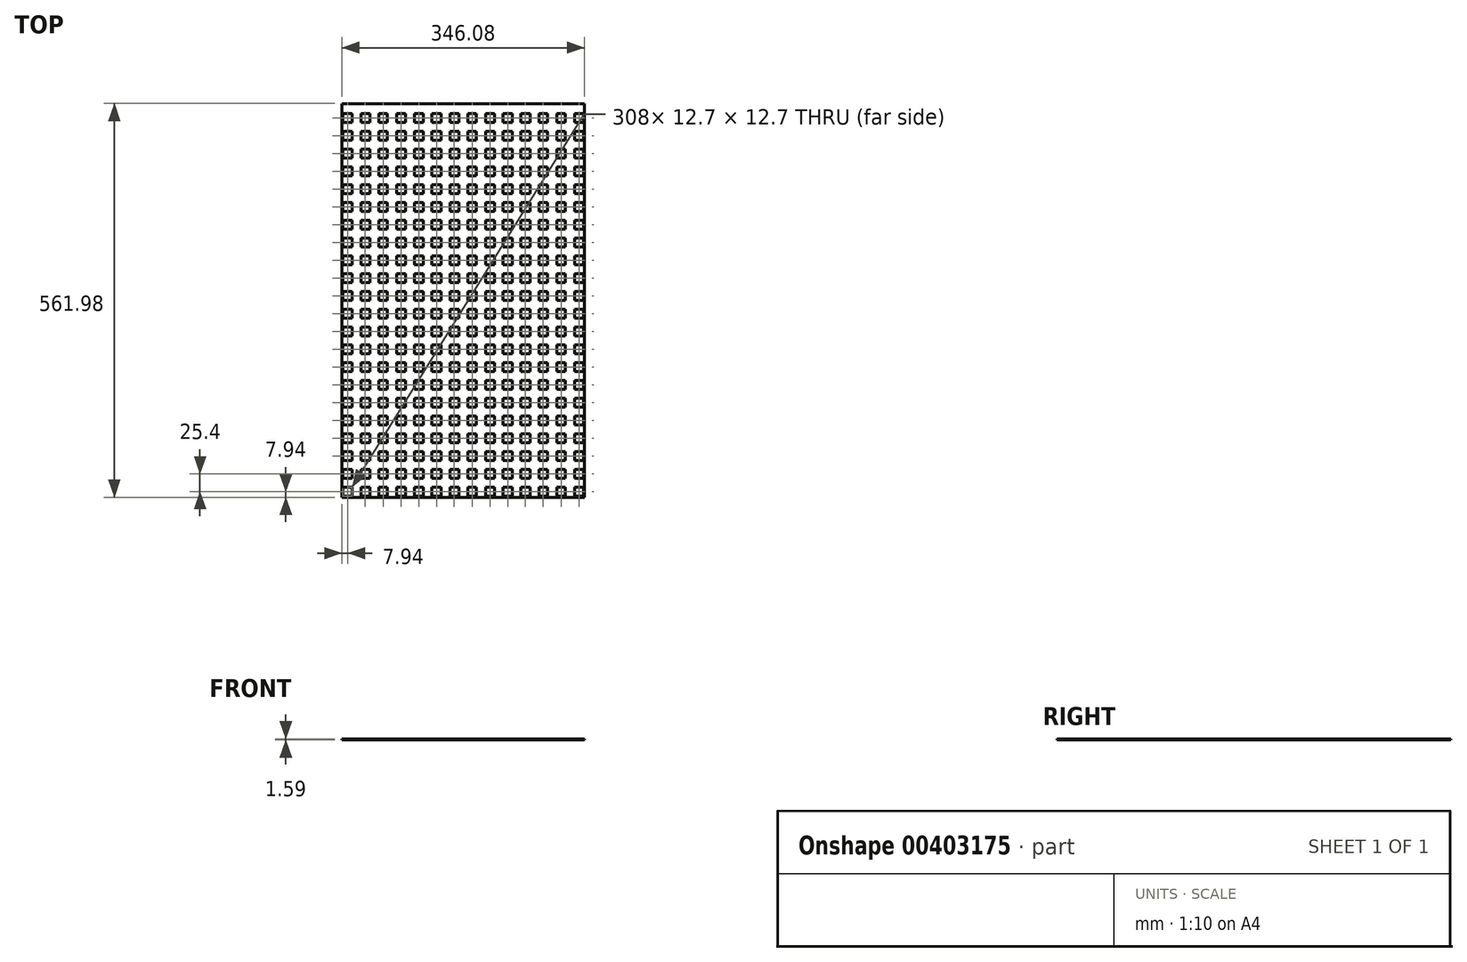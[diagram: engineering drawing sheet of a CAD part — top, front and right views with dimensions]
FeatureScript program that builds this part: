
annotation { "Feature Type Name" : "Feature", "Feature Type Description" : "" }
export const myFeature = defineFeature(function(context is Context, id is Id, definition is map)
    precondition{}
    {
        {
            var Q0;
            Q0=qCreatedBy(makeId("Top.planeOp"),FACE);
            var sketch = newSketch(context, id + "F0", { "sketchPlane" : qUnion([Q0])});
            skLineSegment(sketch, "E0.bottom", {"start": v(6.35, 6.35) * mm, "end": v(-6.35, 6.35) * mm});
            skLineSegment(sketch, "E0.top", {"start": v(6.35, -6.35) * mm, "end": v(-6.35, -6.35) * mm});
            skLineSegment(sketch, "E0.left", {"start": v(6.35, 6.35) * mm, "end": v(6.35, -6.35) * mm});
            skLineSegment(sketch, "E0.right", {"start": v(-6.35, 6.35) * mm, "end": v(-6.35, -6.35) * mm});
            skPoint(sketch, "E0.middle", {"position": v(0, 0) * mm});
            skLineSegment(sketch, "E1.0", {"start": v(4.76, 4.76) * mm, "end": v(-4.76, 4.76) * mm});
            skLineSegment(sketch, "E1.1", {"start": v(4.76, 4.76) * mm, "end": v(4.76, -4.76) * mm});
            skLineSegment(sketch, "E1.2", {"start": v(4.76, -4.76) * mm, "end": v(-4.76, -4.76) * mm});
            skLineSegment(sketch, "E1.3", {"start": v(-4.76, 4.76) * mm, "end": v(-4.76, -4.76) * mm});
            skLineSegment(sketch, "E2.0.1.0", {"start": v(6.35, 19.05) * mm, "end": v(-6.35, 19.05) * mm});
            skLineSegment(sketch, "E2.0.1.1", {"start": v(-4.76, 30.16) * mm, "end": v(-4.76, 20.64) * mm});
            skPoint(sketch, "E2.0.1.2", {"position": v(0, 25.4) * mm});
            skLineSegment(sketch, "E2.0.1.3", {"start": v(4.76, 20.64) * mm, "end": v(-4.76, 20.64) * mm});
            skLineSegment(sketch, "E2.0.1.4", {"start": v(6.35, 31.75) * mm, "end": v(6.35, 19.05) * mm});
            skLineSegment(sketch, "E2.0.1.5", {"start": v(6.35, 31.75) * mm, "end": v(-6.35, 31.75) * mm});
            skLineSegment(sketch, "E2.0.1.6", {"start": v(-6.35, 31.75) * mm, "end": v(-6.35, 19.05) * mm});
            skLineSegment(sketch, "E2.0.1.7", {"start": v(4.76, 30.16) * mm, "end": v(-4.76, 30.16) * mm});
            skLineSegment(sketch, "E2.0.1.8", {"start": v(4.76, 30.16) * mm, "end": v(4.76, 20.64) * mm});
            skLineSegment(sketch, "E2.0.2.0", {"start": v(6.35, 44.45) * mm, "end": v(-6.35, 44.45) * mm});
            skLineSegment(sketch, "E2.0.2.1", {"start": v(-4.76, 55.56) * mm, "end": v(-4.76, 46.04) * mm});
            skPoint(sketch, "E2.0.2.2", {"position": v(0, 50.8) * mm});
            skLineSegment(sketch, "E2.0.2.3", {"start": v(4.76, 46.04) * mm, "end": v(-4.76, 46.04) * mm});
            skLineSegment(sketch, "E2.0.2.4", {"start": v(6.35, 57.15) * mm, "end": v(6.35, 44.45) * mm});
            skLineSegment(sketch, "E2.0.2.5", {"start": v(6.35, 57.15) * mm, "end": v(-6.35, 57.15) * mm});
            skLineSegment(sketch, "E2.0.2.6", {"start": v(-6.35, 57.15) * mm, "end": v(-6.35, 44.45) * mm});
            skLineSegment(sketch, "E2.0.2.7", {"start": v(4.76, 55.56) * mm, "end": v(-4.76, 55.56) * mm});
            skLineSegment(sketch, "E2.0.2.8", {"start": v(4.76, 55.56) * mm, "end": v(4.76, 46.04) * mm});
            skLineSegment(sketch, "E2.0.3.0", {"start": v(6.35, 69.85) * mm, "end": v(-6.35, 69.85) * mm});
            skLineSegment(sketch, "E2.0.3.1", {"start": v(-4.76, 80.96) * mm, "end": v(-4.76, 71.44) * mm});
            skPoint(sketch, "E2.0.3.2", {"position": v(0, 76.2) * mm});
            skLineSegment(sketch, "E2.0.3.3", {"start": v(4.76, 71.44) * mm, "end": v(-4.76, 71.44) * mm});
            skLineSegment(sketch, "E2.0.3.4", {"start": v(6.35, 82.55) * mm, "end": v(6.35, 69.85) * mm});
            skLineSegment(sketch, "E2.0.3.5", {"start": v(6.35, 82.55) * mm, "end": v(-6.35, 82.55) * mm});
            skLineSegment(sketch, "E2.0.3.6", {"start": v(-6.35, 82.55) * mm, "end": v(-6.35, 69.85) * mm});
            skLineSegment(sketch, "E2.0.3.7", {"start": v(4.76, 80.96) * mm, "end": v(-4.76, 80.96) * mm});
            skLineSegment(sketch, "E2.0.3.8", {"start": v(4.76, 80.96) * mm, "end": v(4.76, 71.44) * mm});
            skLineSegment(sketch, "E2.0.4.0", {"start": v(6.35, 95.25) * mm, "end": v(-6.35, 95.25) * mm});
            skLineSegment(sketch, "E2.0.4.1", {"start": v(-4.76, 106.36) * mm, "end": v(-4.76, 96.84) * mm});
            skPoint(sketch, "E2.0.4.2", {"position": v(0, 101.6) * mm});
            skLineSegment(sketch, "E2.0.4.3", {"start": v(4.76, 96.84) * mm, "end": v(-4.76, 96.84) * mm});
            skLineSegment(sketch, "E2.0.4.4", {"start": v(6.35, 107.95) * mm, "end": v(6.35, 95.25) * mm});
            skLineSegment(sketch, "E2.0.4.5", {"start": v(6.35, 107.95) * mm, "end": v(-6.35, 107.95) * mm});
            skLineSegment(sketch, "E2.0.4.6", {"start": v(-6.35, 107.95) * mm, "end": v(-6.35, 95.25) * mm});
            skLineSegment(sketch, "E2.0.4.7", {"start": v(4.76, 106.36) * mm, "end": v(-4.76, 106.36) * mm});
            skLineSegment(sketch, "E2.0.4.8", {"start": v(4.76, 106.36) * mm, "end": v(4.76, 96.84) * mm});
            skLineSegment(sketch, "E2.0.5.0", {"start": v(6.35, 120.65) * mm, "end": v(-6.35, 120.65) * mm});
            skLineSegment(sketch, "E2.0.5.1", {"start": v(-4.76, 131.76) * mm, "end": v(-4.76, 122.24) * mm});
            skPoint(sketch, "E2.0.5.2", {"position": v(0, 127) * mm});
            skLineSegment(sketch, "E2.0.5.3", {"start": v(4.76, 122.24) * mm, "end": v(-4.76, 122.24) * mm});
            skLineSegment(sketch, "E2.0.5.4", {"start": v(6.35, 133.35) * mm, "end": v(6.35, 120.65) * mm});
            skLineSegment(sketch, "E2.0.5.5", {"start": v(6.35, 133.35) * mm, "end": v(-6.35, 133.35) * mm});
            skLineSegment(sketch, "E2.0.5.6", {"start": v(-6.35, 133.35) * mm, "end": v(-6.35, 120.65) * mm});
            skLineSegment(sketch, "E2.0.5.7", {"start": v(4.76, 131.76) * mm, "end": v(-4.76, 131.76) * mm});
            skLineSegment(sketch, "E2.0.5.8", {"start": v(4.76, 131.76) * mm, "end": v(4.76, 122.24) * mm});
            skLineSegment(sketch, "E2.0.6.0", {"start": v(6.35, 146.05) * mm, "end": v(-6.35, 146.05) * mm});
            skLineSegment(sketch, "E2.0.6.1", {"start": v(-4.76, 157.16) * mm, "end": v(-4.76, 147.64) * mm});
            skPoint(sketch, "E2.0.6.2", {"position": v(0, 152.4) * mm});
            skLineSegment(sketch, "E2.0.6.3", {"start": v(4.76, 147.64) * mm, "end": v(-4.76, 147.64) * mm});
            skLineSegment(sketch, "E2.0.6.4", {"start": v(6.35, 158.75) * mm, "end": v(6.35, 146.05) * mm});
            skLineSegment(sketch, "E2.0.6.5", {"start": v(6.35, 158.75) * mm, "end": v(-6.35, 158.75) * mm});
            skLineSegment(sketch, "E2.0.6.6", {"start": v(-6.35, 158.75) * mm, "end": v(-6.35, 146.05) * mm});
            skLineSegment(sketch, "E2.0.6.7", {"start": v(4.76, 157.16) * mm, "end": v(-4.76, 157.16) * mm});
            skLineSegment(sketch, "E2.0.6.8", {"start": v(4.76, 157.16) * mm, "end": v(4.76, 147.64) * mm});
            skLineSegment(sketch, "E2.0.7.0", {"start": v(6.35, 171.45) * mm, "end": v(-6.35, 171.45) * mm});
            skLineSegment(sketch, "E2.0.7.1", {"start": v(-4.76, 182.56) * mm, "end": v(-4.76, 173.04) * mm});
            skPoint(sketch, "E2.0.7.2", {"position": v(0, 177.8) * mm});
            skLineSegment(sketch, "E2.0.7.3", {"start": v(4.76, 173.04) * mm, "end": v(-4.76, 173.04) * mm});
            skLineSegment(sketch, "E2.0.7.4", {"start": v(6.35, 184.15) * mm, "end": v(6.35, 171.45) * mm});
            skLineSegment(sketch, "E2.0.7.5", {"start": v(6.35, 184.15) * mm, "end": v(-6.35, 184.15) * mm});
            skLineSegment(sketch, "E2.0.7.6", {"start": v(-6.35, 184.15) * mm, "end": v(-6.35, 171.45) * mm});
            skLineSegment(sketch, "E2.0.7.7", {"start": v(4.76, 182.56) * mm, "end": v(-4.76, 182.56) * mm});
            skLineSegment(sketch, "E2.0.7.8", {"start": v(4.76, 182.56) * mm, "end": v(4.76, 173.04) * mm});
            skLineSegment(sketch, "E2.0.8.0", {"start": v(6.35, 196.85) * mm, "end": v(-6.35, 196.85) * mm});
            skLineSegment(sketch, "E2.0.8.1", {"start": v(-4.76, 207.96) * mm, "end": v(-4.76, 198.44) * mm});
            skPoint(sketch, "E2.0.8.2", {"position": v(0, 203.2) * mm});
            skLineSegment(sketch, "E2.0.8.3", {"start": v(4.76, 198.44) * mm, "end": v(-4.76, 198.44) * mm});
            skLineSegment(sketch, "E2.0.8.4", {"start": v(6.35, 209.55) * mm, "end": v(6.35, 196.85) * mm});
            skLineSegment(sketch, "E2.0.8.5", {"start": v(6.35, 209.55) * mm, "end": v(-6.35, 209.55) * mm});
            skLineSegment(sketch, "E2.0.8.6", {"start": v(-6.35, 209.55) * mm, "end": v(-6.35, 196.85) * mm});
            skLineSegment(sketch, "E2.0.8.7", {"start": v(4.76, 207.96) * mm, "end": v(-4.76, 207.96) * mm});
            skLineSegment(sketch, "E2.0.8.8", {"start": v(4.76, 207.96) * mm, "end": v(4.76, 198.44) * mm});
            skLineSegment(sketch, "E2.0.9.0", {"start": v(6.35, 222.25) * mm, "end": v(-6.35, 222.25) * mm});
            skLineSegment(sketch, "E2.0.9.1", {"start": v(-4.76, 233.36) * mm, "end": v(-4.76, 223.84) * mm});
            skPoint(sketch, "E2.0.9.2", {"position": v(0, 228.6) * mm});
            skLineSegment(sketch, "E2.0.9.3", {"start": v(4.76, 223.84) * mm, "end": v(-4.76, 223.84) * mm});
            skLineSegment(sketch, "E2.0.9.4", {"start": v(6.35, 234.95) * mm, "end": v(6.35, 222.25) * mm});
            skLineSegment(sketch, "E2.0.9.5", {"start": v(6.35, 234.95) * mm, "end": v(-6.35, 234.95) * mm});
            skLineSegment(sketch, "E2.0.9.6", {"start": v(-6.35, 234.95) * mm, "end": v(-6.35, 222.25) * mm});
            skLineSegment(sketch, "E2.0.9.7", {"start": v(4.76, 233.36) * mm, "end": v(-4.76, 233.36) * mm});
            skLineSegment(sketch, "E2.0.9.8", {"start": v(4.76, 233.36) * mm, "end": v(4.76, 223.84) * mm});
            skLineSegment(sketch, "E2.0.10.0", {"start": v(6.35, 247.65) * mm, "end": v(-6.35, 247.65) * mm});
            skLineSegment(sketch, "E2.0.10.1", {"start": v(-4.76, 258.76) * mm, "end": v(-4.76, 249.24) * mm});
            skPoint(sketch, "E2.0.10.2", {"position": v(0, 254) * mm});
            skLineSegment(sketch, "E2.0.10.3", {"start": v(4.76, 249.24) * mm, "end": v(-4.76, 249.24) * mm});
            skLineSegment(sketch, "E2.0.10.4", {"start": v(6.35, 260.35) * mm, "end": v(6.35, 247.65) * mm});
            skLineSegment(sketch, "E2.0.10.5", {"start": v(6.35, 260.35) * mm, "end": v(-6.35, 260.35) * mm});
            skLineSegment(sketch, "E2.0.10.6", {"start": v(-6.35, 260.35) * mm, "end": v(-6.35, 247.65) * mm});
            skLineSegment(sketch, "E2.0.10.7", {"start": v(4.76, 258.76) * mm, "end": v(-4.76, 258.76) * mm});
            skLineSegment(sketch, "E2.0.10.8", {"start": v(4.76, 258.76) * mm, "end": v(4.76, 249.24) * mm});
            skLineSegment(sketch, "E2.0.11.0", {"start": v(6.35, 273.05) * mm, "end": v(-6.35, 273.05) * mm});
            skLineSegment(sketch, "E2.0.11.1", {"start": v(-4.76, 284.16) * mm, "end": v(-4.76, 274.64) * mm});
            skPoint(sketch, "E2.0.11.2", {"position": v(0, 279.4) * mm});
            skLineSegment(sketch, "E2.0.11.3", {"start": v(4.76, 274.64) * mm, "end": v(-4.76, 274.64) * mm});
            skLineSegment(sketch, "E2.0.11.4", {"start": v(6.35, 285.75) * mm, "end": v(6.35, 273.05) * mm});
            skLineSegment(sketch, "E2.0.11.5", {"start": v(6.35, 285.75) * mm, "end": v(-6.35, 285.75) * mm});
            skLineSegment(sketch, "E2.0.11.6", {"start": v(-6.35, 285.75) * mm, "end": v(-6.35, 273.05) * mm});
            skLineSegment(sketch, "E2.0.11.7", {"start": v(4.76, 284.16) * mm, "end": v(-4.76, 284.16) * mm});
            skLineSegment(sketch, "E2.0.11.8", {"start": v(4.76, 284.16) * mm, "end": v(4.76, 274.64) * mm});
            skLineSegment(sketch, "E2.0.12.0", {"start": v(6.35, 298.45) * mm, "end": v(-6.35, 298.45) * mm});
            skLineSegment(sketch, "E2.0.12.1", {"start": v(-4.76, 309.56) * mm, "end": v(-4.76, 300.04) * mm});
            skPoint(sketch, "E2.0.12.2", {"position": v(0, 304.8) * mm});
            skLineSegment(sketch, "E2.0.12.3", {"start": v(4.76, 300.04) * mm, "end": v(-4.76, 300.04) * mm});
            skLineSegment(sketch, "E2.0.12.4", {"start": v(6.35, 311.15) * mm, "end": v(6.35, 298.45) * mm});
            skLineSegment(sketch, "E2.0.12.5", {"start": v(6.35, 311.15) * mm, "end": v(-6.35, 311.15) * mm});
            skLineSegment(sketch, "E2.0.12.6", {"start": v(-6.35, 311.15) * mm, "end": v(-6.35, 298.45) * mm});
            skLineSegment(sketch, "E2.0.12.7", {"start": v(4.76, 309.56) * mm, "end": v(-4.76, 309.56) * mm});
            skLineSegment(sketch, "E2.0.12.8", {"start": v(4.76, 309.56) * mm, "end": v(4.76, 300.04) * mm});
            skLineSegment(sketch, "E2.0.13.0", {"start": v(6.35, 323.85) * mm, "end": v(-6.35, 323.85) * mm});
            skLineSegment(sketch, "E2.0.13.1", {"start": v(-4.76, 334.96) * mm, "end": v(-4.76, 325.44) * mm});
            skPoint(sketch, "E2.0.13.2", {"position": v(0, 330.2) * mm});
            skLineSegment(sketch, "E2.0.13.3", {"start": v(4.76, 325.44) * mm, "end": v(-4.76, 325.44) * mm});
            skLineSegment(sketch, "E2.0.13.4", {"start": v(6.35, 336.55) * mm, "end": v(6.35, 323.85) * mm});
            skLineSegment(sketch, "E2.0.13.5", {"start": v(6.35, 336.55) * mm, "end": v(-6.35, 336.55) * mm});
            skLineSegment(sketch, "E2.0.13.6", {"start": v(-6.35, 336.55) * mm, "end": v(-6.35, 323.85) * mm});
            skLineSegment(sketch, "E2.0.13.7", {"start": v(4.76, 334.96) * mm, "end": v(-4.76, 334.96) * mm});
            skLineSegment(sketch, "E2.0.13.8", {"start": v(4.76, 334.96) * mm, "end": v(4.76, 325.44) * mm});
            skLineSegment(sketch, "E2.0.14.0", {"start": v(6.35, 349.25) * mm, "end": v(-6.35, 349.25) * mm});
            skLineSegment(sketch, "E2.0.14.1", {"start": v(-4.76, 360.36) * mm, "end": v(-4.76, 350.84) * mm});
            skPoint(sketch, "E2.0.14.2", {"position": v(0, 355.6) * mm});
            skLineSegment(sketch, "E2.0.14.3", {"start": v(4.76, 350.84) * mm, "end": v(-4.76, 350.84) * mm});
            skLineSegment(sketch, "E2.0.14.4", {"start": v(6.35, 361.95) * mm, "end": v(6.35, 349.25) * mm});
            skLineSegment(sketch, "E2.0.14.5", {"start": v(6.35, 361.95) * mm, "end": v(-6.35, 361.95) * mm});
            skLineSegment(sketch, "E2.0.14.6", {"start": v(-6.35, 361.95) * mm, "end": v(-6.35, 349.25) * mm});
            skLineSegment(sketch, "E2.0.14.7", {"start": v(4.76, 360.36) * mm, "end": v(-4.76, 360.36) * mm});
            skLineSegment(sketch, "E2.0.14.8", {"start": v(4.76, 360.36) * mm, "end": v(4.76, 350.84) * mm});
            skLineSegment(sketch, "E2.1.0.0", {"start": v(31.75, -6.35) * mm, "end": v(19.05, -6.35) * mm});
            skLineSegment(sketch, "E2.1.0.1", {"start": v(20.64, 4.76) * mm, "end": v(20.64, -4.76) * mm});
            skPoint(sketch, "E2.1.0.2", {"position": v(25.4, 0) * mm});
            skLineSegment(sketch, "E2.1.0.3", {"start": v(30.16, -4.76) * mm, "end": v(20.64, -4.76) * mm});
            skLineSegment(sketch, "E2.1.0.4", {"start": v(31.75, 6.35) * mm, "end": v(31.75, -6.35) * mm});
            skLineSegment(sketch, "E2.1.0.5", {"start": v(31.75, 6.35) * mm, "end": v(19.05, 6.35) * mm});
            skLineSegment(sketch, "E2.1.0.6", {"start": v(19.05, 6.35) * mm, "end": v(19.05, -6.35) * mm});
            skLineSegment(sketch, "E2.1.0.7", {"start": v(30.16, 4.76) * mm, "end": v(20.64, 4.76) * mm});
            skLineSegment(sketch, "E2.1.0.8", {"start": v(30.16, 4.76) * mm, "end": v(30.16, -4.76) * mm});
            skLineSegment(sketch, "E2.1.1.0", {"start": v(31.75, 19.05) * mm, "end": v(19.05, 19.05) * mm});
            skLineSegment(sketch, "E2.1.1.1", {"start": v(20.64, 30.16) * mm, "end": v(20.64, 20.64) * mm});
            skPoint(sketch, "E2.1.1.2", {"position": v(25.4, 25.4) * mm});
            skLineSegment(sketch, "E2.1.1.3", {"start": v(30.16, 20.64) * mm, "end": v(20.64, 20.64) * mm});
            skLineSegment(sketch, "E2.1.1.4", {"start": v(31.75, 31.75) * mm, "end": v(31.75, 19.05) * mm});
            skLineSegment(sketch, "E2.1.1.5", {"start": v(31.75, 31.75) * mm, "end": v(19.05, 31.75) * mm});
            skLineSegment(sketch, "E2.1.1.6", {"start": v(19.05, 31.75) * mm, "end": v(19.05, 19.05) * mm});
            skLineSegment(sketch, "E2.1.1.7", {"start": v(30.16, 30.16) * mm, "end": v(20.64, 30.16) * mm});
            skLineSegment(sketch, "E2.1.1.8", {"start": v(30.16, 30.16) * mm, "end": v(30.16, 20.64) * mm});
            skLineSegment(sketch, "E2.1.2.0", {"start": v(31.75, 44.45) * mm, "end": v(19.05, 44.45) * mm});
            skLineSegment(sketch, "E2.1.2.1", {"start": v(20.64, 55.56) * mm, "end": v(20.64, 46.04) * mm});
            skPoint(sketch, "E2.1.2.2", {"position": v(25.4, 50.8) * mm});
            skLineSegment(sketch, "E2.1.2.3", {"start": v(30.16, 46.04) * mm, "end": v(20.64, 46.04) * mm});
            skLineSegment(sketch, "E2.1.2.4", {"start": v(31.75, 57.15) * mm, "end": v(31.75, 44.45) * mm});
            skLineSegment(sketch, "E2.1.2.5", {"start": v(31.75, 57.15) * mm, "end": v(19.05, 57.15) * mm});
            skLineSegment(sketch, "E2.1.2.6", {"start": v(19.05, 57.15) * mm, "end": v(19.05, 44.45) * mm});
            skLineSegment(sketch, "E2.1.2.7", {"start": v(30.16, 55.56) * mm, "end": v(20.64, 55.56) * mm});
            skLineSegment(sketch, "E2.1.2.8", {"start": v(30.16, 55.56) * mm, "end": v(30.16, 46.04) * mm});
            skLineSegment(sketch, "E2.1.3.0", {"start": v(31.75, 69.85) * mm, "end": v(19.05, 69.85) * mm});
            skLineSegment(sketch, "E2.1.3.1", {"start": v(20.64, 80.96) * mm, "end": v(20.64, 71.44) * mm});
            skPoint(sketch, "E2.1.3.2", {"position": v(25.4, 76.2) * mm});
            skLineSegment(sketch, "E2.1.3.3", {"start": v(30.16, 71.44) * mm, "end": v(20.64, 71.44) * mm});
            skLineSegment(sketch, "E2.1.3.4", {"start": v(31.75, 82.55) * mm, "end": v(31.75, 69.85) * mm});
            skLineSegment(sketch, "E2.1.3.5", {"start": v(31.75, 82.55) * mm, "end": v(19.05, 82.55) * mm});
            skLineSegment(sketch, "E2.1.3.6", {"start": v(19.05, 82.55) * mm, "end": v(19.05, 69.85) * mm});
            skLineSegment(sketch, "E2.1.3.7", {"start": v(30.16, 80.96) * mm, "end": v(20.64, 80.96) * mm});
            skLineSegment(sketch, "E2.1.3.8", {"start": v(30.16, 80.96) * mm, "end": v(30.16, 71.44) * mm});
            skLineSegment(sketch, "E2.1.4.0", {"start": v(31.75, 95.25) * mm, "end": v(19.05, 95.25) * mm});
            skLineSegment(sketch, "E2.1.4.1", {"start": v(20.64, 106.36) * mm, "end": v(20.64, 96.84) * mm});
            skPoint(sketch, "E2.1.4.2", {"position": v(25.4, 101.6) * mm});
            skLineSegment(sketch, "E2.1.4.3", {"start": v(30.16, 96.84) * mm, "end": v(20.64, 96.84) * mm});
            skLineSegment(sketch, "E2.1.4.4", {"start": v(31.75, 107.95) * mm, "end": v(31.75, 95.25) * mm});
            skLineSegment(sketch, "E2.1.4.5", {"start": v(31.75, 107.95) * mm, "end": v(19.05, 107.95) * mm});
            skLineSegment(sketch, "E2.1.4.6", {"start": v(19.05, 107.95) * mm, "end": v(19.05, 95.25) * mm});
            skLineSegment(sketch, "E2.1.4.7", {"start": v(30.16, 106.36) * mm, "end": v(20.64, 106.36) * mm});
            skLineSegment(sketch, "E2.1.4.8", {"start": v(30.16, 106.36) * mm, "end": v(30.16, 96.84) * mm});
            skLineSegment(sketch, "E2.1.5.0", {"start": v(31.75, 120.65) * mm, "end": v(19.05, 120.65) * mm});
            skLineSegment(sketch, "E2.1.5.1", {"start": v(20.64, 131.76) * mm, "end": v(20.64, 122.24) * mm});
            skPoint(sketch, "E2.1.5.2", {"position": v(25.4, 127) * mm});
            skLineSegment(sketch, "E2.1.5.3", {"start": v(30.16, 122.24) * mm, "end": v(20.64, 122.24) * mm});
            skLineSegment(sketch, "E2.1.5.4", {"start": v(31.75, 133.35) * mm, "end": v(31.75, 120.65) * mm});
            skLineSegment(sketch, "E2.1.5.5", {"start": v(31.75, 133.35) * mm, "end": v(19.05, 133.35) * mm});
            skLineSegment(sketch, "E2.1.5.6", {"start": v(19.05, 133.35) * mm, "end": v(19.05, 120.65) * mm});
            skLineSegment(sketch, "E2.1.5.7", {"start": v(30.16, 131.76) * mm, "end": v(20.64, 131.76) * mm});
            skLineSegment(sketch, "E2.1.5.8", {"start": v(30.16, 131.76) * mm, "end": v(30.16, 122.24) * mm});
            skLineSegment(sketch, "E2.1.6.0", {"start": v(31.75, 146.05) * mm, "end": v(19.05, 146.05) * mm});
            skLineSegment(sketch, "E2.1.6.1", {"start": v(20.64, 157.16) * mm, "end": v(20.64, 147.64) * mm});
            skPoint(sketch, "E2.1.6.2", {"position": v(25.4, 152.4) * mm});
            skLineSegment(sketch, "E2.1.6.3", {"start": v(30.16, 147.64) * mm, "end": v(20.64, 147.64) * mm});
            skLineSegment(sketch, "E2.1.6.4", {"start": v(31.75, 158.75) * mm, "end": v(31.75, 146.05) * mm});
            skLineSegment(sketch, "E2.1.6.5", {"start": v(31.75, 158.75) * mm, "end": v(19.05, 158.75) * mm});
            skLineSegment(sketch, "E2.1.6.6", {"start": v(19.05, 158.75) * mm, "end": v(19.05, 146.05) * mm});
            skLineSegment(sketch, "E2.1.6.7", {"start": v(30.16, 157.16) * mm, "end": v(20.64, 157.16) * mm});
            skLineSegment(sketch, "E2.1.6.8", {"start": v(30.16, 157.16) * mm, "end": v(30.16, 147.64) * mm});
            skLineSegment(sketch, "E2.1.7.0", {"start": v(31.75, 171.45) * mm, "end": v(19.05, 171.45) * mm});
            skLineSegment(sketch, "E2.1.7.1", {"start": v(20.64, 182.56) * mm, "end": v(20.64, 173.04) * mm});
            skPoint(sketch, "E2.1.7.2", {"position": v(25.4, 177.8) * mm});
            skLineSegment(sketch, "E2.1.7.3", {"start": v(30.16, 173.04) * mm, "end": v(20.64, 173.04) * mm});
            skLineSegment(sketch, "E2.1.7.4", {"start": v(31.75, 184.15) * mm, "end": v(31.75, 171.45) * mm});
            skLineSegment(sketch, "E2.1.7.5", {"start": v(31.75, 184.15) * mm, "end": v(19.05, 184.15) * mm});
            skLineSegment(sketch, "E2.1.7.6", {"start": v(19.05, 184.15) * mm, "end": v(19.05, 171.45) * mm});
            skLineSegment(sketch, "E2.1.7.7", {"start": v(30.16, 182.56) * mm, "end": v(20.64, 182.56) * mm});
            skLineSegment(sketch, "E2.1.7.8", {"start": v(30.16, 182.56) * mm, "end": v(30.16, 173.04) * mm});
            skLineSegment(sketch, "E2.1.8.0", {"start": v(31.75, 196.85) * mm, "end": v(19.05, 196.85) * mm});
            skLineSegment(sketch, "E2.1.8.1", {"start": v(20.64, 207.96) * mm, "end": v(20.64, 198.44) * mm});
            skPoint(sketch, "E2.1.8.2", {"position": v(25.4, 203.2) * mm});
            skLineSegment(sketch, "E2.1.8.3", {"start": v(30.16, 198.44) * mm, "end": v(20.64, 198.44) * mm});
            skLineSegment(sketch, "E2.1.8.4", {"start": v(31.75, 209.55) * mm, "end": v(31.75, 196.85) * mm});
            skLineSegment(sketch, "E2.1.8.5", {"start": v(31.75, 209.55) * mm, "end": v(19.05, 209.55) * mm});
            skLineSegment(sketch, "E2.1.8.6", {"start": v(19.05, 209.55) * mm, "end": v(19.05, 196.85) * mm});
            skLineSegment(sketch, "E2.1.8.7", {"start": v(30.16, 207.96) * mm, "end": v(20.64, 207.96) * mm});
            skLineSegment(sketch, "E2.1.8.8", {"start": v(30.16, 207.96) * mm, "end": v(30.16, 198.44) * mm});
            skLineSegment(sketch, "E2.1.9.0", {"start": v(31.75, 222.25) * mm, "end": v(19.05, 222.25) * mm});
            skLineSegment(sketch, "E2.1.9.1", {"start": v(20.64, 233.36) * mm, "end": v(20.64, 223.84) * mm});
            skPoint(sketch, "E2.1.9.2", {"position": v(25.4, 228.6) * mm});
            skLineSegment(sketch, "E2.1.9.3", {"start": v(30.16, 223.84) * mm, "end": v(20.64, 223.84) * mm});
            skLineSegment(sketch, "E2.1.9.4", {"start": v(31.75, 234.95) * mm, "end": v(31.75, 222.25) * mm});
            skLineSegment(sketch, "E2.1.9.5", {"start": v(31.75, 234.95) * mm, "end": v(19.05, 234.95) * mm});
            skLineSegment(sketch, "E2.1.9.6", {"start": v(19.05, 234.95) * mm, "end": v(19.05, 222.25) * mm});
            skLineSegment(sketch, "E2.1.9.7", {"start": v(30.16, 233.36) * mm, "end": v(20.64, 233.36) * mm});
            skLineSegment(sketch, "E2.1.9.8", {"start": v(30.16, 233.36) * mm, "end": v(30.16, 223.84) * mm});
            skLineSegment(sketch, "E2.1.10.0", {"start": v(31.75, 247.65) * mm, "end": v(19.05, 247.65) * mm});
            skLineSegment(sketch, "E2.1.10.1", {"start": v(20.64, 258.76) * mm, "end": v(20.64, 249.24) * mm});
            skPoint(sketch, "E2.1.10.2", {"position": v(25.4, 254) * mm});
            skLineSegment(sketch, "E2.1.10.3", {"start": v(30.16, 249.24) * mm, "end": v(20.64, 249.24) * mm});
            skLineSegment(sketch, "E2.1.10.4", {"start": v(31.75, 260.35) * mm, "end": v(31.75, 247.65) * mm});
            skLineSegment(sketch, "E2.1.10.5", {"start": v(31.75, 260.35) * mm, "end": v(19.05, 260.35) * mm});
            skLineSegment(sketch, "E2.1.10.6", {"start": v(19.05, 260.35) * mm, "end": v(19.05, 247.65) * mm});
            skLineSegment(sketch, "E2.1.10.7", {"start": v(30.16, 258.76) * mm, "end": v(20.64, 258.76) * mm});
            skLineSegment(sketch, "E2.1.10.8", {"start": v(30.16, 258.76) * mm, "end": v(30.16, 249.24) * mm});
            skLineSegment(sketch, "E2.1.11.0", {"start": v(31.75, 273.05) * mm, "end": v(19.05, 273.05) * mm});
            skLineSegment(sketch, "E2.1.11.1", {"start": v(20.64, 284.16) * mm, "end": v(20.64, 274.64) * mm});
            skPoint(sketch, "E2.1.11.2", {"position": v(25.4, 279.4) * mm});
            skLineSegment(sketch, "E2.1.11.3", {"start": v(30.16, 274.64) * mm, "end": v(20.64, 274.64) * mm});
            skLineSegment(sketch, "E2.1.11.4", {"start": v(31.75, 285.75) * mm, "end": v(31.75, 273.05) * mm});
            skLineSegment(sketch, "E2.1.11.5", {"start": v(31.75, 285.75) * mm, "end": v(19.05, 285.75) * mm});
            skLineSegment(sketch, "E2.1.11.6", {"start": v(19.05, 285.75) * mm, "end": v(19.05, 273.05) * mm});
            skLineSegment(sketch, "E2.1.11.7", {"start": v(30.16, 284.16) * mm, "end": v(20.64, 284.16) * mm});
            skLineSegment(sketch, "E2.1.11.8", {"start": v(30.16, 284.16) * mm, "end": v(30.16, 274.64) * mm});
            skLineSegment(sketch, "E2.1.12.0", {"start": v(31.75, 298.45) * mm, "end": v(19.05, 298.45) * mm});
            skLineSegment(sketch, "E2.1.12.1", {"start": v(20.64, 309.56) * mm, "end": v(20.64, 300.04) * mm});
            skPoint(sketch, "E2.1.12.2", {"position": v(25.4, 304.8) * mm});
            skLineSegment(sketch, "E2.1.12.3", {"start": v(30.16, 300.04) * mm, "end": v(20.64, 300.04) * mm});
            skLineSegment(sketch, "E2.1.12.4", {"start": v(31.75, 311.15) * mm, "end": v(31.75, 298.45) * mm});
            skLineSegment(sketch, "E2.1.12.5", {"start": v(31.75, 311.15) * mm, "end": v(19.05, 311.15) * mm});
            skLineSegment(sketch, "E2.1.12.6", {"start": v(19.05, 311.15) * mm, "end": v(19.05, 298.45) * mm});
            skLineSegment(sketch, "E2.1.12.7", {"start": v(30.16, 309.56) * mm, "end": v(20.64, 309.56) * mm});
            skLineSegment(sketch, "E2.1.12.8", {"start": v(30.16, 309.56) * mm, "end": v(30.16, 300.04) * mm});
            skLineSegment(sketch, "E2.1.13.0", {"start": v(31.75, 323.85) * mm, "end": v(19.05, 323.85) * mm});
            skLineSegment(sketch, "E2.1.13.1", {"start": v(20.64, 334.96) * mm, "end": v(20.64, 325.44) * mm});
            skPoint(sketch, "E2.1.13.2", {"position": v(25.4, 330.2) * mm});
            skLineSegment(sketch, "E2.1.13.3", {"start": v(30.16, 325.44) * mm, "end": v(20.64, 325.44) * mm});
            skLineSegment(sketch, "E2.1.13.4", {"start": v(31.75, 336.55) * mm, "end": v(31.75, 323.85) * mm});
            skLineSegment(sketch, "E2.1.13.5", {"start": v(31.75, 336.55) * mm, "end": v(19.05, 336.55) * mm});
            skLineSegment(sketch, "E2.1.13.6", {"start": v(19.05, 336.55) * mm, "end": v(19.05, 323.85) * mm});
            skLineSegment(sketch, "E2.1.13.7", {"start": v(30.16, 334.96) * mm, "end": v(20.64, 334.96) * mm});
            skLineSegment(sketch, "E2.1.13.8", {"start": v(30.16, 334.96) * mm, "end": v(30.16, 325.44) * mm});
            skLineSegment(sketch, "E2.1.14.0", {"start": v(31.75, 349.25) * mm, "end": v(19.05, 349.25) * mm});
            skLineSegment(sketch, "E2.1.14.1", {"start": v(20.64, 360.36) * mm, "end": v(20.64, 350.84) * mm});
            skPoint(sketch, "E2.1.14.2", {"position": v(25.4, 355.6) * mm});
            skLineSegment(sketch, "E2.1.14.3", {"start": v(30.16, 350.84) * mm, "end": v(20.64, 350.84) * mm});
            skLineSegment(sketch, "E2.1.14.4", {"start": v(31.75, 361.95) * mm, "end": v(31.75, 349.25) * mm});
            skLineSegment(sketch, "E2.1.14.5", {"start": v(31.75, 361.95) * mm, "end": v(19.05, 361.95) * mm});
            skLineSegment(sketch, "E2.1.14.6", {"start": v(19.05, 361.95) * mm, "end": v(19.05, 349.25) * mm});
            skLineSegment(sketch, "E2.1.14.7", {"start": v(30.16, 360.36) * mm, "end": v(20.64, 360.36) * mm});
            skLineSegment(sketch, "E2.1.14.8", {"start": v(30.16, 360.36) * mm, "end": v(30.16, 350.84) * mm});
            skLineSegment(sketch, "E2.2.0.0", {"start": v(57.15, -6.35) * mm, "end": v(44.45, -6.35) * mm});
            skLineSegment(sketch, "E2.2.0.1", {"start": v(46.04, 4.76) * mm, "end": v(46.04, -4.76) * mm});
            skPoint(sketch, "E2.2.0.2", {"position": v(50.8, 0) * mm});
            skLineSegment(sketch, "E2.2.0.3", {"start": v(55.56, -4.76) * mm, "end": v(46.04, -4.76) * mm});
            skLineSegment(sketch, "E2.2.0.4", {"start": v(57.15, 6.35) * mm, "end": v(57.15, -6.35) * mm});
            skLineSegment(sketch, "E2.2.0.5", {"start": v(57.15, 6.35) * mm, "end": v(44.45, 6.35) * mm});
            skLineSegment(sketch, "E2.2.0.6", {"start": v(44.45, 6.35) * mm, "end": v(44.45, -6.35) * mm});
            skLineSegment(sketch, "E2.2.0.7", {"start": v(55.56, 4.76) * mm, "end": v(46.04, 4.76) * mm});
            skLineSegment(sketch, "E2.2.0.8", {"start": v(55.56, 4.76) * mm, "end": v(55.56, -4.76) * mm});
            skLineSegment(sketch, "E2.2.1.0", {"start": v(57.15, 19.05) * mm, "end": v(44.45, 19.05) * mm});
            skLineSegment(sketch, "E2.2.1.1", {"start": v(46.04, 30.16) * mm, "end": v(46.04, 20.64) * mm});
            skPoint(sketch, "E2.2.1.2", {"position": v(50.8, 25.4) * mm});
            skLineSegment(sketch, "E2.2.1.3", {"start": v(55.56, 20.64) * mm, "end": v(46.04, 20.64) * mm});
            skLineSegment(sketch, "E2.2.1.4", {"start": v(57.15, 31.75) * mm, "end": v(57.15, 19.05) * mm});
            skLineSegment(sketch, "E2.2.1.5", {"start": v(57.15, 31.75) * mm, "end": v(44.45, 31.75) * mm});
            skLineSegment(sketch, "E2.2.1.6", {"start": v(44.45, 31.75) * mm, "end": v(44.45, 19.05) * mm});
            skLineSegment(sketch, "E2.2.1.7", {"start": v(55.56, 30.16) * mm, "end": v(46.04, 30.16) * mm});
            skLineSegment(sketch, "E2.2.1.8", {"start": v(55.56, 30.16) * mm, "end": v(55.56, 20.64) * mm});
            skLineSegment(sketch, "E2.2.2.0", {"start": v(57.15, 44.45) * mm, "end": v(44.45, 44.45) * mm});
            skLineSegment(sketch, "E2.2.2.1", {"start": v(46.04, 55.56) * mm, "end": v(46.04, 46.04) * mm});
            skPoint(sketch, "E2.2.2.2", {"position": v(50.8, 50.8) * mm});
            skLineSegment(sketch, "E2.2.2.3", {"start": v(55.56, 46.04) * mm, "end": v(46.04, 46.04) * mm});
            skLineSegment(sketch, "E2.2.2.4", {"start": v(57.15, 57.15) * mm, "end": v(57.15, 44.45) * mm});
            skLineSegment(sketch, "E2.2.2.5", {"start": v(57.15, 57.15) * mm, "end": v(44.45, 57.15) * mm});
            skLineSegment(sketch, "E2.2.2.6", {"start": v(44.45, 57.15) * mm, "end": v(44.45, 44.45) * mm});
            skLineSegment(sketch, "E2.2.2.7", {"start": v(55.56, 55.56) * mm, "end": v(46.04, 55.56) * mm});
            skLineSegment(sketch, "E2.2.2.8", {"start": v(55.56, 55.56) * mm, "end": v(55.56, 46.04) * mm});
            skLineSegment(sketch, "E2.2.3.0", {"start": v(57.15, 69.85) * mm, "end": v(44.45, 69.85) * mm});
            skLineSegment(sketch, "E2.2.3.1", {"start": v(46.04, 80.96) * mm, "end": v(46.04, 71.44) * mm});
            skPoint(sketch, "E2.2.3.2", {"position": v(50.8, 76.2) * mm});
            skLineSegment(sketch, "E2.2.3.3", {"start": v(55.56, 71.44) * mm, "end": v(46.04, 71.44) * mm});
            skLineSegment(sketch, "E2.2.3.4", {"start": v(57.15, 82.55) * mm, "end": v(57.15, 69.85) * mm});
            skLineSegment(sketch, "E2.2.3.5", {"start": v(57.15, 82.55) * mm, "end": v(44.45, 82.55) * mm});
            skLineSegment(sketch, "E2.2.3.6", {"start": v(44.45, 82.55) * mm, "end": v(44.45, 69.85) * mm});
            skLineSegment(sketch, "E2.2.3.7", {"start": v(55.56, 80.96) * mm, "end": v(46.04, 80.96) * mm});
            skLineSegment(sketch, "E2.2.3.8", {"start": v(55.56, 80.96) * mm, "end": v(55.56, 71.44) * mm});
            skLineSegment(sketch, "E2.2.4.0", {"start": v(57.15, 95.25) * mm, "end": v(44.45, 95.25) * mm});
            skLineSegment(sketch, "E2.2.4.1", {"start": v(46.04, 106.36) * mm, "end": v(46.04, 96.84) * mm});
            skPoint(sketch, "E2.2.4.2", {"position": v(50.8, 101.6) * mm});
            skLineSegment(sketch, "E2.2.4.3", {"start": v(55.56, 96.84) * mm, "end": v(46.04, 96.84) * mm});
            skLineSegment(sketch, "E2.2.4.4", {"start": v(57.15, 107.95) * mm, "end": v(57.15, 95.25) * mm});
            skLineSegment(sketch, "E2.2.4.5", {"start": v(57.15, 107.95) * mm, "end": v(44.45, 107.95) * mm});
            skLineSegment(sketch, "E2.2.4.6", {"start": v(44.45, 107.95) * mm, "end": v(44.45, 95.25) * mm});
            skLineSegment(sketch, "E2.2.4.7", {"start": v(55.56, 106.36) * mm, "end": v(46.04, 106.36) * mm});
            skLineSegment(sketch, "E2.2.4.8", {"start": v(55.56, 106.36) * mm, "end": v(55.56, 96.84) * mm});
            skLineSegment(sketch, "E2.2.5.0", {"start": v(57.15, 120.65) * mm, "end": v(44.45, 120.65) * mm});
            skLineSegment(sketch, "E2.2.5.1", {"start": v(46.04, 131.76) * mm, "end": v(46.04, 122.24) * mm});
            skPoint(sketch, "E2.2.5.2", {"position": v(50.8, 127) * mm});
            skLineSegment(sketch, "E2.2.5.3", {"start": v(55.56, 122.24) * mm, "end": v(46.04, 122.24) * mm});
            skLineSegment(sketch, "E2.2.5.4", {"start": v(57.15, 133.35) * mm, "end": v(57.15, 120.65) * mm});
            skLineSegment(sketch, "E2.2.5.5", {"start": v(57.15, 133.35) * mm, "end": v(44.45, 133.35) * mm});
            skLineSegment(sketch, "E2.2.5.6", {"start": v(44.45, 133.35) * mm, "end": v(44.45, 120.65) * mm});
            skLineSegment(sketch, "E2.2.5.7", {"start": v(55.56, 131.76) * mm, "end": v(46.04, 131.76) * mm});
            skLineSegment(sketch, "E2.2.5.8", {"start": v(55.56, 131.76) * mm, "end": v(55.56, 122.24) * mm});
            skLineSegment(sketch, "E2.2.6.0", {"start": v(57.15, 146.05) * mm, "end": v(44.45, 146.05) * mm});
            skLineSegment(sketch, "E2.2.6.1", {"start": v(46.04, 157.16) * mm, "end": v(46.04, 147.64) * mm});
            skPoint(sketch, "E2.2.6.2", {"position": v(50.8, 152.4) * mm});
            skLineSegment(sketch, "E2.2.6.3", {"start": v(55.56, 147.64) * mm, "end": v(46.04, 147.64) * mm});
            skLineSegment(sketch, "E2.2.6.4", {"start": v(57.15, 158.75) * mm, "end": v(57.15, 146.05) * mm});
            skLineSegment(sketch, "E2.2.6.5", {"start": v(57.15, 158.75) * mm, "end": v(44.45, 158.75) * mm});
            skLineSegment(sketch, "E2.2.6.6", {"start": v(44.45, 158.75) * mm, "end": v(44.45, 146.05) * mm});
            skLineSegment(sketch, "E2.2.6.7", {"start": v(55.56, 157.16) * mm, "end": v(46.04, 157.16) * mm});
            skLineSegment(sketch, "E2.2.6.8", {"start": v(55.56, 157.16) * mm, "end": v(55.56, 147.64) * mm});
            skLineSegment(sketch, "E2.2.7.0", {"start": v(57.15, 171.45) * mm, "end": v(44.45, 171.45) * mm});
            skLineSegment(sketch, "E2.2.7.1", {"start": v(46.04, 182.56) * mm, "end": v(46.04, 173.04) * mm});
            skPoint(sketch, "E2.2.7.2", {"position": v(50.8, 177.8) * mm});
            skLineSegment(sketch, "E2.2.7.3", {"start": v(55.56, 173.04) * mm, "end": v(46.04, 173.04) * mm});
            skLineSegment(sketch, "E2.2.7.4", {"start": v(57.15, 184.15) * mm, "end": v(57.15, 171.45) * mm});
            skLineSegment(sketch, "E2.2.7.5", {"start": v(57.15, 184.15) * mm, "end": v(44.45, 184.15) * mm});
            skLineSegment(sketch, "E2.2.7.6", {"start": v(44.45, 184.15) * mm, "end": v(44.45, 171.45) * mm});
            skLineSegment(sketch, "E2.2.7.7", {"start": v(55.56, 182.56) * mm, "end": v(46.04, 182.56) * mm});
            skLineSegment(sketch, "E2.2.7.8", {"start": v(55.56, 182.56) * mm, "end": v(55.56, 173.04) * mm});
            skLineSegment(sketch, "E2.2.8.0", {"start": v(57.15, 196.85) * mm, "end": v(44.45, 196.85) * mm});
            skLineSegment(sketch, "E2.2.8.1", {"start": v(46.04, 207.96) * mm, "end": v(46.04, 198.44) * mm});
            skPoint(sketch, "E2.2.8.2", {"position": v(50.8, 203.2) * mm});
            skLineSegment(sketch, "E2.2.8.3", {"start": v(55.56, 198.44) * mm, "end": v(46.04, 198.44) * mm});
            skLineSegment(sketch, "E2.2.8.4", {"start": v(57.15, 209.55) * mm, "end": v(57.15, 196.85) * mm});
            skLineSegment(sketch, "E2.2.8.5", {"start": v(57.15, 209.55) * mm, "end": v(44.45, 209.55) * mm});
            skLineSegment(sketch, "E2.2.8.6", {"start": v(44.45, 209.55) * mm, "end": v(44.45, 196.85) * mm});
            skLineSegment(sketch, "E2.2.8.7", {"start": v(55.56, 207.96) * mm, "end": v(46.04, 207.96) * mm});
            skLineSegment(sketch, "E2.2.8.8", {"start": v(55.56, 207.96) * mm, "end": v(55.56, 198.44) * mm});
            skLineSegment(sketch, "E2.2.9.0", {"start": v(57.15, 222.25) * mm, "end": v(44.45, 222.25) * mm});
            skLineSegment(sketch, "E2.2.9.1", {"start": v(46.04, 233.36) * mm, "end": v(46.04, 223.84) * mm});
            skPoint(sketch, "E2.2.9.2", {"position": v(50.8, 228.6) * mm});
            skLineSegment(sketch, "E2.2.9.3", {"start": v(55.56, 223.84) * mm, "end": v(46.04, 223.84) * mm});
            skLineSegment(sketch, "E2.2.9.4", {"start": v(57.15, 234.95) * mm, "end": v(57.15, 222.25) * mm});
            skLineSegment(sketch, "E2.2.9.5", {"start": v(57.15, 234.95) * mm, "end": v(44.45, 234.95) * mm});
            skLineSegment(sketch, "E2.2.9.6", {"start": v(44.45, 234.95) * mm, "end": v(44.45, 222.25) * mm});
            skLineSegment(sketch, "E2.2.9.7", {"start": v(55.56, 233.36) * mm, "end": v(46.04, 233.36) * mm});
            skLineSegment(sketch, "E2.2.9.8", {"start": v(55.56, 233.36) * mm, "end": v(55.56, 223.84) * mm});
            skLineSegment(sketch, "E2.2.10.0", {"start": v(57.15, 247.65) * mm, "end": v(44.45, 247.65) * mm});
            skLineSegment(sketch, "E2.2.10.1", {"start": v(46.04, 258.76) * mm, "end": v(46.04, 249.24) * mm});
            skPoint(sketch, "E2.2.10.2", {"position": v(50.8, 254) * mm});
            skLineSegment(sketch, "E2.2.10.3", {"start": v(55.56, 249.24) * mm, "end": v(46.04, 249.24) * mm});
            skLineSegment(sketch, "E2.2.10.4", {"start": v(57.15, 260.35) * mm, "end": v(57.15, 247.65) * mm});
            skLineSegment(sketch, "E2.2.10.5", {"start": v(57.15, 260.35) * mm, "end": v(44.45, 260.35) * mm});
            skLineSegment(sketch, "E2.2.10.6", {"start": v(44.45, 260.35) * mm, "end": v(44.45, 247.65) * mm});
            skLineSegment(sketch, "E2.2.10.7", {"start": v(55.56, 258.76) * mm, "end": v(46.04, 258.76) * mm});
            skLineSegment(sketch, "E2.2.10.8", {"start": v(55.56, 258.76) * mm, "end": v(55.56, 249.24) * mm});
            skLineSegment(sketch, "E2.2.11.0", {"start": v(57.15, 273.05) * mm, "end": v(44.45, 273.05) * mm});
            skLineSegment(sketch, "E2.2.11.1", {"start": v(46.04, 284.16) * mm, "end": v(46.04, 274.64) * mm});
            skPoint(sketch, "E2.2.11.2", {"position": v(50.8, 279.4) * mm});
            skLineSegment(sketch, "E2.2.11.3", {"start": v(55.56, 274.64) * mm, "end": v(46.04, 274.64) * mm});
            skLineSegment(sketch, "E2.2.11.4", {"start": v(57.15, 285.75) * mm, "end": v(57.15, 273.05) * mm});
            skLineSegment(sketch, "E2.2.11.5", {"start": v(57.15, 285.75) * mm, "end": v(44.45, 285.75) * mm});
            skLineSegment(sketch, "E2.2.11.6", {"start": v(44.45, 285.75) * mm, "end": v(44.45, 273.05) * mm});
            skLineSegment(sketch, "E2.2.11.7", {"start": v(55.56, 284.16) * mm, "end": v(46.04, 284.16) * mm});
            skLineSegment(sketch, "E2.2.11.8", {"start": v(55.56, 284.16) * mm, "end": v(55.56, 274.64) * mm});
            skLineSegment(sketch, "E2.2.12.0", {"start": v(57.15, 298.45) * mm, "end": v(44.45, 298.45) * mm});
            skLineSegment(sketch, "E2.2.12.1", {"start": v(46.04, 309.56) * mm, "end": v(46.04, 300.04) * mm});
            skPoint(sketch, "E2.2.12.2", {"position": v(50.8, 304.8) * mm});
            skLineSegment(sketch, "E2.2.12.3", {"start": v(55.56, 300.04) * mm, "end": v(46.04, 300.04) * mm});
            skLineSegment(sketch, "E2.2.12.4", {"start": v(57.15, 311.15) * mm, "end": v(57.15, 298.45) * mm});
            skLineSegment(sketch, "E2.2.12.5", {"start": v(57.15, 311.15) * mm, "end": v(44.45, 311.15) * mm});
            skLineSegment(sketch, "E2.2.12.6", {"start": v(44.45, 311.15) * mm, "end": v(44.45, 298.45) * mm});
            skLineSegment(sketch, "E2.2.12.7", {"start": v(55.56, 309.56) * mm, "end": v(46.04, 309.56) * mm});
            skLineSegment(sketch, "E2.2.12.8", {"start": v(55.56, 309.56) * mm, "end": v(55.56, 300.04) * mm});
            skLineSegment(sketch, "E2.2.13.0", {"start": v(57.15, 323.85) * mm, "end": v(44.45, 323.85) * mm});
            skLineSegment(sketch, "E2.2.13.1", {"start": v(46.04, 334.96) * mm, "end": v(46.04, 325.44) * mm});
            skPoint(sketch, "E2.2.13.2", {"position": v(50.8, 330.2) * mm});
            skLineSegment(sketch, "E2.2.13.3", {"start": v(55.56, 325.44) * mm, "end": v(46.04, 325.44) * mm});
            skLineSegment(sketch, "E2.2.13.4", {"start": v(57.15, 336.55) * mm, "end": v(57.15, 323.85) * mm});
            skLineSegment(sketch, "E2.2.13.5", {"start": v(57.15, 336.55) * mm, "end": v(44.45, 336.55) * mm});
            skLineSegment(sketch, "E2.2.13.6", {"start": v(44.45, 336.55) * mm, "end": v(44.45, 323.85) * mm});
            skLineSegment(sketch, "E2.2.13.7", {"start": v(55.56, 334.96) * mm, "end": v(46.04, 334.96) * mm});
            skLineSegment(sketch, "E2.2.13.8", {"start": v(55.56, 334.96) * mm, "end": v(55.56, 325.44) * mm});
            skLineSegment(sketch, "E2.2.14.0", {"start": v(57.15, 349.25) * mm, "end": v(44.45, 349.25) * mm});
            skLineSegment(sketch, "E2.2.14.1", {"start": v(46.04, 360.36) * mm, "end": v(46.04, 350.84) * mm});
            skPoint(sketch, "E2.2.14.2", {"position": v(50.8, 355.6) * mm});
            skLineSegment(sketch, "E2.2.14.3", {"start": v(55.56, 350.84) * mm, "end": v(46.04, 350.84) * mm});
            skLineSegment(sketch, "E2.2.14.4", {"start": v(57.15, 361.95) * mm, "end": v(57.15, 349.25) * mm});
            skLineSegment(sketch, "E2.2.14.5", {"start": v(57.15, 361.95) * mm, "end": v(44.45, 361.95) * mm});
            skLineSegment(sketch, "E2.2.14.6", {"start": v(44.45, 361.95) * mm, "end": v(44.45, 349.25) * mm});
            skLineSegment(sketch, "E2.2.14.7", {"start": v(55.56, 360.36) * mm, "end": v(46.04, 360.36) * mm});
            skLineSegment(sketch, "E2.2.14.8", {"start": v(55.56, 360.36) * mm, "end": v(55.56, 350.84) * mm});
            skLineSegment(sketch, "E2.3.0.0", {"start": v(82.55, -6.35) * mm, "end": v(69.85, -6.35) * mm});
            skLineSegment(sketch, "E2.3.0.1", {"start": v(71.44, 4.76) * mm, "end": v(71.44, -4.76) * mm});
            skPoint(sketch, "E2.3.0.2", {"position": v(76.2, 0) * mm});
            skLineSegment(sketch, "E2.3.0.3", {"start": v(80.96, -4.76) * mm, "end": v(71.44, -4.76) * mm});
            skLineSegment(sketch, "E2.3.0.4", {"start": v(82.55, 6.35) * mm, "end": v(82.55, -6.35) * mm});
            skLineSegment(sketch, "E2.3.0.5", {"start": v(82.55, 6.35) * mm, "end": v(69.85, 6.35) * mm});
            skLineSegment(sketch, "E2.3.0.6", {"start": v(69.85, 6.35) * mm, "end": v(69.85, -6.35) * mm});
            skLineSegment(sketch, "E2.3.0.7", {"start": v(80.96, 4.76) * mm, "end": v(71.44, 4.76) * mm});
            skLineSegment(sketch, "E2.3.0.8", {"start": v(80.96, 4.76) * mm, "end": v(80.96, -4.76) * mm});
            skLineSegment(sketch, "E2.3.1.0", {"start": v(82.55, 19.05) * mm, "end": v(69.85, 19.05) * mm});
            skLineSegment(sketch, "E2.3.1.1", {"start": v(71.44, 30.16) * mm, "end": v(71.44, 20.64) * mm});
            skPoint(sketch, "E2.3.1.2", {"position": v(76.2, 25.4) * mm});
            skLineSegment(sketch, "E2.3.1.3", {"start": v(80.96, 20.64) * mm, "end": v(71.44, 20.64) * mm});
            skLineSegment(sketch, "E2.3.1.4", {"start": v(82.55, 31.75) * mm, "end": v(82.55, 19.05) * mm});
            skLineSegment(sketch, "E2.3.1.5", {"start": v(82.55, 31.75) * mm, "end": v(69.85, 31.75) * mm});
            skLineSegment(sketch, "E2.3.1.6", {"start": v(69.85, 31.75) * mm, "end": v(69.85, 19.05) * mm});
            skLineSegment(sketch, "E2.3.1.7", {"start": v(80.96, 30.16) * mm, "end": v(71.44, 30.16) * mm});
            skLineSegment(sketch, "E2.3.1.8", {"start": v(80.96, 30.16) * mm, "end": v(80.96, 20.64) * mm});
            skLineSegment(sketch, "E2.3.2.0", {"start": v(82.55, 44.45) * mm, "end": v(69.85, 44.45) * mm});
            skLineSegment(sketch, "E2.3.2.1", {"start": v(71.44, 55.56) * mm, "end": v(71.44, 46.04) * mm});
            skPoint(sketch, "E2.3.2.2", {"position": v(76.2, 50.8) * mm});
            skLineSegment(sketch, "E2.3.2.3", {"start": v(80.96, 46.04) * mm, "end": v(71.44, 46.04) * mm});
            skLineSegment(sketch, "E2.3.2.4", {"start": v(82.55, 57.15) * mm, "end": v(82.55, 44.45) * mm});
            skLineSegment(sketch, "E2.3.2.5", {"start": v(82.55, 57.15) * mm, "end": v(69.85, 57.15) * mm});
            skLineSegment(sketch, "E2.3.2.6", {"start": v(69.85, 57.15) * mm, "end": v(69.85, 44.45) * mm});
            skLineSegment(sketch, "E2.3.2.7", {"start": v(80.96, 55.56) * mm, "end": v(71.44, 55.56) * mm});
            skLineSegment(sketch, "E2.3.2.8", {"start": v(80.96, 55.56) * mm, "end": v(80.96, 46.04) * mm});
            skLineSegment(sketch, "E2.3.3.0", {"start": v(82.55, 69.85) * mm, "end": v(69.85, 69.85) * mm});
            skLineSegment(sketch, "E2.3.3.1", {"start": v(71.44, 80.96) * mm, "end": v(71.44, 71.44) * mm});
            skPoint(sketch, "E2.3.3.2", {"position": v(76.2, 76.2) * mm});
            skLineSegment(sketch, "E2.3.3.3", {"start": v(80.96, 71.44) * mm, "end": v(71.44, 71.44) * mm});
            skLineSegment(sketch, "E2.3.3.4", {"start": v(82.55, 82.55) * mm, "end": v(82.55, 69.85) * mm});
            skLineSegment(sketch, "E2.3.3.5", {"start": v(82.55, 82.55) * mm, "end": v(69.85, 82.55) * mm});
            skLineSegment(sketch, "E2.3.3.6", {"start": v(69.85, 82.55) * mm, "end": v(69.85, 69.85) * mm});
            skLineSegment(sketch, "E2.3.3.7", {"start": v(80.96, 80.96) * mm, "end": v(71.44, 80.96) * mm});
            skLineSegment(sketch, "E2.3.3.8", {"start": v(80.96, 80.96) * mm, "end": v(80.96, 71.44) * mm});
            skLineSegment(sketch, "E2.3.4.0", {"start": v(82.55, 95.25) * mm, "end": v(69.85, 95.25) * mm});
            skLineSegment(sketch, "E2.3.4.1", {"start": v(71.44, 106.36) * mm, "end": v(71.44, 96.84) * mm});
            skPoint(sketch, "E2.3.4.2", {"position": v(76.2, 101.6) * mm});
            skLineSegment(sketch, "E2.3.4.3", {"start": v(80.96, 96.84) * mm, "end": v(71.44, 96.84) * mm});
            skLineSegment(sketch, "E2.3.4.4", {"start": v(82.55, 107.95) * mm, "end": v(82.55, 95.25) * mm});
            skLineSegment(sketch, "E2.3.4.5", {"start": v(82.55, 107.95) * mm, "end": v(69.85, 107.95) * mm});
            skLineSegment(sketch, "E2.3.4.6", {"start": v(69.85, 107.95) * mm, "end": v(69.85, 95.25) * mm});
            skLineSegment(sketch, "E2.3.4.7", {"start": v(80.96, 106.36) * mm, "end": v(71.44, 106.36) * mm});
            skLineSegment(sketch, "E2.3.4.8", {"start": v(80.96, 106.36) * mm, "end": v(80.96, 96.84) * mm});
            skLineSegment(sketch, "E2.3.5.0", {"start": v(82.55, 120.65) * mm, "end": v(69.85, 120.65) * mm});
            skLineSegment(sketch, "E2.3.5.1", {"start": v(71.44, 131.76) * mm, "end": v(71.44, 122.24) * mm});
            skPoint(sketch, "E2.3.5.2", {"position": v(76.2, 127) * mm});
            skLineSegment(sketch, "E2.3.5.3", {"start": v(80.96, 122.24) * mm, "end": v(71.44, 122.24) * mm});
            skLineSegment(sketch, "E2.3.5.4", {"start": v(82.55, 133.35) * mm, "end": v(82.55, 120.65) * mm});
            skLineSegment(sketch, "E2.3.5.5", {"start": v(82.55, 133.35) * mm, "end": v(69.85, 133.35) * mm});
            skLineSegment(sketch, "E2.3.5.6", {"start": v(69.85, 133.35) * mm, "end": v(69.85, 120.65) * mm});
            skLineSegment(sketch, "E2.3.5.7", {"start": v(80.96, 131.76) * mm, "end": v(71.44, 131.76) * mm});
            skLineSegment(sketch, "E2.3.5.8", {"start": v(80.96, 131.76) * mm, "end": v(80.96, 122.24) * mm});
            skLineSegment(sketch, "E2.3.6.0", {"start": v(82.55, 146.05) * mm, "end": v(69.85, 146.05) * mm});
            skLineSegment(sketch, "E2.3.6.1", {"start": v(71.44, 157.16) * mm, "end": v(71.44, 147.64) * mm});
            skPoint(sketch, "E2.3.6.2", {"position": v(76.2, 152.4) * mm});
            skLineSegment(sketch, "E2.3.6.3", {"start": v(80.96, 147.64) * mm, "end": v(71.44, 147.64) * mm});
            skLineSegment(sketch, "E2.3.6.4", {"start": v(82.55, 158.75) * mm, "end": v(82.55, 146.05) * mm});
            skLineSegment(sketch, "E2.3.6.5", {"start": v(82.55, 158.75) * mm, "end": v(69.85, 158.75) * mm});
            skLineSegment(sketch, "E2.3.6.6", {"start": v(69.85, 158.75) * mm, "end": v(69.85, 146.05) * mm});
            skLineSegment(sketch, "E2.3.6.7", {"start": v(80.96, 157.16) * mm, "end": v(71.44, 157.16) * mm});
            skLineSegment(sketch, "E2.3.6.8", {"start": v(80.96, 157.16) * mm, "end": v(80.96, 147.64) * mm});
            skLineSegment(sketch, "E2.3.7.0", {"start": v(82.55, 171.45) * mm, "end": v(69.85, 171.45) * mm});
            skLineSegment(sketch, "E2.3.7.1", {"start": v(71.44, 182.56) * mm, "end": v(71.44, 173.04) * mm});
            skPoint(sketch, "E2.3.7.2", {"position": v(76.2, 177.8) * mm});
            skLineSegment(sketch, "E2.3.7.3", {"start": v(80.96, 173.04) * mm, "end": v(71.44, 173.04) * mm});
            skLineSegment(sketch, "E2.3.7.4", {"start": v(82.55, 184.15) * mm, "end": v(82.55, 171.45) * mm});
            skLineSegment(sketch, "E2.3.7.5", {"start": v(82.55, 184.15) * mm, "end": v(69.85, 184.15) * mm});
            skLineSegment(sketch, "E2.3.7.6", {"start": v(69.85, 184.15) * mm, "end": v(69.85, 171.45) * mm});
            skLineSegment(sketch, "E2.3.7.7", {"start": v(80.96, 182.56) * mm, "end": v(71.44, 182.56) * mm});
            skLineSegment(sketch, "E2.3.7.8", {"start": v(80.96, 182.56) * mm, "end": v(80.96, 173.04) * mm});
            skLineSegment(sketch, "E2.3.8.0", {"start": v(82.55, 196.85) * mm, "end": v(69.85, 196.85) * mm});
            skLineSegment(sketch, "E2.3.8.1", {"start": v(71.44, 207.96) * mm, "end": v(71.44, 198.44) * mm});
            skPoint(sketch, "E2.3.8.2", {"position": v(76.2, 203.2) * mm});
            skLineSegment(sketch, "E2.3.8.3", {"start": v(80.96, 198.44) * mm, "end": v(71.44, 198.44) * mm});
            skLineSegment(sketch, "E2.3.8.4", {"start": v(82.55, 209.55) * mm, "end": v(82.55, 196.85) * mm});
            skLineSegment(sketch, "E2.3.8.5", {"start": v(82.55, 209.55) * mm, "end": v(69.85, 209.55) * mm});
            skLineSegment(sketch, "E2.3.8.6", {"start": v(69.85, 209.55) * mm, "end": v(69.85, 196.85) * mm});
            skLineSegment(sketch, "E2.3.8.7", {"start": v(80.96, 207.96) * mm, "end": v(71.44, 207.96) * mm});
            skLineSegment(sketch, "E2.3.8.8", {"start": v(80.96, 207.96) * mm, "end": v(80.96, 198.44) * mm});
            skLineSegment(sketch, "E2.3.9.0", {"start": v(82.55, 222.25) * mm, "end": v(69.85, 222.25) * mm});
            skLineSegment(sketch, "E2.3.9.1", {"start": v(71.44, 233.36) * mm, "end": v(71.44, 223.84) * mm});
            skPoint(sketch, "E2.3.9.2", {"position": v(76.2, 228.6) * mm});
            skLineSegment(sketch, "E2.3.9.3", {"start": v(80.96, 223.84) * mm, "end": v(71.44, 223.84) * mm});
            skLineSegment(sketch, "E2.3.9.4", {"start": v(82.55, 234.95) * mm, "end": v(82.55, 222.25) * mm});
            skLineSegment(sketch, "E2.3.9.5", {"start": v(82.55, 234.95) * mm, "end": v(69.85, 234.95) * mm});
            skLineSegment(sketch, "E2.3.9.6", {"start": v(69.85, 234.95) * mm, "end": v(69.85, 222.25) * mm});
            skLineSegment(sketch, "E2.3.9.7", {"start": v(80.96, 233.36) * mm, "end": v(71.44, 233.36) * mm});
            skLineSegment(sketch, "E2.3.9.8", {"start": v(80.96, 233.36) * mm, "end": v(80.96, 223.84) * mm});
            skLineSegment(sketch, "E2.3.10.0", {"start": v(82.55, 247.65) * mm, "end": v(69.85, 247.65) * mm});
            skLineSegment(sketch, "E2.3.10.1", {"start": v(71.44, 258.76) * mm, "end": v(71.44, 249.24) * mm});
            skPoint(sketch, "E2.3.10.2", {"position": v(76.2, 254) * mm});
            skLineSegment(sketch, "E2.3.10.3", {"start": v(80.96, 249.24) * mm, "end": v(71.44, 249.24) * mm});
            skLineSegment(sketch, "E2.3.10.4", {"start": v(82.55, 260.35) * mm, "end": v(82.55, 247.65) * mm});
            skLineSegment(sketch, "E2.3.10.5", {"start": v(82.55, 260.35) * mm, "end": v(69.85, 260.35) * mm});
            skLineSegment(sketch, "E2.3.10.6", {"start": v(69.85, 260.35) * mm, "end": v(69.85, 247.65) * mm});
            skLineSegment(sketch, "E2.3.10.7", {"start": v(80.96, 258.76) * mm, "end": v(71.44, 258.76) * mm});
            skLineSegment(sketch, "E2.3.10.8", {"start": v(80.96, 258.76) * mm, "end": v(80.96, 249.24) * mm});
            skLineSegment(sketch, "E2.3.11.0", {"start": v(82.55, 273.05) * mm, "end": v(69.85, 273.05) * mm});
            skLineSegment(sketch, "E2.3.11.1", {"start": v(71.44, 284.16) * mm, "end": v(71.44, 274.64) * mm});
            skPoint(sketch, "E2.3.11.2", {"position": v(76.2, 279.4) * mm});
            skLineSegment(sketch, "E2.3.11.3", {"start": v(80.96, 274.64) * mm, "end": v(71.44, 274.64) * mm});
            skLineSegment(sketch, "E2.3.11.4", {"start": v(82.55, 285.75) * mm, "end": v(82.55, 273.05) * mm});
            skLineSegment(sketch, "E2.3.11.5", {"start": v(82.55, 285.75) * mm, "end": v(69.85, 285.75) * mm});
            skLineSegment(sketch, "E2.3.11.6", {"start": v(69.85, 285.75) * mm, "end": v(69.85, 273.05) * mm});
            skLineSegment(sketch, "E2.3.11.7", {"start": v(80.96, 284.16) * mm, "end": v(71.44, 284.16) * mm});
            skLineSegment(sketch, "E2.3.11.8", {"start": v(80.96, 284.16) * mm, "end": v(80.96, 274.64) * mm});
            skLineSegment(sketch, "E2.3.12.0", {"start": v(82.55, 298.45) * mm, "end": v(69.85, 298.45) * mm});
            skLineSegment(sketch, "E2.3.12.1", {"start": v(71.44, 309.56) * mm, "end": v(71.44, 300.04) * mm});
            skPoint(sketch, "E2.3.12.2", {"position": v(76.2, 304.8) * mm});
            skLineSegment(sketch, "E2.3.12.3", {"start": v(80.96, 300.04) * mm, "end": v(71.44, 300.04) * mm});
            skLineSegment(sketch, "E2.3.12.4", {"start": v(82.55, 311.15) * mm, "end": v(82.55, 298.45) * mm});
            skLineSegment(sketch, "E2.3.12.5", {"start": v(82.55, 311.15) * mm, "end": v(69.85, 311.15) * mm});
            skLineSegment(sketch, "E2.3.12.6", {"start": v(69.85, 311.15) * mm, "end": v(69.85, 298.45) * mm});
            skLineSegment(sketch, "E2.3.12.7", {"start": v(80.96, 309.56) * mm, "end": v(71.44, 309.56) * mm});
            skLineSegment(sketch, "E2.3.12.8", {"start": v(80.96, 309.56) * mm, "end": v(80.96, 300.04) * mm});
            skLineSegment(sketch, "E2.3.13.0", {"start": v(82.55, 323.85) * mm, "end": v(69.85, 323.85) * mm});
            skLineSegment(sketch, "E2.3.13.1", {"start": v(71.44, 334.96) * mm, "end": v(71.44, 325.44) * mm});
            skPoint(sketch, "E2.3.13.2", {"position": v(76.2, 330.2) * mm});
            skLineSegment(sketch, "E2.3.13.3", {"start": v(80.96, 325.44) * mm, "end": v(71.44, 325.44) * mm});
            skLineSegment(sketch, "E2.3.13.4", {"start": v(82.55, 336.55) * mm, "end": v(82.55, 323.85) * mm});
            skLineSegment(sketch, "E2.3.13.5", {"start": v(82.55, 336.55) * mm, "end": v(69.85, 336.55) * mm});
            skLineSegment(sketch, "E2.3.13.6", {"start": v(69.85, 336.55) * mm, "end": v(69.85, 323.85) * mm});
            skLineSegment(sketch, "E2.3.13.7", {"start": v(80.96, 334.96) * mm, "end": v(71.44, 334.96) * mm});
            skLineSegment(sketch, "E2.3.13.8", {"start": v(80.96, 334.96) * mm, "end": v(80.96, 325.44) * mm});
            skLineSegment(sketch, "E2.3.14.0", {"start": v(82.55, 349.25) * mm, "end": v(69.85, 349.25) * mm});
            skLineSegment(sketch, "E2.3.14.1", {"start": v(71.44, 360.36) * mm, "end": v(71.44, 350.84) * mm});
            skPoint(sketch, "E2.3.14.2", {"position": v(76.2, 355.6) * mm});
            skLineSegment(sketch, "E2.3.14.3", {"start": v(80.96, 350.84) * mm, "end": v(71.44, 350.84) * mm});
            skLineSegment(sketch, "E2.3.14.4", {"start": v(82.55, 361.95) * mm, "end": v(82.55, 349.25) * mm});
            skLineSegment(sketch, "E2.3.14.5", {"start": v(82.55, 361.95) * mm, "end": v(69.85, 361.95) * mm});
            skLineSegment(sketch, "E2.3.14.6", {"start": v(69.85, 361.95) * mm, "end": v(69.85, 349.25) * mm});
            skLineSegment(sketch, "E2.3.14.7", {"start": v(80.96, 360.36) * mm, "end": v(71.44, 360.36) * mm});
            skLineSegment(sketch, "E2.3.14.8", {"start": v(80.96, 360.36) * mm, "end": v(80.96, 350.84) * mm});
            skLineSegment(sketch, "E2.4.0.0", {"start": v(107.95, -6.35) * mm, "end": v(95.25, -6.35) * mm});
            skLineSegment(sketch, "E2.4.0.1", {"start": v(96.84, 4.76) * mm, "end": v(96.84, -4.76) * mm});
            skPoint(sketch, "E2.4.0.2", {"position": v(101.6, 0) * mm});
            skLineSegment(sketch, "E2.4.0.3", {"start": v(106.36, -4.76) * mm, "end": v(96.84, -4.76) * mm});
            skLineSegment(sketch, "E2.4.0.4", {"start": v(107.95, 6.35) * mm, "end": v(107.95, -6.35) * mm});
            skLineSegment(sketch, "E2.4.0.5", {"start": v(107.95, 6.35) * mm, "end": v(95.25, 6.35) * mm});
            skLineSegment(sketch, "E2.4.0.6", {"start": v(95.25, 6.35) * mm, "end": v(95.25, -6.35) * mm});
            skLineSegment(sketch, "E2.4.0.7", {"start": v(106.36, 4.76) * mm, "end": v(96.84, 4.76) * mm});
            skLineSegment(sketch, "E2.4.0.8", {"start": v(106.36, 4.76) * mm, "end": v(106.36, -4.76) * mm});
            skLineSegment(sketch, "E2.4.1.0", {"start": v(107.95, 19.05) * mm, "end": v(95.25, 19.05) * mm});
            skLineSegment(sketch, "E2.4.1.1", {"start": v(96.84, 30.16) * mm, "end": v(96.84, 20.64) * mm});
            skPoint(sketch, "E2.4.1.2", {"position": v(101.6, 25.4) * mm});
            skLineSegment(sketch, "E2.4.1.3", {"start": v(106.36, 20.64) * mm, "end": v(96.84, 20.64) * mm});
            skLineSegment(sketch, "E2.4.1.4", {"start": v(107.95, 31.75) * mm, "end": v(107.95, 19.05) * mm});
            skLineSegment(sketch, "E2.4.1.5", {"start": v(107.95, 31.75) * mm, "end": v(95.25, 31.75) * mm});
            skLineSegment(sketch, "E2.4.1.6", {"start": v(95.25, 31.75) * mm, "end": v(95.25, 19.05) * mm});
            skLineSegment(sketch, "E2.4.1.7", {"start": v(106.36, 30.16) * mm, "end": v(96.84, 30.16) * mm});
            skLineSegment(sketch, "E2.4.1.8", {"start": v(106.36, 30.16) * mm, "end": v(106.36, 20.64) * mm});
            skLineSegment(sketch, "E2.4.2.0", {"start": v(107.95, 44.45) * mm, "end": v(95.25, 44.45) * mm});
            skLineSegment(sketch, "E2.4.2.1", {"start": v(96.84, 55.56) * mm, "end": v(96.84, 46.04) * mm});
            skPoint(sketch, "E2.4.2.2", {"position": v(101.6, 50.8) * mm});
            skLineSegment(sketch, "E2.4.2.3", {"start": v(106.36, 46.04) * mm, "end": v(96.84, 46.04) * mm});
            skLineSegment(sketch, "E2.4.2.4", {"start": v(107.95, 57.15) * mm, "end": v(107.95, 44.45) * mm});
            skLineSegment(sketch, "E2.4.2.5", {"start": v(107.95, 57.15) * mm, "end": v(95.25, 57.15) * mm});
            skLineSegment(sketch, "E2.4.2.6", {"start": v(95.25, 57.15) * mm, "end": v(95.25, 44.45) * mm});
            skLineSegment(sketch, "E2.4.2.7", {"start": v(106.36, 55.56) * mm, "end": v(96.84, 55.56) * mm});
            skLineSegment(sketch, "E2.4.2.8", {"start": v(106.36, 55.56) * mm, "end": v(106.36, 46.04) * mm});
            skLineSegment(sketch, "E2.4.3.0", {"start": v(107.95, 69.85) * mm, "end": v(95.25, 69.85) * mm});
            skLineSegment(sketch, "E2.4.3.1", {"start": v(96.84, 80.96) * mm, "end": v(96.84, 71.44) * mm});
            skPoint(sketch, "E2.4.3.2", {"position": v(101.6, 76.2) * mm});
            skLineSegment(sketch, "E2.4.3.3", {"start": v(106.36, 71.44) * mm, "end": v(96.84, 71.44) * mm});
            skLineSegment(sketch, "E2.4.3.4", {"start": v(107.95, 82.55) * mm, "end": v(107.95, 69.85) * mm});
            skLineSegment(sketch, "E2.4.3.5", {"start": v(107.95, 82.55) * mm, "end": v(95.25, 82.55) * mm});
            skLineSegment(sketch, "E2.4.3.6", {"start": v(95.25, 82.55) * mm, "end": v(95.25, 69.85) * mm});
            skLineSegment(sketch, "E2.4.3.7", {"start": v(106.36, 80.96) * mm, "end": v(96.84, 80.96) * mm});
            skLineSegment(sketch, "E2.4.3.8", {"start": v(106.36, 80.96) * mm, "end": v(106.36, 71.44) * mm});
            skLineSegment(sketch, "E2.4.4.0", {"start": v(107.95, 95.25) * mm, "end": v(95.25, 95.25) * mm});
            skLineSegment(sketch, "E2.4.4.1", {"start": v(96.84, 106.36) * mm, "end": v(96.84, 96.84) * mm});
            skPoint(sketch, "E2.4.4.2", {"position": v(101.6, 101.6) * mm});
            skLineSegment(sketch, "E2.4.4.3", {"start": v(106.36, 96.84) * mm, "end": v(96.84, 96.84) * mm});
            skLineSegment(sketch, "E2.4.4.4", {"start": v(107.95, 107.95) * mm, "end": v(107.95, 95.25) * mm});
            skLineSegment(sketch, "E2.4.4.5", {"start": v(107.95, 107.95) * mm, "end": v(95.25, 107.95) * mm});
            skLineSegment(sketch, "E2.4.4.6", {"start": v(95.25, 107.95) * mm, "end": v(95.25, 95.25) * mm});
            skLineSegment(sketch, "E2.4.4.7", {"start": v(106.36, 106.36) * mm, "end": v(96.84, 106.36) * mm});
            skLineSegment(sketch, "E2.4.4.8", {"start": v(106.36, 106.36) * mm, "end": v(106.36, 96.84) * mm});
            skLineSegment(sketch, "E2.4.5.0", {"start": v(107.95, 120.65) * mm, "end": v(95.25, 120.65) * mm});
            skLineSegment(sketch, "E2.4.5.1", {"start": v(96.84, 131.76) * mm, "end": v(96.84, 122.24) * mm});
            skPoint(sketch, "E2.4.5.2", {"position": v(101.6, 127) * mm});
            skLineSegment(sketch, "E2.4.5.3", {"start": v(106.36, 122.24) * mm, "end": v(96.84, 122.24) * mm});
            skLineSegment(sketch, "E2.4.5.4", {"start": v(107.95, 133.35) * mm, "end": v(107.95, 120.65) * mm});
            skLineSegment(sketch, "E2.4.5.5", {"start": v(107.95, 133.35) * mm, "end": v(95.25, 133.35) * mm});
            skLineSegment(sketch, "E2.4.5.6", {"start": v(95.25, 133.35) * mm, "end": v(95.25, 120.65) * mm});
            skLineSegment(sketch, "E2.4.5.7", {"start": v(106.36, 131.76) * mm, "end": v(96.84, 131.76) * mm});
            skLineSegment(sketch, "E2.4.5.8", {"start": v(106.36, 131.76) * mm, "end": v(106.36, 122.24) * mm});
            skLineSegment(sketch, "E2.4.6.0", {"start": v(107.95, 146.05) * mm, "end": v(95.25, 146.05) * mm});
            skLineSegment(sketch, "E2.4.6.1", {"start": v(96.84, 157.16) * mm, "end": v(96.84, 147.64) * mm});
            skPoint(sketch, "E2.4.6.2", {"position": v(101.6, 152.4) * mm});
            skLineSegment(sketch, "E2.4.6.3", {"start": v(106.36, 147.64) * mm, "end": v(96.84, 147.64) * mm});
            skLineSegment(sketch, "E2.4.6.4", {"start": v(107.95, 158.75) * mm, "end": v(107.95, 146.05) * mm});
            skLineSegment(sketch, "E2.4.6.5", {"start": v(107.95, 158.75) * mm, "end": v(95.25, 158.75) * mm});
            skLineSegment(sketch, "E2.4.6.6", {"start": v(95.25, 158.75) * mm, "end": v(95.25, 146.05) * mm});
            skLineSegment(sketch, "E2.4.6.7", {"start": v(106.36, 157.16) * mm, "end": v(96.84, 157.16) * mm});
            skLineSegment(sketch, "E2.4.6.8", {"start": v(106.36, 157.16) * mm, "end": v(106.36, 147.64) * mm});
            skLineSegment(sketch, "E2.4.7.0", {"start": v(107.95, 171.45) * mm, "end": v(95.25, 171.45) * mm});
            skLineSegment(sketch, "E2.4.7.1", {"start": v(96.84, 182.56) * mm, "end": v(96.84, 173.04) * mm});
            skPoint(sketch, "E2.4.7.2", {"position": v(101.6, 177.8) * mm});
            skLineSegment(sketch, "E2.4.7.3", {"start": v(106.36, 173.04) * mm, "end": v(96.84, 173.04) * mm});
            skLineSegment(sketch, "E2.4.7.4", {"start": v(107.95, 184.15) * mm, "end": v(107.95, 171.45) * mm});
            skLineSegment(sketch, "E2.4.7.5", {"start": v(107.95, 184.15) * mm, "end": v(95.25, 184.15) * mm});
            skLineSegment(sketch, "E2.4.7.6", {"start": v(95.25, 184.15) * mm, "end": v(95.25, 171.45) * mm});
            skLineSegment(sketch, "E2.4.7.7", {"start": v(106.36, 182.56) * mm, "end": v(96.84, 182.56) * mm});
            skLineSegment(sketch, "E2.4.7.8", {"start": v(106.36, 182.56) * mm, "end": v(106.36, 173.04) * mm});
            skLineSegment(sketch, "E2.4.8.0", {"start": v(107.95, 196.85) * mm, "end": v(95.25, 196.85) * mm});
            skLineSegment(sketch, "E2.4.8.1", {"start": v(96.84, 207.96) * mm, "end": v(96.84, 198.44) * mm});
            skPoint(sketch, "E2.4.8.2", {"position": v(101.6, 203.2) * mm});
            skLineSegment(sketch, "E2.4.8.3", {"start": v(106.36, 198.44) * mm, "end": v(96.84, 198.44) * mm});
            skLineSegment(sketch, "E2.4.8.4", {"start": v(107.95, 209.55) * mm, "end": v(107.95, 196.85) * mm});
            skLineSegment(sketch, "E2.4.8.5", {"start": v(107.95, 209.55) * mm, "end": v(95.25, 209.55) * mm});
            skLineSegment(sketch, "E2.4.8.6", {"start": v(95.25, 209.55) * mm, "end": v(95.25, 196.85) * mm});
            skLineSegment(sketch, "E2.4.8.7", {"start": v(106.36, 207.96) * mm, "end": v(96.84, 207.96) * mm});
            skLineSegment(sketch, "E2.4.8.8", {"start": v(106.36, 207.96) * mm, "end": v(106.36, 198.44) * mm});
            skLineSegment(sketch, "E2.4.9.0", {"start": v(107.95, 222.25) * mm, "end": v(95.25, 222.25) * mm});
            skLineSegment(sketch, "E2.4.9.1", {"start": v(96.84, 233.36) * mm, "end": v(96.84, 223.84) * mm});
            skPoint(sketch, "E2.4.9.2", {"position": v(101.6, 228.6) * mm});
            skLineSegment(sketch, "E2.4.9.3", {"start": v(106.36, 223.84) * mm, "end": v(96.84, 223.84) * mm});
            skLineSegment(sketch, "E2.4.9.4", {"start": v(107.95, 234.95) * mm, "end": v(107.95, 222.25) * mm});
            skLineSegment(sketch, "E2.4.9.5", {"start": v(107.95, 234.95) * mm, "end": v(95.25, 234.95) * mm});
            skLineSegment(sketch, "E2.4.9.6", {"start": v(95.25, 234.95) * mm, "end": v(95.25, 222.25) * mm});
            skLineSegment(sketch, "E2.4.9.7", {"start": v(106.36, 233.36) * mm, "end": v(96.84, 233.36) * mm});
            skLineSegment(sketch, "E2.4.9.8", {"start": v(106.36, 233.36) * mm, "end": v(106.36, 223.84) * mm});
            skLineSegment(sketch, "E2.4.10.0", {"start": v(107.95, 247.65) * mm, "end": v(95.25, 247.65) * mm});
            skLineSegment(sketch, "E2.4.10.1", {"start": v(96.84, 258.76) * mm, "end": v(96.84, 249.24) * mm});
            skPoint(sketch, "E2.4.10.2", {"position": v(101.6, 254) * mm});
            skLineSegment(sketch, "E2.4.10.3", {"start": v(106.36, 249.24) * mm, "end": v(96.84, 249.24) * mm});
            skLineSegment(sketch, "E2.4.10.4", {"start": v(107.95, 260.35) * mm, "end": v(107.95, 247.65) * mm});
            skLineSegment(sketch, "E2.4.10.5", {"start": v(107.95, 260.35) * mm, "end": v(95.25, 260.35) * mm});
            skLineSegment(sketch, "E2.4.10.6", {"start": v(95.25, 260.35) * mm, "end": v(95.25, 247.65) * mm});
            skLineSegment(sketch, "E2.4.10.7", {"start": v(106.36, 258.76) * mm, "end": v(96.84, 258.76) * mm});
            skLineSegment(sketch, "E2.4.10.8", {"start": v(106.36, 258.76) * mm, "end": v(106.36, 249.24) * mm});
            skLineSegment(sketch, "E2.4.11.0", {"start": v(107.95, 273.05) * mm, "end": v(95.25, 273.05) * mm});
            skLineSegment(sketch, "E2.4.11.1", {"start": v(96.84, 284.16) * mm, "end": v(96.84, 274.64) * mm});
            skPoint(sketch, "E2.4.11.2", {"position": v(101.6, 279.4) * mm});
            skLineSegment(sketch, "E2.4.11.3", {"start": v(106.36, 274.64) * mm, "end": v(96.84, 274.64) * mm});
            skLineSegment(sketch, "E2.4.11.4", {"start": v(107.95, 285.75) * mm, "end": v(107.95, 273.05) * mm});
            skLineSegment(sketch, "E2.4.11.5", {"start": v(107.95, 285.75) * mm, "end": v(95.25, 285.75) * mm});
            skLineSegment(sketch, "E2.4.11.6", {"start": v(95.25, 285.75) * mm, "end": v(95.25, 273.05) * mm});
            skLineSegment(sketch, "E2.4.11.7", {"start": v(106.36, 284.16) * mm, "end": v(96.84, 284.16) * mm});
            skLineSegment(sketch, "E2.4.11.8", {"start": v(106.36, 284.16) * mm, "end": v(106.36, 274.64) * mm});
            skLineSegment(sketch, "E2.4.12.0", {"start": v(107.95, 298.45) * mm, "end": v(95.25, 298.45) * mm});
            skLineSegment(sketch, "E2.4.12.1", {"start": v(96.84, 309.56) * mm, "end": v(96.84, 300.04) * mm});
            skPoint(sketch, "E2.4.12.2", {"position": v(101.6, 304.8) * mm});
            skLineSegment(sketch, "E2.4.12.3", {"start": v(106.36, 300.04) * mm, "end": v(96.84, 300.04) * mm});
            skLineSegment(sketch, "E2.4.12.4", {"start": v(107.95, 311.15) * mm, "end": v(107.95, 298.45) * mm});
            skLineSegment(sketch, "E2.4.12.5", {"start": v(107.95, 311.15) * mm, "end": v(95.25, 311.15) * mm});
            skLineSegment(sketch, "E2.4.12.6", {"start": v(95.25, 311.15) * mm, "end": v(95.25, 298.45) * mm});
            skLineSegment(sketch, "E2.4.12.7", {"start": v(106.36, 309.56) * mm, "end": v(96.84, 309.56) * mm});
            skLineSegment(sketch, "E2.4.12.8", {"start": v(106.36, 309.56) * mm, "end": v(106.36, 300.04) * mm});
            skLineSegment(sketch, "E2.4.13.0", {"start": v(107.95, 323.85) * mm, "end": v(95.25, 323.85) * mm});
            skLineSegment(sketch, "E2.4.13.1", {"start": v(96.84, 334.96) * mm, "end": v(96.84, 325.44) * mm});
            skPoint(sketch, "E2.4.13.2", {"position": v(101.6, 330.2) * mm});
            skLineSegment(sketch, "E2.4.13.3", {"start": v(106.36, 325.44) * mm, "end": v(96.84, 325.44) * mm});
            skLineSegment(sketch, "E2.4.13.4", {"start": v(107.95, 336.55) * mm, "end": v(107.95, 323.85) * mm});
            skLineSegment(sketch, "E2.4.13.5", {"start": v(107.95, 336.55) * mm, "end": v(95.25, 336.55) * mm});
            skLineSegment(sketch, "E2.4.13.6", {"start": v(95.25, 336.55) * mm, "end": v(95.25, 323.85) * mm});
            skLineSegment(sketch, "E2.4.13.7", {"start": v(106.36, 334.96) * mm, "end": v(96.84, 334.96) * mm});
            skLineSegment(sketch, "E2.4.13.8", {"start": v(106.36, 334.96) * mm, "end": v(106.36, 325.44) * mm});
            skLineSegment(sketch, "E2.4.14.0", {"start": v(107.95, 349.25) * mm, "end": v(95.25, 349.25) * mm});
            skLineSegment(sketch, "E2.4.14.1", {"start": v(96.84, 360.36) * mm, "end": v(96.84, 350.84) * mm});
            skPoint(sketch, "E2.4.14.2", {"position": v(101.6, 355.6) * mm});
            skLineSegment(sketch, "E2.4.14.3", {"start": v(106.36, 350.84) * mm, "end": v(96.84, 350.84) * mm});
            skLineSegment(sketch, "E2.4.14.4", {"start": v(107.95, 361.95) * mm, "end": v(107.95, 349.25) * mm});
            skLineSegment(sketch, "E2.4.14.5", {"start": v(107.95, 361.95) * mm, "end": v(95.25, 361.95) * mm});
            skLineSegment(sketch, "E2.4.14.6", {"start": v(95.25, 361.95) * mm, "end": v(95.25, 349.25) * mm});
            skLineSegment(sketch, "E2.4.14.7", {"start": v(106.36, 360.36) * mm, "end": v(96.84, 360.36) * mm});
            skLineSegment(sketch, "E2.4.14.8", {"start": v(106.36, 360.36) * mm, "end": v(106.36, 350.84) * mm});
            skLineSegment(sketch, "E2.5.0.0", {"start": v(133.35, -6.35) * mm, "end": v(120.65, -6.35) * mm});
            skLineSegment(sketch, "E2.5.0.1", {"start": v(122.24, 4.76) * mm, "end": v(122.24, -4.76) * mm});
            skPoint(sketch, "E2.5.0.2", {"position": v(127, 0) * mm});
            skLineSegment(sketch, "E2.5.0.3", {"start": v(131.76, -4.76) * mm, "end": v(122.24, -4.76) * mm});
            skLineSegment(sketch, "E2.5.0.4", {"start": v(133.35, 6.35) * mm, "end": v(133.35, -6.35) * mm});
            skLineSegment(sketch, "E2.5.0.5", {"start": v(133.35, 6.35) * mm, "end": v(120.65, 6.35) * mm});
            skLineSegment(sketch, "E2.5.0.6", {"start": v(120.65, 6.35) * mm, "end": v(120.65, -6.35) * mm});
            skLineSegment(sketch, "E2.5.0.7", {"start": v(131.76, 4.76) * mm, "end": v(122.24, 4.76) * mm});
            skLineSegment(sketch, "E2.5.0.8", {"start": v(131.76, 4.76) * mm, "end": v(131.76, -4.76) * mm});
            skLineSegment(sketch, "E2.5.1.0", {"start": v(133.35, 19.05) * mm, "end": v(120.65, 19.05) * mm});
            skLineSegment(sketch, "E2.5.1.1", {"start": v(122.24, 30.16) * mm, "end": v(122.24, 20.64) * mm});
            skPoint(sketch, "E2.5.1.2", {"position": v(127, 25.4) * mm});
            skLineSegment(sketch, "E2.5.1.3", {"start": v(131.76, 20.64) * mm, "end": v(122.24, 20.64) * mm});
            skLineSegment(sketch, "E2.5.1.4", {"start": v(133.35, 31.75) * mm, "end": v(133.35, 19.05) * mm});
            skLineSegment(sketch, "E2.5.1.5", {"start": v(133.35, 31.75) * mm, "end": v(120.65, 31.75) * mm});
            skLineSegment(sketch, "E2.5.1.6", {"start": v(120.65, 31.75) * mm, "end": v(120.65, 19.05) * mm});
            skLineSegment(sketch, "E2.5.1.7", {"start": v(131.76, 30.16) * mm, "end": v(122.24, 30.16) * mm});
            skLineSegment(sketch, "E2.5.1.8", {"start": v(131.76, 30.16) * mm, "end": v(131.76, 20.64) * mm});
            skLineSegment(sketch, "E2.5.2.0", {"start": v(133.35, 44.45) * mm, "end": v(120.65, 44.45) * mm});
            skLineSegment(sketch, "E2.5.2.1", {"start": v(122.24, 55.56) * mm, "end": v(122.24, 46.04) * mm});
            skPoint(sketch, "E2.5.2.2", {"position": v(127, 50.8) * mm});
            skLineSegment(sketch, "E2.5.2.3", {"start": v(131.76, 46.04) * mm, "end": v(122.24, 46.04) * mm});
            skLineSegment(sketch, "E2.5.2.4", {"start": v(133.35, 57.15) * mm, "end": v(133.35, 44.45) * mm});
            skLineSegment(sketch, "E2.5.2.5", {"start": v(133.35, 57.15) * mm, "end": v(120.65, 57.15) * mm});
            skLineSegment(sketch, "E2.5.2.6", {"start": v(120.65, 57.15) * mm, "end": v(120.65, 44.45) * mm});
            skLineSegment(sketch, "E2.5.2.7", {"start": v(131.76, 55.56) * mm, "end": v(122.24, 55.56) * mm});
            skLineSegment(sketch, "E2.5.2.8", {"start": v(131.76, 55.56) * mm, "end": v(131.76, 46.04) * mm});
            skLineSegment(sketch, "E2.5.3.0", {"start": v(133.35, 69.85) * mm, "end": v(120.65, 69.85) * mm});
            skLineSegment(sketch, "E2.5.3.1", {"start": v(122.24, 80.96) * mm, "end": v(122.24, 71.44) * mm});
            skPoint(sketch, "E2.5.3.2", {"position": v(127, 76.2) * mm});
            skLineSegment(sketch, "E2.5.3.3", {"start": v(131.76, 71.44) * mm, "end": v(122.24, 71.44) * mm});
            skLineSegment(sketch, "E2.5.3.4", {"start": v(133.35, 82.55) * mm, "end": v(133.35, 69.85) * mm});
            skLineSegment(sketch, "E2.5.3.5", {"start": v(133.35, 82.55) * mm, "end": v(120.65, 82.55) * mm});
            skLineSegment(sketch, "E2.5.3.6", {"start": v(120.65, 82.55) * mm, "end": v(120.65, 69.85) * mm});
            skLineSegment(sketch, "E2.5.3.7", {"start": v(131.76, 80.96) * mm, "end": v(122.24, 80.96) * mm});
            skLineSegment(sketch, "E2.5.3.8", {"start": v(131.76, 80.96) * mm, "end": v(131.76, 71.44) * mm});
            skLineSegment(sketch, "E2.5.4.0", {"start": v(133.35, 95.25) * mm, "end": v(120.65, 95.25) * mm});
            skLineSegment(sketch, "E2.5.4.1", {"start": v(122.24, 106.36) * mm, "end": v(122.24, 96.84) * mm});
            skPoint(sketch, "E2.5.4.2", {"position": v(127, 101.6) * mm});
            skLineSegment(sketch, "E2.5.4.3", {"start": v(131.76, 96.84) * mm, "end": v(122.24, 96.84) * mm});
            skLineSegment(sketch, "E2.5.4.4", {"start": v(133.35, 107.95) * mm, "end": v(133.35, 95.25) * mm});
            skLineSegment(sketch, "E2.5.4.5", {"start": v(133.35, 107.95) * mm, "end": v(120.65, 107.95) * mm});
            skLineSegment(sketch, "E2.5.4.6", {"start": v(120.65, 107.95) * mm, "end": v(120.65, 95.25) * mm});
            skLineSegment(sketch, "E2.5.4.7", {"start": v(131.76, 106.36) * mm, "end": v(122.24, 106.36) * mm});
            skLineSegment(sketch, "E2.5.4.8", {"start": v(131.76, 106.36) * mm, "end": v(131.76, 96.84) * mm});
            skLineSegment(sketch, "E2.5.5.0", {"start": v(133.35, 120.65) * mm, "end": v(120.65, 120.65) * mm});
            skLineSegment(sketch, "E2.5.5.1", {"start": v(122.24, 131.76) * mm, "end": v(122.24, 122.24) * mm});
            skPoint(sketch, "E2.5.5.2", {"position": v(127, 127) * mm});
            skLineSegment(sketch, "E2.5.5.3", {"start": v(131.76, 122.24) * mm, "end": v(122.24, 122.24) * mm});
            skLineSegment(sketch, "E2.5.5.4", {"start": v(133.35, 133.35) * mm, "end": v(133.35, 120.65) * mm});
            skLineSegment(sketch, "E2.5.5.5", {"start": v(133.35, 133.35) * mm, "end": v(120.65, 133.35) * mm});
            skLineSegment(sketch, "E2.5.5.6", {"start": v(120.65, 133.35) * mm, "end": v(120.65, 120.65) * mm});
            skLineSegment(sketch, "E2.5.5.7", {"start": v(131.76, 131.76) * mm, "end": v(122.24, 131.76) * mm});
            skLineSegment(sketch, "E2.5.5.8", {"start": v(131.76, 131.76) * mm, "end": v(131.76, 122.24) * mm});
            skLineSegment(sketch, "E2.5.6.0", {"start": v(133.35, 146.05) * mm, "end": v(120.65, 146.05) * mm});
            skLineSegment(sketch, "E2.5.6.1", {"start": v(122.24, 157.16) * mm, "end": v(122.24, 147.64) * mm});
            skPoint(sketch, "E2.5.6.2", {"position": v(127, 152.4) * mm});
            skLineSegment(sketch, "E2.5.6.3", {"start": v(131.76, 147.64) * mm, "end": v(122.24, 147.64) * mm});
            skLineSegment(sketch, "E2.5.6.4", {"start": v(133.35, 158.75) * mm, "end": v(133.35, 146.05) * mm});
            skLineSegment(sketch, "E2.5.6.5", {"start": v(133.35, 158.75) * mm, "end": v(120.65, 158.75) * mm});
            skLineSegment(sketch, "E2.5.6.6", {"start": v(120.65, 158.75) * mm, "end": v(120.65, 146.05) * mm});
            skLineSegment(sketch, "E2.5.6.7", {"start": v(131.76, 157.16) * mm, "end": v(122.24, 157.16) * mm});
            skLineSegment(sketch, "E2.5.6.8", {"start": v(131.76, 157.16) * mm, "end": v(131.76, 147.64) * mm});
            skLineSegment(sketch, "E2.5.7.0", {"start": v(133.35, 171.45) * mm, "end": v(120.65, 171.45) * mm});
            skLineSegment(sketch, "E2.5.7.1", {"start": v(122.24, 182.56) * mm, "end": v(122.24, 173.04) * mm});
            skPoint(sketch, "E2.5.7.2", {"position": v(127, 177.8) * mm});
            skLineSegment(sketch, "E2.5.7.3", {"start": v(131.76, 173.04) * mm, "end": v(122.24, 173.04) * mm});
            skLineSegment(sketch, "E2.5.7.4", {"start": v(133.35, 184.15) * mm, "end": v(133.35, 171.45) * mm});
            skLineSegment(sketch, "E2.5.7.5", {"start": v(133.35, 184.15) * mm, "end": v(120.65, 184.15) * mm});
            skLineSegment(sketch, "E2.5.7.6", {"start": v(120.65, 184.15) * mm, "end": v(120.65, 171.45) * mm});
            skLineSegment(sketch, "E2.5.7.7", {"start": v(131.76, 182.56) * mm, "end": v(122.24, 182.56) * mm});
            skLineSegment(sketch, "E2.5.7.8", {"start": v(131.76, 182.56) * mm, "end": v(131.76, 173.04) * mm});
            skLineSegment(sketch, "E2.5.8.0", {"start": v(133.35, 196.85) * mm, "end": v(120.65, 196.85) * mm});
            skLineSegment(sketch, "E2.5.8.1", {"start": v(122.24, 207.96) * mm, "end": v(122.24, 198.44) * mm});
            skPoint(sketch, "E2.5.8.2", {"position": v(127, 203.2) * mm});
            skLineSegment(sketch, "E2.5.8.3", {"start": v(131.76, 198.44) * mm, "end": v(122.24, 198.44) * mm});
            skLineSegment(sketch, "E2.5.8.4", {"start": v(133.35, 209.55) * mm, "end": v(133.35, 196.85) * mm});
            skLineSegment(sketch, "E2.5.8.5", {"start": v(133.35, 209.55) * mm, "end": v(120.65, 209.55) * mm});
            skLineSegment(sketch, "E2.5.8.6", {"start": v(120.65, 209.55) * mm, "end": v(120.65, 196.85) * mm});
            skLineSegment(sketch, "E2.5.8.7", {"start": v(131.76, 207.96) * mm, "end": v(122.24, 207.96) * mm});
            skLineSegment(sketch, "E2.5.8.8", {"start": v(131.76, 207.96) * mm, "end": v(131.76, 198.44) * mm});
            skLineSegment(sketch, "E2.5.9.0", {"start": v(133.35, 222.25) * mm, "end": v(120.65, 222.25) * mm});
            skLineSegment(sketch, "E2.5.9.1", {"start": v(122.24, 233.36) * mm, "end": v(122.24, 223.84) * mm});
            skPoint(sketch, "E2.5.9.2", {"position": v(127, 228.6) * mm});
            skLineSegment(sketch, "E2.5.9.3", {"start": v(131.76, 223.84) * mm, "end": v(122.24, 223.84) * mm});
            skLineSegment(sketch, "E2.5.9.4", {"start": v(133.35, 234.95) * mm, "end": v(133.35, 222.25) * mm});
            skLineSegment(sketch, "E2.5.9.5", {"start": v(133.35, 234.95) * mm, "end": v(120.65, 234.95) * mm});
            skLineSegment(sketch, "E2.5.9.6", {"start": v(120.65, 234.95) * mm, "end": v(120.65, 222.25) * mm});
            skLineSegment(sketch, "E2.5.9.7", {"start": v(131.76, 233.36) * mm, "end": v(122.24, 233.36) * mm});
            skLineSegment(sketch, "E2.5.9.8", {"start": v(131.76, 233.36) * mm, "end": v(131.76, 223.84) * mm});
            skLineSegment(sketch, "E2.5.10.0", {"start": v(133.35, 247.65) * mm, "end": v(120.65, 247.65) * mm});
            skLineSegment(sketch, "E2.5.10.1", {"start": v(122.24, 258.76) * mm, "end": v(122.24, 249.24) * mm});
            skPoint(sketch, "E2.5.10.2", {"position": v(127, 254) * mm});
            skLineSegment(sketch, "E2.5.10.3", {"start": v(131.76, 249.24) * mm, "end": v(122.24, 249.24) * mm});
            skLineSegment(sketch, "E2.5.10.4", {"start": v(133.35, 260.35) * mm, "end": v(133.35, 247.65) * mm});
            skLineSegment(sketch, "E2.5.10.5", {"start": v(133.35, 260.35) * mm, "end": v(120.65, 260.35) * mm});
            skLineSegment(sketch, "E2.5.10.6", {"start": v(120.65, 260.35) * mm, "end": v(120.65, 247.65) * mm});
            skLineSegment(sketch, "E2.5.10.7", {"start": v(131.76, 258.76) * mm, "end": v(122.24, 258.76) * mm});
            skLineSegment(sketch, "E2.5.10.8", {"start": v(131.76, 258.76) * mm, "end": v(131.76, 249.24) * mm});
            skLineSegment(sketch, "E2.5.11.0", {"start": v(133.35, 273.05) * mm, "end": v(120.65, 273.05) * mm});
            skLineSegment(sketch, "E2.5.11.1", {"start": v(122.24, 284.16) * mm, "end": v(122.24, 274.64) * mm});
            skPoint(sketch, "E2.5.11.2", {"position": v(127, 279.4) * mm});
            skLineSegment(sketch, "E2.5.11.3", {"start": v(131.76, 274.64) * mm, "end": v(122.24, 274.64) * mm});
            skLineSegment(sketch, "E2.5.11.4", {"start": v(133.35, 285.75) * mm, "end": v(133.35, 273.05) * mm});
            skLineSegment(sketch, "E2.5.11.5", {"start": v(133.35, 285.75) * mm, "end": v(120.65, 285.75) * mm});
            skLineSegment(sketch, "E2.5.11.6", {"start": v(120.65, 285.75) * mm, "end": v(120.65, 273.05) * mm});
            skLineSegment(sketch, "E2.5.11.7", {"start": v(131.76, 284.16) * mm, "end": v(122.24, 284.16) * mm});
            skLineSegment(sketch, "E2.5.11.8", {"start": v(131.76, 284.16) * mm, "end": v(131.76, 274.64) * mm});
            skLineSegment(sketch, "E2.5.12.0", {"start": v(133.35, 298.45) * mm, "end": v(120.65, 298.45) * mm});
            skLineSegment(sketch, "E2.5.12.1", {"start": v(122.24, 309.56) * mm, "end": v(122.24, 300.04) * mm});
            skPoint(sketch, "E2.5.12.2", {"position": v(127, 304.8) * mm});
            skLineSegment(sketch, "E2.5.12.3", {"start": v(131.76, 300.04) * mm, "end": v(122.24, 300.04) * mm});
            skLineSegment(sketch, "E2.5.12.4", {"start": v(133.35, 311.15) * mm, "end": v(133.35, 298.45) * mm});
            skLineSegment(sketch, "E2.5.12.5", {"start": v(133.35, 311.15) * mm, "end": v(120.65, 311.15) * mm});
            skLineSegment(sketch, "E2.5.12.6", {"start": v(120.65, 311.15) * mm, "end": v(120.65, 298.45) * mm});
            skLineSegment(sketch, "E2.5.12.7", {"start": v(131.76, 309.56) * mm, "end": v(122.24, 309.56) * mm});
            skLineSegment(sketch, "E2.5.12.8", {"start": v(131.76, 309.56) * mm, "end": v(131.76, 300.04) * mm});
            skLineSegment(sketch, "E2.5.13.0", {"start": v(133.35, 323.85) * mm, "end": v(120.65, 323.85) * mm});
            skLineSegment(sketch, "E2.5.13.1", {"start": v(122.24, 334.96) * mm, "end": v(122.24, 325.44) * mm});
            skPoint(sketch, "E2.5.13.2", {"position": v(127, 330.2) * mm});
            skLineSegment(sketch, "E2.5.13.3", {"start": v(131.76, 325.44) * mm, "end": v(122.24, 325.44) * mm});
            skLineSegment(sketch, "E2.5.13.4", {"start": v(133.35, 336.55) * mm, "end": v(133.35, 323.85) * mm});
            skLineSegment(sketch, "E2.5.13.5", {"start": v(133.35, 336.55) * mm, "end": v(120.65, 336.55) * mm});
            skLineSegment(sketch, "E2.5.13.6", {"start": v(120.65, 336.55) * mm, "end": v(120.65, 323.85) * mm});
            skLineSegment(sketch, "E2.5.13.7", {"start": v(131.76, 334.96) * mm, "end": v(122.24, 334.96) * mm});
            skLineSegment(sketch, "E2.5.13.8", {"start": v(131.76, 334.96) * mm, "end": v(131.76, 325.44) * mm});
            skLineSegment(sketch, "E2.5.14.0", {"start": v(133.35, 349.25) * mm, "end": v(120.65, 349.25) * mm});
            skLineSegment(sketch, "E2.5.14.1", {"start": v(122.24, 360.36) * mm, "end": v(122.24, 350.84) * mm});
            skPoint(sketch, "E2.5.14.2", {"position": v(127, 355.6) * mm});
            skLineSegment(sketch, "E2.5.14.3", {"start": v(131.76, 350.84) * mm, "end": v(122.24, 350.84) * mm});
            skLineSegment(sketch, "E2.5.14.4", {"start": v(133.35, 361.95) * mm, "end": v(133.35, 349.25) * mm});
            skLineSegment(sketch, "E2.5.14.5", {"start": v(133.35, 361.95) * mm, "end": v(120.65, 361.95) * mm});
            skLineSegment(sketch, "E2.5.14.6", {"start": v(120.65, 361.95) * mm, "end": v(120.65, 349.25) * mm});
            skLineSegment(sketch, "E2.5.14.7", {"start": v(131.76, 360.36) * mm, "end": v(122.24, 360.36) * mm});
            skLineSegment(sketch, "E2.5.14.8", {"start": v(131.76, 360.36) * mm, "end": v(131.76, 350.84) * mm});
            skLineSegment(sketch, "E2.6.0.0", {"start": v(158.75, -6.35) * mm, "end": v(146.05, -6.35) * mm});
            skLineSegment(sketch, "E2.6.0.1", {"start": v(147.64, 4.76) * mm, "end": v(147.64, -4.76) * mm});
            skPoint(sketch, "E2.6.0.2", {"position": v(152.4, 0) * mm});
            skLineSegment(sketch, "E2.6.0.3", {"start": v(157.16, -4.76) * mm, "end": v(147.64, -4.76) * mm});
            skLineSegment(sketch, "E2.6.0.4", {"start": v(158.75, 6.35) * mm, "end": v(158.75, -6.35) * mm});
            skLineSegment(sketch, "E2.6.0.5", {"start": v(158.75, 6.35) * mm, "end": v(146.05, 6.35) * mm});
            skLineSegment(sketch, "E2.6.0.6", {"start": v(146.05, 6.35) * mm, "end": v(146.05, -6.35) * mm});
            skLineSegment(sketch, "E2.6.0.7", {"start": v(157.16, 4.76) * mm, "end": v(147.64, 4.76) * mm});
            skLineSegment(sketch, "E2.6.0.8", {"start": v(157.16, 4.76) * mm, "end": v(157.16, -4.76) * mm});
            skLineSegment(sketch, "E2.6.1.0", {"start": v(158.75, 19.05) * mm, "end": v(146.05, 19.05) * mm});
            skLineSegment(sketch, "E2.6.1.1", {"start": v(147.64, 30.16) * mm, "end": v(147.64, 20.64) * mm});
            skPoint(sketch, "E2.6.1.2", {"position": v(152.4, 25.4) * mm});
            skLineSegment(sketch, "E2.6.1.3", {"start": v(157.16, 20.64) * mm, "end": v(147.64, 20.64) * mm});
            skLineSegment(sketch, "E2.6.1.4", {"start": v(158.75, 31.75) * mm, "end": v(158.75, 19.05) * mm});
            skLineSegment(sketch, "E2.6.1.5", {"start": v(158.75, 31.75) * mm, "end": v(146.05, 31.75) * mm});
            skLineSegment(sketch, "E2.6.1.6", {"start": v(146.05, 31.75) * mm, "end": v(146.05, 19.05) * mm});
            skLineSegment(sketch, "E2.6.1.7", {"start": v(157.16, 30.16) * mm, "end": v(147.64, 30.16) * mm});
            skLineSegment(sketch, "E2.6.1.8", {"start": v(157.16, 30.16) * mm, "end": v(157.16, 20.64) * mm});
            skLineSegment(sketch, "E2.6.2.0", {"start": v(158.75, 44.45) * mm, "end": v(146.05, 44.45) * mm});
            skLineSegment(sketch, "E2.6.2.1", {"start": v(147.64, 55.56) * mm, "end": v(147.64, 46.04) * mm});
            skPoint(sketch, "E2.6.2.2", {"position": v(152.4, 50.8) * mm});
            skLineSegment(sketch, "E2.6.2.3", {"start": v(157.16, 46.04) * mm, "end": v(147.64, 46.04) * mm});
            skLineSegment(sketch, "E2.6.2.4", {"start": v(158.75, 57.15) * mm, "end": v(158.75, 44.45) * mm});
            skLineSegment(sketch, "E2.6.2.5", {"start": v(158.75, 57.15) * mm, "end": v(146.05, 57.15) * mm});
            skLineSegment(sketch, "E2.6.2.6", {"start": v(146.05, 57.15) * mm, "end": v(146.05, 44.45) * mm});
            skLineSegment(sketch, "E2.6.2.7", {"start": v(157.16, 55.56) * mm, "end": v(147.64, 55.56) * mm});
            skLineSegment(sketch, "E2.6.2.8", {"start": v(157.16, 55.56) * mm, "end": v(157.16, 46.04) * mm});
            skLineSegment(sketch, "E2.6.3.0", {"start": v(158.75, 69.85) * mm, "end": v(146.05, 69.85) * mm});
            skLineSegment(sketch, "E2.6.3.1", {"start": v(147.64, 80.96) * mm, "end": v(147.64, 71.44) * mm});
            skPoint(sketch, "E2.6.3.2", {"position": v(152.4, 76.2) * mm});
            skLineSegment(sketch, "E2.6.3.3", {"start": v(157.16, 71.44) * mm, "end": v(147.64, 71.44) * mm});
            skLineSegment(sketch, "E2.6.3.4", {"start": v(158.75, 82.55) * mm, "end": v(158.75, 69.85) * mm});
            skLineSegment(sketch, "E2.6.3.5", {"start": v(158.75, 82.55) * mm, "end": v(146.05, 82.55) * mm});
            skLineSegment(sketch, "E2.6.3.6", {"start": v(146.05, 82.55) * mm, "end": v(146.05, 69.85) * mm});
            skLineSegment(sketch, "E2.6.3.7", {"start": v(157.16, 80.96) * mm, "end": v(147.64, 80.96) * mm});
            skLineSegment(sketch, "E2.6.3.8", {"start": v(157.16, 80.96) * mm, "end": v(157.16, 71.44) * mm});
            skLineSegment(sketch, "E2.6.4.0", {"start": v(158.75, 95.25) * mm, "end": v(146.05, 95.25) * mm});
            skLineSegment(sketch, "E2.6.4.1", {"start": v(147.64, 106.36) * mm, "end": v(147.64, 96.84) * mm});
            skPoint(sketch, "E2.6.4.2", {"position": v(152.4, 101.6) * mm});
            skLineSegment(sketch, "E2.6.4.3", {"start": v(157.16, 96.84) * mm, "end": v(147.64, 96.84) * mm});
            skLineSegment(sketch, "E2.6.4.4", {"start": v(158.75, 107.95) * mm, "end": v(158.75, 95.25) * mm});
            skLineSegment(sketch, "E2.6.4.5", {"start": v(158.75, 107.95) * mm, "end": v(146.05, 107.95) * mm});
            skLineSegment(sketch, "E2.6.4.6", {"start": v(146.05, 107.95) * mm, "end": v(146.05, 95.25) * mm});
            skLineSegment(sketch, "E2.6.4.7", {"start": v(157.16, 106.36) * mm, "end": v(147.64, 106.36) * mm});
            skLineSegment(sketch, "E2.6.4.8", {"start": v(157.16, 106.36) * mm, "end": v(157.16, 96.84) * mm});
            skLineSegment(sketch, "E2.6.5.0", {"start": v(158.75, 120.65) * mm, "end": v(146.05, 120.65) * mm});
            skLineSegment(sketch, "E2.6.5.1", {"start": v(147.64, 131.76) * mm, "end": v(147.64, 122.24) * mm});
            skPoint(sketch, "E2.6.5.2", {"position": v(152.4, 127) * mm});
            skLineSegment(sketch, "E2.6.5.3", {"start": v(157.16, 122.24) * mm, "end": v(147.64, 122.24) * mm});
            skLineSegment(sketch, "E2.6.5.4", {"start": v(158.75, 133.35) * mm, "end": v(158.75, 120.65) * mm});
            skLineSegment(sketch, "E2.6.5.5", {"start": v(158.75, 133.35) * mm, "end": v(146.05, 133.35) * mm});
            skLineSegment(sketch, "E2.6.5.6", {"start": v(146.05, 133.35) * mm, "end": v(146.05, 120.65) * mm});
            skLineSegment(sketch, "E2.6.5.7", {"start": v(157.16, 131.76) * mm, "end": v(147.64, 131.76) * mm});
            skLineSegment(sketch, "E2.6.5.8", {"start": v(157.16, 131.76) * mm, "end": v(157.16, 122.24) * mm});
            skLineSegment(sketch, "E2.6.6.0", {"start": v(158.75, 146.05) * mm, "end": v(146.05, 146.05) * mm});
            skLineSegment(sketch, "E2.6.6.1", {"start": v(147.64, 157.16) * mm, "end": v(147.64, 147.64) * mm});
            skPoint(sketch, "E2.6.6.2", {"position": v(152.4, 152.4) * mm});
            skLineSegment(sketch, "E2.6.6.3", {"start": v(157.16, 147.64) * mm, "end": v(147.64, 147.64) * mm});
            skLineSegment(sketch, "E2.6.6.4", {"start": v(158.75, 158.75) * mm, "end": v(158.75, 146.05) * mm});
            skLineSegment(sketch, "E2.6.6.5", {"start": v(158.75, 158.75) * mm, "end": v(146.05, 158.75) * mm});
            skLineSegment(sketch, "E2.6.6.6", {"start": v(146.05, 158.75) * mm, "end": v(146.05, 146.05) * mm});
            skLineSegment(sketch, "E2.6.6.7", {"start": v(157.16, 157.16) * mm, "end": v(147.64, 157.16) * mm});
            skLineSegment(sketch, "E2.6.6.8", {"start": v(157.16, 157.16) * mm, "end": v(157.16, 147.64) * mm});
            skLineSegment(sketch, "E2.6.7.0", {"start": v(158.75, 171.45) * mm, "end": v(146.05, 171.45) * mm});
            skLineSegment(sketch, "E2.6.7.1", {"start": v(147.64, 182.56) * mm, "end": v(147.64, 173.04) * mm});
            skPoint(sketch, "E2.6.7.2", {"position": v(152.4, 177.8) * mm});
            skLineSegment(sketch, "E2.6.7.3", {"start": v(157.16, 173.04) * mm, "end": v(147.64, 173.04) * mm});
            skLineSegment(sketch, "E2.6.7.4", {"start": v(158.75, 184.15) * mm, "end": v(158.75, 171.45) * mm});
            skLineSegment(sketch, "E2.6.7.5", {"start": v(158.75, 184.15) * mm, "end": v(146.05, 184.15) * mm});
            skLineSegment(sketch, "E2.6.7.6", {"start": v(146.05, 184.15) * mm, "end": v(146.05, 171.45) * mm});
            skLineSegment(sketch, "E2.6.7.7", {"start": v(157.16, 182.56) * mm, "end": v(147.64, 182.56) * mm});
            skLineSegment(sketch, "E2.6.7.8", {"start": v(157.16, 182.56) * mm, "end": v(157.16, 173.04) * mm});
            skLineSegment(sketch, "E2.6.8.0", {"start": v(158.75, 196.85) * mm, "end": v(146.05, 196.85) * mm});
            skLineSegment(sketch, "E2.6.8.1", {"start": v(147.64, 207.96) * mm, "end": v(147.64, 198.44) * mm});
            skPoint(sketch, "E2.6.8.2", {"position": v(152.4, 203.2) * mm});
            skLineSegment(sketch, "E2.6.8.3", {"start": v(157.16, 198.44) * mm, "end": v(147.64, 198.44) * mm});
            skLineSegment(sketch, "E2.6.8.4", {"start": v(158.75, 209.55) * mm, "end": v(158.75, 196.85) * mm});
            skLineSegment(sketch, "E2.6.8.5", {"start": v(158.75, 209.55) * mm, "end": v(146.05, 209.55) * mm});
            skLineSegment(sketch, "E2.6.8.6", {"start": v(146.05, 209.55) * mm, "end": v(146.05, 196.85) * mm});
            skLineSegment(sketch, "E2.6.8.7", {"start": v(157.16, 207.96) * mm, "end": v(147.64, 207.96) * mm});
            skLineSegment(sketch, "E2.6.8.8", {"start": v(157.16, 207.96) * mm, "end": v(157.16, 198.44) * mm});
            skLineSegment(sketch, "E2.6.9.0", {"start": v(158.75, 222.25) * mm, "end": v(146.05, 222.25) * mm});
            skLineSegment(sketch, "E2.6.9.1", {"start": v(147.64, 233.36) * mm, "end": v(147.64, 223.84) * mm});
            skPoint(sketch, "E2.6.9.2", {"position": v(152.4, 228.6) * mm});
            skLineSegment(sketch, "E2.6.9.3", {"start": v(157.16, 223.84) * mm, "end": v(147.64, 223.84) * mm});
            skLineSegment(sketch, "E2.6.9.4", {"start": v(158.75, 234.95) * mm, "end": v(158.75, 222.25) * mm});
            skLineSegment(sketch, "E2.6.9.5", {"start": v(158.75, 234.95) * mm, "end": v(146.05, 234.95) * mm});
            skLineSegment(sketch, "E2.6.9.6", {"start": v(146.05, 234.95) * mm, "end": v(146.05, 222.25) * mm});
            skLineSegment(sketch, "E2.6.9.7", {"start": v(157.16, 233.36) * mm, "end": v(147.64, 233.36) * mm});
            skLineSegment(sketch, "E2.6.9.8", {"start": v(157.16, 233.36) * mm, "end": v(157.16, 223.84) * mm});
            skLineSegment(sketch, "E2.6.10.0", {"start": v(158.75, 247.65) * mm, "end": v(146.05, 247.65) * mm});
            skLineSegment(sketch, "E2.6.10.1", {"start": v(147.64, 258.76) * mm, "end": v(147.64, 249.24) * mm});
            skPoint(sketch, "E2.6.10.2", {"position": v(152.4, 254) * mm});
            skLineSegment(sketch, "E2.6.10.3", {"start": v(157.16, 249.24) * mm, "end": v(147.64, 249.24) * mm});
            skLineSegment(sketch, "E2.6.10.4", {"start": v(158.75, 260.35) * mm, "end": v(158.75, 247.65) * mm});
            skLineSegment(sketch, "E2.6.10.5", {"start": v(158.75, 260.35) * mm, "end": v(146.05, 260.35) * mm});
            skLineSegment(sketch, "E2.6.10.6", {"start": v(146.05, 260.35) * mm, "end": v(146.05, 247.65) * mm});
            skLineSegment(sketch, "E2.6.10.7", {"start": v(157.16, 258.76) * mm, "end": v(147.64, 258.76) * mm});
            skLineSegment(sketch, "E2.6.10.8", {"start": v(157.16, 258.76) * mm, "end": v(157.16, 249.24) * mm});
            skLineSegment(sketch, "E2.6.11.0", {"start": v(158.75, 273.05) * mm, "end": v(146.05, 273.05) * mm});
            skLineSegment(sketch, "E2.6.11.1", {"start": v(147.64, 284.16) * mm, "end": v(147.64, 274.64) * mm});
            skPoint(sketch, "E2.6.11.2", {"position": v(152.4, 279.4) * mm});
            skLineSegment(sketch, "E2.6.11.3", {"start": v(157.16, 274.64) * mm, "end": v(147.64, 274.64) * mm});
            skLineSegment(sketch, "E2.6.11.4", {"start": v(158.75, 285.75) * mm, "end": v(158.75, 273.05) * mm});
            skLineSegment(sketch, "E2.6.11.5", {"start": v(158.75, 285.75) * mm, "end": v(146.05, 285.75) * mm});
            skLineSegment(sketch, "E2.6.11.6", {"start": v(146.05, 285.75) * mm, "end": v(146.05, 273.05) * mm});
            skLineSegment(sketch, "E2.6.11.7", {"start": v(157.16, 284.16) * mm, "end": v(147.64, 284.16) * mm});
            skLineSegment(sketch, "E2.6.11.8", {"start": v(157.16, 284.16) * mm, "end": v(157.16, 274.64) * mm});
            skLineSegment(sketch, "E2.6.12.0", {"start": v(158.75, 298.45) * mm, "end": v(146.05, 298.45) * mm});
            skLineSegment(sketch, "E2.6.12.1", {"start": v(147.64, 309.56) * mm, "end": v(147.64, 300.04) * mm});
            skPoint(sketch, "E2.6.12.2", {"position": v(152.4, 304.8) * mm});
            skLineSegment(sketch, "E2.6.12.3", {"start": v(157.16, 300.04) * mm, "end": v(147.64, 300.04) * mm});
            skLineSegment(sketch, "E2.6.12.4", {"start": v(158.75, 311.15) * mm, "end": v(158.75, 298.45) * mm});
            skLineSegment(sketch, "E2.6.12.5", {"start": v(158.75, 311.15) * mm, "end": v(146.05, 311.15) * mm});
            skLineSegment(sketch, "E2.6.12.6", {"start": v(146.05, 311.15) * mm, "end": v(146.05, 298.45) * mm});
            skLineSegment(sketch, "E2.6.12.7", {"start": v(157.16, 309.56) * mm, "end": v(147.64, 309.56) * mm});
            skLineSegment(sketch, "E2.6.12.8", {"start": v(157.16, 309.56) * mm, "end": v(157.16, 300.04) * mm});
            skLineSegment(sketch, "E2.6.13.0", {"start": v(158.75, 323.85) * mm, "end": v(146.05, 323.85) * mm});
            skLineSegment(sketch, "E2.6.13.1", {"start": v(147.64, 334.96) * mm, "end": v(147.64, 325.44) * mm});
            skPoint(sketch, "E2.6.13.2", {"position": v(152.4, 330.2) * mm});
            skLineSegment(sketch, "E2.6.13.3", {"start": v(157.16, 325.44) * mm, "end": v(147.64, 325.44) * mm});
            skLineSegment(sketch, "E2.6.13.4", {"start": v(158.75, 336.55) * mm, "end": v(158.75, 323.85) * mm});
            skLineSegment(sketch, "E2.6.13.5", {"start": v(158.75, 336.55) * mm, "end": v(146.05, 336.55) * mm});
            skLineSegment(sketch, "E2.6.13.6", {"start": v(146.05, 336.55) * mm, "end": v(146.05, 323.85) * mm});
            skLineSegment(sketch, "E2.6.13.7", {"start": v(157.16, 334.96) * mm, "end": v(147.64, 334.96) * mm});
            skLineSegment(sketch, "E2.6.13.8", {"start": v(157.16, 334.96) * mm, "end": v(157.16, 325.44) * mm});
            skLineSegment(sketch, "E2.6.14.0", {"start": v(158.75, 349.25) * mm, "end": v(146.05, 349.25) * mm});
            skLineSegment(sketch, "E2.6.14.1", {"start": v(147.64, 360.36) * mm, "end": v(147.64, 350.84) * mm});
            skPoint(sketch, "E2.6.14.2", {"position": v(152.4, 355.6) * mm});
            skLineSegment(sketch, "E2.6.14.3", {"start": v(157.16, 350.84) * mm, "end": v(147.64, 350.84) * mm});
            skLineSegment(sketch, "E2.6.14.4", {"start": v(158.75, 361.95) * mm, "end": v(158.75, 349.25) * mm});
            skLineSegment(sketch, "E2.6.14.5", {"start": v(158.75, 361.95) * mm, "end": v(146.05, 361.95) * mm});
            skLineSegment(sketch, "E2.6.14.6", {"start": v(146.05, 361.95) * mm, "end": v(146.05, 349.25) * mm});
            skLineSegment(sketch, "E2.6.14.7", {"start": v(157.16, 360.36) * mm, "end": v(147.64, 360.36) * mm});
            skLineSegment(sketch, "E2.6.14.8", {"start": v(157.16, 360.36) * mm, "end": v(157.16, 350.84) * mm});
            skLineSegment(sketch, "E2.7.0.0", {"start": v(184.15, -6.35) * mm, "end": v(171.45, -6.35) * mm});
            skLineSegment(sketch, "E2.7.0.1", {"start": v(173.04, 4.76) * mm, "end": v(173.04, -4.76) * mm});
            skPoint(sketch, "E2.7.0.2", {"position": v(177.8, 0) * mm});
            skLineSegment(sketch, "E2.7.0.3", {"start": v(182.56, -4.76) * mm, "end": v(173.04, -4.76) * mm});
            skLineSegment(sketch, "E2.7.0.4", {"start": v(184.15, 6.35) * mm, "end": v(184.15, -6.35) * mm});
            skLineSegment(sketch, "E2.7.0.5", {"start": v(184.15, 6.35) * mm, "end": v(171.45, 6.35) * mm});
            skLineSegment(sketch, "E2.7.0.6", {"start": v(171.45, 6.35) * mm, "end": v(171.45, -6.35) * mm});
            skLineSegment(sketch, "E2.7.0.7", {"start": v(182.56, 4.76) * mm, "end": v(173.04, 4.76) * mm});
            skLineSegment(sketch, "E2.7.0.8", {"start": v(182.56, 4.76) * mm, "end": v(182.56, -4.76) * mm});
            skLineSegment(sketch, "E2.7.1.0", {"start": v(184.15, 19.05) * mm, "end": v(171.45, 19.05) * mm});
            skLineSegment(sketch, "E2.7.1.1", {"start": v(173.04, 30.16) * mm, "end": v(173.04, 20.64) * mm});
            skPoint(sketch, "E2.7.1.2", {"position": v(177.8, 25.4) * mm});
            skLineSegment(sketch, "E2.7.1.3", {"start": v(182.56, 20.64) * mm, "end": v(173.04, 20.64) * mm});
            skLineSegment(sketch, "E2.7.1.4", {"start": v(184.15, 31.75) * mm, "end": v(184.15, 19.05) * mm});
            skLineSegment(sketch, "E2.7.1.5", {"start": v(184.15, 31.75) * mm, "end": v(171.45, 31.75) * mm});
            skLineSegment(sketch, "E2.7.1.6", {"start": v(171.45, 31.75) * mm, "end": v(171.45, 19.05) * mm});
            skLineSegment(sketch, "E2.7.1.7", {"start": v(182.56, 30.16) * mm, "end": v(173.04, 30.16) * mm});
            skLineSegment(sketch, "E2.7.1.8", {"start": v(182.56, 30.16) * mm, "end": v(182.56, 20.64) * mm});
            skLineSegment(sketch, "E2.7.2.0", {"start": v(184.15, 44.45) * mm, "end": v(171.45, 44.45) * mm});
            skLineSegment(sketch, "E2.7.2.1", {"start": v(173.04, 55.56) * mm, "end": v(173.04, 46.04) * mm});
            skPoint(sketch, "E2.7.2.2", {"position": v(177.8, 50.8) * mm});
            skLineSegment(sketch, "E2.7.2.3", {"start": v(182.56, 46.04) * mm, "end": v(173.04, 46.04) * mm});
            skLineSegment(sketch, "E2.7.2.4", {"start": v(184.15, 57.15) * mm, "end": v(184.15, 44.45) * mm});
            skLineSegment(sketch, "E2.7.2.5", {"start": v(184.15, 57.15) * mm, "end": v(171.45, 57.15) * mm});
            skLineSegment(sketch, "E2.7.2.6", {"start": v(171.45, 57.15) * mm, "end": v(171.45, 44.45) * mm});
            skLineSegment(sketch, "E2.7.2.7", {"start": v(182.56, 55.56) * mm, "end": v(173.04, 55.56) * mm});
            skLineSegment(sketch, "E2.7.2.8", {"start": v(182.56, 55.56) * mm, "end": v(182.56, 46.04) * mm});
            skLineSegment(sketch, "E2.7.3.0", {"start": v(184.15, 69.85) * mm, "end": v(171.45, 69.85) * mm});
            skLineSegment(sketch, "E2.7.3.1", {"start": v(173.04, 80.96) * mm, "end": v(173.04, 71.44) * mm});
            skPoint(sketch, "E2.7.3.2", {"position": v(177.8, 76.2) * mm});
            skLineSegment(sketch, "E2.7.3.3", {"start": v(182.56, 71.44) * mm, "end": v(173.04, 71.44) * mm});
            skLineSegment(sketch, "E2.7.3.4", {"start": v(184.15, 82.55) * mm, "end": v(184.15, 69.85) * mm});
            skLineSegment(sketch, "E2.7.3.5", {"start": v(184.15, 82.55) * mm, "end": v(171.45, 82.55) * mm});
            skLineSegment(sketch, "E2.7.3.6", {"start": v(171.45, 82.55) * mm, "end": v(171.45, 69.85) * mm});
            skLineSegment(sketch, "E2.7.3.7", {"start": v(182.56, 80.96) * mm, "end": v(173.04, 80.96) * mm});
            skLineSegment(sketch, "E2.7.3.8", {"start": v(182.56, 80.96) * mm, "end": v(182.56, 71.44) * mm});
            skLineSegment(sketch, "E2.7.4.0", {"start": v(184.15, 95.25) * mm, "end": v(171.45, 95.25) * mm});
            skLineSegment(sketch, "E2.7.4.1", {"start": v(173.04, 106.36) * mm, "end": v(173.04, 96.84) * mm});
            skPoint(sketch, "E2.7.4.2", {"position": v(177.8, 101.6) * mm});
            skLineSegment(sketch, "E2.7.4.3", {"start": v(182.56, 96.84) * mm, "end": v(173.04, 96.84) * mm});
            skLineSegment(sketch, "E2.7.4.4", {"start": v(184.15, 107.95) * mm, "end": v(184.15, 95.25) * mm});
            skLineSegment(sketch, "E2.7.4.5", {"start": v(184.15, 107.95) * mm, "end": v(171.45, 107.95) * mm});
            skLineSegment(sketch, "E2.7.4.6", {"start": v(171.45, 107.95) * mm, "end": v(171.45, 95.25) * mm});
            skLineSegment(sketch, "E2.7.4.7", {"start": v(182.56, 106.36) * mm, "end": v(173.04, 106.36) * mm});
            skLineSegment(sketch, "E2.7.4.8", {"start": v(182.56, 106.36) * mm, "end": v(182.56, 96.84) * mm});
            skLineSegment(sketch, "E2.7.5.0", {"start": v(184.15, 120.65) * mm, "end": v(171.45, 120.65) * mm});
            skLineSegment(sketch, "E2.7.5.1", {"start": v(173.04, 131.76) * mm, "end": v(173.04, 122.24) * mm});
            skPoint(sketch, "E2.7.5.2", {"position": v(177.8, 127) * mm});
            skLineSegment(sketch, "E2.7.5.3", {"start": v(182.56, 122.24) * mm, "end": v(173.04, 122.24) * mm});
            skLineSegment(sketch, "E2.7.5.4", {"start": v(184.15, 133.35) * mm, "end": v(184.15, 120.65) * mm});
            skLineSegment(sketch, "E2.7.5.5", {"start": v(184.15, 133.35) * mm, "end": v(171.45, 133.35) * mm});
            skLineSegment(sketch, "E2.7.5.6", {"start": v(171.45, 133.35) * mm, "end": v(171.45, 120.65) * mm});
            skLineSegment(sketch, "E2.7.5.7", {"start": v(182.56, 131.76) * mm, "end": v(173.04, 131.76) * mm});
            skLineSegment(sketch, "E2.7.5.8", {"start": v(182.56, 131.76) * mm, "end": v(182.56, 122.24) * mm});
            skLineSegment(sketch, "E2.7.6.0", {"start": v(184.15, 146.05) * mm, "end": v(171.45, 146.05) * mm});
            skLineSegment(sketch, "E2.7.6.1", {"start": v(173.04, 157.16) * mm, "end": v(173.04, 147.64) * mm});
            skPoint(sketch, "E2.7.6.2", {"position": v(177.8, 152.4) * mm});
            skLineSegment(sketch, "E2.7.6.3", {"start": v(182.56, 147.64) * mm, "end": v(173.04, 147.64) * mm});
            skLineSegment(sketch, "E2.7.6.4", {"start": v(184.15, 158.75) * mm, "end": v(184.15, 146.05) * mm});
            skLineSegment(sketch, "E2.7.6.5", {"start": v(184.15, 158.75) * mm, "end": v(171.45, 158.75) * mm});
            skLineSegment(sketch, "E2.7.6.6", {"start": v(171.45, 158.75) * mm, "end": v(171.45, 146.05) * mm});
            skLineSegment(sketch, "E2.7.6.7", {"start": v(182.56, 157.16) * mm, "end": v(173.04, 157.16) * mm});
            skLineSegment(sketch, "E2.7.6.8", {"start": v(182.56, 157.16) * mm, "end": v(182.56, 147.64) * mm});
            skLineSegment(sketch, "E2.7.7.0", {"start": v(184.15, 171.45) * mm, "end": v(171.45, 171.45) * mm});
            skLineSegment(sketch, "E2.7.7.1", {"start": v(173.04, 182.56) * mm, "end": v(173.04, 173.04) * mm});
            skPoint(sketch, "E2.7.7.2", {"position": v(177.8, 177.8) * mm});
            skLineSegment(sketch, "E2.7.7.3", {"start": v(182.56, 173.04) * mm, "end": v(173.04, 173.04) * mm});
            skLineSegment(sketch, "E2.7.7.4", {"start": v(184.15, 184.15) * mm, "end": v(184.15, 171.45) * mm});
            skLineSegment(sketch, "E2.7.7.5", {"start": v(184.15, 184.15) * mm, "end": v(171.45, 184.15) * mm});
            skLineSegment(sketch, "E2.7.7.6", {"start": v(171.45, 184.15) * mm, "end": v(171.45, 171.45) * mm});
            skLineSegment(sketch, "E2.7.7.7", {"start": v(182.56, 182.56) * mm, "end": v(173.04, 182.56) * mm});
            skLineSegment(sketch, "E2.7.7.8", {"start": v(182.56, 182.56) * mm, "end": v(182.56, 173.04) * mm});
            skLineSegment(sketch, "E2.7.8.0", {"start": v(184.15, 196.85) * mm, "end": v(171.45, 196.85) * mm});
            skLineSegment(sketch, "E2.7.8.1", {"start": v(173.04, 207.96) * mm, "end": v(173.04, 198.44) * mm});
            skPoint(sketch, "E2.7.8.2", {"position": v(177.8, 203.2) * mm});
            skLineSegment(sketch, "E2.7.8.3", {"start": v(182.56, 198.44) * mm, "end": v(173.04, 198.44) * mm});
            skLineSegment(sketch, "E2.7.8.4", {"start": v(184.15, 209.55) * mm, "end": v(184.15, 196.85) * mm});
            skLineSegment(sketch, "E2.7.8.5", {"start": v(184.15, 209.55) * mm, "end": v(171.45, 209.55) * mm});
            skLineSegment(sketch, "E2.7.8.6", {"start": v(171.45, 209.55) * mm, "end": v(171.45, 196.85) * mm});
            skLineSegment(sketch, "E2.7.8.7", {"start": v(182.56, 207.96) * mm, "end": v(173.04, 207.96) * mm});
            skLineSegment(sketch, "E2.7.8.8", {"start": v(182.56, 207.96) * mm, "end": v(182.56, 198.44) * mm});
            skLineSegment(sketch, "E2.7.9.0", {"start": v(184.15, 222.25) * mm, "end": v(171.45, 222.25) * mm});
            skLineSegment(sketch, "E2.7.9.1", {"start": v(173.04, 233.36) * mm, "end": v(173.04, 223.84) * mm});
            skPoint(sketch, "E2.7.9.2", {"position": v(177.8, 228.6) * mm});
            skLineSegment(sketch, "E2.7.9.3", {"start": v(182.56, 223.84) * mm, "end": v(173.04, 223.84) * mm});
            skLineSegment(sketch, "E2.7.9.4", {"start": v(184.15, 234.95) * mm, "end": v(184.15, 222.25) * mm});
            skLineSegment(sketch, "E2.7.9.5", {"start": v(184.15, 234.95) * mm, "end": v(171.45, 234.95) * mm});
            skLineSegment(sketch, "E2.7.9.6", {"start": v(171.45, 234.95) * mm, "end": v(171.45, 222.25) * mm});
            skLineSegment(sketch, "E2.7.9.7", {"start": v(182.56, 233.36) * mm, "end": v(173.04, 233.36) * mm});
            skLineSegment(sketch, "E2.7.9.8", {"start": v(182.56, 233.36) * mm, "end": v(182.56, 223.84) * mm});
            skLineSegment(sketch, "E2.7.10.0", {"start": v(184.15, 247.65) * mm, "end": v(171.45, 247.65) * mm});
            skLineSegment(sketch, "E2.7.10.1", {"start": v(173.04, 258.76) * mm, "end": v(173.04, 249.24) * mm});
            skPoint(sketch, "E2.7.10.2", {"position": v(177.8, 254) * mm});
            skLineSegment(sketch, "E2.7.10.3", {"start": v(182.56, 249.24) * mm, "end": v(173.04, 249.24) * mm});
            skLineSegment(sketch, "E2.7.10.4", {"start": v(184.15, 260.35) * mm, "end": v(184.15, 247.65) * mm});
            skLineSegment(sketch, "E2.7.10.5", {"start": v(184.15, 260.35) * mm, "end": v(171.45, 260.35) * mm});
            skLineSegment(sketch, "E2.7.10.6", {"start": v(171.45, 260.35) * mm, "end": v(171.45, 247.65) * mm});
            skLineSegment(sketch, "E2.7.10.7", {"start": v(182.56, 258.76) * mm, "end": v(173.04, 258.76) * mm});
            skLineSegment(sketch, "E2.7.10.8", {"start": v(182.56, 258.76) * mm, "end": v(182.56, 249.24) * mm});
            skLineSegment(sketch, "E2.7.11.0", {"start": v(184.15, 273.05) * mm, "end": v(171.45, 273.05) * mm});
            skLineSegment(sketch, "E2.7.11.1", {"start": v(173.04, 284.16) * mm, "end": v(173.04, 274.64) * mm});
            skPoint(sketch, "E2.7.11.2", {"position": v(177.8, 279.4) * mm});
            skLineSegment(sketch, "E2.7.11.3", {"start": v(182.56, 274.64) * mm, "end": v(173.04, 274.64) * mm});
            skLineSegment(sketch, "E2.7.11.4", {"start": v(184.15, 285.75) * mm, "end": v(184.15, 273.05) * mm});
            skLineSegment(sketch, "E2.7.11.5", {"start": v(184.15, 285.75) * mm, "end": v(171.45, 285.75) * mm});
            skLineSegment(sketch, "E2.7.11.6", {"start": v(171.45, 285.75) * mm, "end": v(171.45, 273.05) * mm});
            skLineSegment(sketch, "E2.7.11.7", {"start": v(182.56, 284.16) * mm, "end": v(173.04, 284.16) * mm});
            skLineSegment(sketch, "E2.7.11.8", {"start": v(182.56, 284.16) * mm, "end": v(182.56, 274.64) * mm});
            skLineSegment(sketch, "E2.7.12.0", {"start": v(184.15, 298.45) * mm, "end": v(171.45, 298.45) * mm});
            skLineSegment(sketch, "E2.7.12.1", {"start": v(173.04, 309.56) * mm, "end": v(173.04, 300.04) * mm});
            skPoint(sketch, "E2.7.12.2", {"position": v(177.8, 304.8) * mm});
            skLineSegment(sketch, "E2.7.12.3", {"start": v(182.56, 300.04) * mm, "end": v(173.04, 300.04) * mm});
            skLineSegment(sketch, "E2.7.12.4", {"start": v(184.15, 311.15) * mm, "end": v(184.15, 298.45) * mm});
            skLineSegment(sketch, "E2.7.12.5", {"start": v(184.15, 311.15) * mm, "end": v(171.45, 311.15) * mm});
            skLineSegment(sketch, "E2.7.12.6", {"start": v(171.45, 311.15) * mm, "end": v(171.45, 298.45) * mm});
            skLineSegment(sketch, "E2.7.12.7", {"start": v(182.56, 309.56) * mm, "end": v(173.04, 309.56) * mm});
            skLineSegment(sketch, "E2.7.12.8", {"start": v(182.56, 309.56) * mm, "end": v(182.56, 300.04) * mm});
            skLineSegment(sketch, "E2.7.13.0", {"start": v(184.15, 323.85) * mm, "end": v(171.45, 323.85) * mm});
            skLineSegment(sketch, "E2.7.13.1", {"start": v(173.04, 334.96) * mm, "end": v(173.04, 325.44) * mm});
            skPoint(sketch, "E2.7.13.2", {"position": v(177.8, 330.2) * mm});
            skLineSegment(sketch, "E2.7.13.3", {"start": v(182.56, 325.44) * mm, "end": v(173.04, 325.44) * mm});
            skLineSegment(sketch, "E2.7.13.4", {"start": v(184.15, 336.55) * mm, "end": v(184.15, 323.85) * mm});
            skLineSegment(sketch, "E2.7.13.5", {"start": v(184.15, 336.55) * mm, "end": v(171.45, 336.55) * mm});
            skLineSegment(sketch, "E2.7.13.6", {"start": v(171.45, 336.55) * mm, "end": v(171.45, 323.85) * mm});
            skLineSegment(sketch, "E2.7.13.7", {"start": v(182.56, 334.96) * mm, "end": v(173.04, 334.96) * mm});
            skLineSegment(sketch, "E2.7.13.8", {"start": v(182.56, 334.96) * mm, "end": v(182.56, 325.44) * mm});
            skLineSegment(sketch, "E2.7.14.0", {"start": v(184.15, 349.25) * mm, "end": v(171.45, 349.25) * mm});
            skLineSegment(sketch, "E2.7.14.1", {"start": v(173.04, 360.36) * mm, "end": v(173.04, 350.84) * mm});
            skPoint(sketch, "E2.7.14.2", {"position": v(177.8, 355.6) * mm});
            skLineSegment(sketch, "E2.7.14.3", {"start": v(182.56, 350.84) * mm, "end": v(173.04, 350.84) * mm});
            skLineSegment(sketch, "E2.7.14.4", {"start": v(184.15, 361.95) * mm, "end": v(184.15, 349.25) * mm});
            skLineSegment(sketch, "E2.7.14.5", {"start": v(184.15, 361.95) * mm, "end": v(171.45, 361.95) * mm});
            skLineSegment(sketch, "E2.7.14.6", {"start": v(171.45, 361.95) * mm, "end": v(171.45, 349.25) * mm});
            skLineSegment(sketch, "E2.7.14.7", {"start": v(182.56, 360.36) * mm, "end": v(173.04, 360.36) * mm});
            skLineSegment(sketch, "E2.7.14.8", {"start": v(182.56, 360.36) * mm, "end": v(182.56, 350.84) * mm});
            skLineSegment(sketch, "E2.8.0.0", {"start": v(209.55, -6.35) * mm, "end": v(196.85, -6.35) * mm});
            skLineSegment(sketch, "E2.8.0.1", {"start": v(198.44, 4.76) * mm, "end": v(198.44, -4.76) * mm});
            skPoint(sketch, "E2.8.0.2", {"position": v(203.2, 0) * mm});
            skLineSegment(sketch, "E2.8.0.3", {"start": v(207.96, -4.76) * mm, "end": v(198.44, -4.76) * mm});
            skLineSegment(sketch, "E2.8.0.4", {"start": v(209.55, 6.35) * mm, "end": v(209.55, -6.35) * mm});
            skLineSegment(sketch, "E2.8.0.5", {"start": v(209.55, 6.35) * mm, "end": v(196.85, 6.35) * mm});
            skLineSegment(sketch, "E2.8.0.6", {"start": v(196.85, 6.35) * mm, "end": v(196.85, -6.35) * mm});
            skLineSegment(sketch, "E2.8.0.7", {"start": v(207.96, 4.76) * mm, "end": v(198.44, 4.76) * mm});
            skLineSegment(sketch, "E2.8.0.8", {"start": v(207.96, 4.76) * mm, "end": v(207.96, -4.76) * mm});
            skLineSegment(sketch, "E2.8.1.0", {"start": v(209.55, 19.05) * mm, "end": v(196.85, 19.05) * mm});
            skLineSegment(sketch, "E2.8.1.1", {"start": v(198.44, 30.16) * mm, "end": v(198.44, 20.64) * mm});
            skPoint(sketch, "E2.8.1.2", {"position": v(203.2, 25.4) * mm});
            skLineSegment(sketch, "E2.8.1.3", {"start": v(207.96, 20.64) * mm, "end": v(198.44, 20.64) * mm});
            skLineSegment(sketch, "E2.8.1.4", {"start": v(209.55, 31.75) * mm, "end": v(209.55, 19.05) * mm});
            skLineSegment(sketch, "E2.8.1.5", {"start": v(209.55, 31.75) * mm, "end": v(196.85, 31.75) * mm});
            skLineSegment(sketch, "E2.8.1.6", {"start": v(196.85, 31.75) * mm, "end": v(196.85, 19.05) * mm});
            skLineSegment(sketch, "E2.8.1.7", {"start": v(207.96, 30.16) * mm, "end": v(198.44, 30.16) * mm});
            skLineSegment(sketch, "E2.8.1.8", {"start": v(207.96, 30.16) * mm, "end": v(207.96, 20.64) * mm});
            skLineSegment(sketch, "E2.8.2.0", {"start": v(209.55, 44.45) * mm, "end": v(196.85, 44.45) * mm});
            skLineSegment(sketch, "E2.8.2.1", {"start": v(198.44, 55.56) * mm, "end": v(198.44, 46.04) * mm});
            skPoint(sketch, "E2.8.2.2", {"position": v(203.2, 50.8) * mm});
            skLineSegment(sketch, "E2.8.2.3", {"start": v(207.96, 46.04) * mm, "end": v(198.44, 46.04) * mm});
            skLineSegment(sketch, "E2.8.2.4", {"start": v(209.55, 57.15) * mm, "end": v(209.55, 44.45) * mm});
            skLineSegment(sketch, "E2.8.2.5", {"start": v(209.55, 57.15) * mm, "end": v(196.85, 57.15) * mm});
            skLineSegment(sketch, "E2.8.2.6", {"start": v(196.85, 57.15) * mm, "end": v(196.85, 44.45) * mm});
            skLineSegment(sketch, "E2.8.2.7", {"start": v(207.96, 55.56) * mm, "end": v(198.44, 55.56) * mm});
            skLineSegment(sketch, "E2.8.2.8", {"start": v(207.96, 55.56) * mm, "end": v(207.96, 46.04) * mm});
            skLineSegment(sketch, "E2.8.3.0", {"start": v(209.55, 69.85) * mm, "end": v(196.85, 69.85) * mm});
            skLineSegment(sketch, "E2.8.3.1", {"start": v(198.44, 80.96) * mm, "end": v(198.44, 71.44) * mm});
            skPoint(sketch, "E2.8.3.2", {"position": v(203.2, 76.2) * mm});
            skLineSegment(sketch, "E2.8.3.3", {"start": v(207.96, 71.44) * mm, "end": v(198.44, 71.44) * mm});
            skLineSegment(sketch, "E2.8.3.4", {"start": v(209.55, 82.55) * mm, "end": v(209.55, 69.85) * mm});
            skLineSegment(sketch, "E2.8.3.5", {"start": v(209.55, 82.55) * mm, "end": v(196.85, 82.55) * mm});
            skLineSegment(sketch, "E2.8.3.6", {"start": v(196.85, 82.55) * mm, "end": v(196.85, 69.85) * mm});
            skLineSegment(sketch, "E2.8.3.7", {"start": v(207.96, 80.96) * mm, "end": v(198.44, 80.96) * mm});
            skLineSegment(sketch, "E2.8.3.8", {"start": v(207.96, 80.96) * mm, "end": v(207.96, 71.44) * mm});
            skLineSegment(sketch, "E2.8.4.0", {"start": v(209.55, 95.25) * mm, "end": v(196.85, 95.25) * mm});
            skLineSegment(sketch, "E2.8.4.1", {"start": v(198.44, 106.36) * mm, "end": v(198.44, 96.84) * mm});
            skPoint(sketch, "E2.8.4.2", {"position": v(203.2, 101.6) * mm});
            skLineSegment(sketch, "E2.8.4.3", {"start": v(207.96, 96.84) * mm, "end": v(198.44, 96.84) * mm});
            skLineSegment(sketch, "E2.8.4.4", {"start": v(209.55, 107.95) * mm, "end": v(209.55, 95.25) * mm});
            skLineSegment(sketch, "E2.8.4.5", {"start": v(209.55, 107.95) * mm, "end": v(196.85, 107.95) * mm});
            skLineSegment(sketch, "E2.8.4.6", {"start": v(196.85, 107.95) * mm, "end": v(196.85, 95.25) * mm});
            skLineSegment(sketch, "E2.8.4.7", {"start": v(207.96, 106.36) * mm, "end": v(198.44, 106.36) * mm});
            skLineSegment(sketch, "E2.8.4.8", {"start": v(207.96, 106.36) * mm, "end": v(207.96, 96.84) * mm});
            skLineSegment(sketch, "E2.8.5.0", {"start": v(209.55, 120.65) * mm, "end": v(196.85, 120.65) * mm});
            skLineSegment(sketch, "E2.8.5.1", {"start": v(198.44, 131.76) * mm, "end": v(198.44, 122.24) * mm});
            skPoint(sketch, "E2.8.5.2", {"position": v(203.2, 127) * mm});
            skLineSegment(sketch, "E2.8.5.3", {"start": v(207.96, 122.24) * mm, "end": v(198.44, 122.24) * mm});
            skLineSegment(sketch, "E2.8.5.4", {"start": v(209.55, 133.35) * mm, "end": v(209.55, 120.65) * mm});
            skLineSegment(sketch, "E2.8.5.5", {"start": v(209.55, 133.35) * mm, "end": v(196.85, 133.35) * mm});
            skLineSegment(sketch, "E2.8.5.6", {"start": v(196.85, 133.35) * mm, "end": v(196.85, 120.65) * mm});
            skLineSegment(sketch, "E2.8.5.7", {"start": v(207.96, 131.76) * mm, "end": v(198.44, 131.76) * mm});
            skLineSegment(sketch, "E2.8.5.8", {"start": v(207.96, 131.76) * mm, "end": v(207.96, 122.24) * mm});
            skLineSegment(sketch, "E2.8.6.0", {"start": v(209.55, 146.05) * mm, "end": v(196.85, 146.05) * mm});
            skLineSegment(sketch, "E2.8.6.1", {"start": v(198.44, 157.16) * mm, "end": v(198.44, 147.64) * mm});
            skPoint(sketch, "E2.8.6.2", {"position": v(203.2, 152.4) * mm});
            skLineSegment(sketch, "E2.8.6.3", {"start": v(207.96, 147.64) * mm, "end": v(198.44, 147.64) * mm});
            skLineSegment(sketch, "E2.8.6.4", {"start": v(209.55, 158.75) * mm, "end": v(209.55, 146.05) * mm});
            skLineSegment(sketch, "E2.8.6.5", {"start": v(209.55, 158.75) * mm, "end": v(196.85, 158.75) * mm});
            skLineSegment(sketch, "E2.8.6.6", {"start": v(196.85, 158.75) * mm, "end": v(196.85, 146.05) * mm});
            skLineSegment(sketch, "E2.8.6.7", {"start": v(207.96, 157.16) * mm, "end": v(198.44, 157.16) * mm});
            skLineSegment(sketch, "E2.8.6.8", {"start": v(207.96, 157.16) * mm, "end": v(207.96, 147.64) * mm});
            skLineSegment(sketch, "E2.8.7.0", {"start": v(209.55, 171.45) * mm, "end": v(196.85, 171.45) * mm});
            skLineSegment(sketch, "E2.8.7.1", {"start": v(198.44, 182.56) * mm, "end": v(198.44, 173.04) * mm});
            skPoint(sketch, "E2.8.7.2", {"position": v(203.2, 177.8) * mm});
            skLineSegment(sketch, "E2.8.7.3", {"start": v(207.96, 173.04) * mm, "end": v(198.44, 173.04) * mm});
            skLineSegment(sketch, "E2.8.7.4", {"start": v(209.55, 184.15) * mm, "end": v(209.55, 171.45) * mm});
            skLineSegment(sketch, "E2.8.7.5", {"start": v(209.55, 184.15) * mm, "end": v(196.85, 184.15) * mm});
            skLineSegment(sketch, "E2.8.7.6", {"start": v(196.85, 184.15) * mm, "end": v(196.85, 171.45) * mm});
            skLineSegment(sketch, "E2.8.7.7", {"start": v(207.96, 182.56) * mm, "end": v(198.44, 182.56) * mm});
            skLineSegment(sketch, "E2.8.7.8", {"start": v(207.96, 182.56) * mm, "end": v(207.96, 173.04) * mm});
            skLineSegment(sketch, "E2.8.8.0", {"start": v(209.55, 196.85) * mm, "end": v(196.85, 196.85) * mm});
            skLineSegment(sketch, "E2.8.8.1", {"start": v(198.44, 207.96) * mm, "end": v(198.44, 198.44) * mm});
            skPoint(sketch, "E2.8.8.2", {"position": v(203.2, 203.2) * mm});
            skLineSegment(sketch, "E2.8.8.3", {"start": v(207.96, 198.44) * mm, "end": v(198.44, 198.44) * mm});
            skLineSegment(sketch, "E2.8.8.4", {"start": v(209.55, 209.55) * mm, "end": v(209.55, 196.85) * mm});
            skLineSegment(sketch, "E2.8.8.5", {"start": v(209.55, 209.55) * mm, "end": v(196.85, 209.55) * mm});
            skLineSegment(sketch, "E2.8.8.6", {"start": v(196.85, 209.55) * mm, "end": v(196.85, 196.85) * mm});
            skLineSegment(sketch, "E2.8.8.7", {"start": v(207.96, 207.96) * mm, "end": v(198.44, 207.96) * mm});
            skLineSegment(sketch, "E2.8.8.8", {"start": v(207.96, 207.96) * mm, "end": v(207.96, 198.44) * mm});
            skLineSegment(sketch, "E2.8.9.0", {"start": v(209.55, 222.25) * mm, "end": v(196.85, 222.25) * mm});
            skLineSegment(sketch, "E2.8.9.1", {"start": v(198.44, 233.36) * mm, "end": v(198.44, 223.84) * mm});
            skPoint(sketch, "E2.8.9.2", {"position": v(203.2, 228.6) * mm});
            skLineSegment(sketch, "E2.8.9.3", {"start": v(207.96, 223.84) * mm, "end": v(198.44, 223.84) * mm});
            skLineSegment(sketch, "E2.8.9.4", {"start": v(209.55, 234.95) * mm, "end": v(209.55, 222.25) * mm});
            skLineSegment(sketch, "E2.8.9.5", {"start": v(209.55, 234.95) * mm, "end": v(196.85, 234.95) * mm});
            skLineSegment(sketch, "E2.8.9.6", {"start": v(196.85, 234.95) * mm, "end": v(196.85, 222.25) * mm});
            skLineSegment(sketch, "E2.8.9.7", {"start": v(207.96, 233.36) * mm, "end": v(198.44, 233.36) * mm});
            skLineSegment(sketch, "E2.8.9.8", {"start": v(207.96, 233.36) * mm, "end": v(207.96, 223.84) * mm});
            skLineSegment(sketch, "E2.8.10.0", {"start": v(209.55, 247.65) * mm, "end": v(196.85, 247.65) * mm});
            skLineSegment(sketch, "E2.8.10.1", {"start": v(198.44, 258.76) * mm, "end": v(198.44, 249.24) * mm});
            skPoint(sketch, "E2.8.10.2", {"position": v(203.2, 254) * mm});
            skLineSegment(sketch, "E2.8.10.3", {"start": v(207.96, 249.24) * mm, "end": v(198.44, 249.24) * mm});
            skLineSegment(sketch, "E2.8.10.4", {"start": v(209.55, 260.35) * mm, "end": v(209.55, 247.65) * mm});
            skLineSegment(sketch, "E2.8.10.5", {"start": v(209.55, 260.35) * mm, "end": v(196.85, 260.35) * mm});
            skLineSegment(sketch, "E2.8.10.6", {"start": v(196.85, 260.35) * mm, "end": v(196.85, 247.65) * mm});
            skLineSegment(sketch, "E2.8.10.7", {"start": v(207.96, 258.76) * mm, "end": v(198.44, 258.76) * mm});
            skLineSegment(sketch, "E2.8.10.8", {"start": v(207.96, 258.76) * mm, "end": v(207.96, 249.24) * mm});
            skLineSegment(sketch, "E2.8.11.0", {"start": v(209.55, 273.05) * mm, "end": v(196.85, 273.05) * mm});
            skLineSegment(sketch, "E2.8.11.1", {"start": v(198.44, 284.16) * mm, "end": v(198.44, 274.64) * mm});
            skPoint(sketch, "E2.8.11.2", {"position": v(203.2, 279.4) * mm});
            skLineSegment(sketch, "E2.8.11.3", {"start": v(207.96, 274.64) * mm, "end": v(198.44, 274.64) * mm});
            skLineSegment(sketch, "E2.8.11.4", {"start": v(209.55, 285.75) * mm, "end": v(209.55, 273.05) * mm});
            skLineSegment(sketch, "E2.8.11.5", {"start": v(209.55, 285.75) * mm, "end": v(196.85, 285.75) * mm});
            skLineSegment(sketch, "E2.8.11.6", {"start": v(196.85, 285.75) * mm, "end": v(196.85, 273.05) * mm});
            skLineSegment(sketch, "E2.8.11.7", {"start": v(207.96, 284.16) * mm, "end": v(198.44, 284.16) * mm});
            skLineSegment(sketch, "E2.8.11.8", {"start": v(207.96, 284.16) * mm, "end": v(207.96, 274.64) * mm});
            skLineSegment(sketch, "E2.8.12.0", {"start": v(209.55, 298.45) * mm, "end": v(196.85, 298.45) * mm});
            skLineSegment(sketch, "E2.8.12.1", {"start": v(198.44, 309.56) * mm, "end": v(198.44, 300.04) * mm});
            skPoint(sketch, "E2.8.12.2", {"position": v(203.2, 304.8) * mm});
            skLineSegment(sketch, "E2.8.12.3", {"start": v(207.96, 300.04) * mm, "end": v(198.44, 300.04) * mm});
            skLineSegment(sketch, "E2.8.12.4", {"start": v(209.55, 311.15) * mm, "end": v(209.55, 298.45) * mm});
            skLineSegment(sketch, "E2.8.12.5", {"start": v(209.55, 311.15) * mm, "end": v(196.85, 311.15) * mm});
            skLineSegment(sketch, "E2.8.12.6", {"start": v(196.85, 311.15) * mm, "end": v(196.85, 298.45) * mm});
            skLineSegment(sketch, "E2.8.12.7", {"start": v(207.96, 309.56) * mm, "end": v(198.44, 309.56) * mm});
            skLineSegment(sketch, "E2.8.12.8", {"start": v(207.96, 309.56) * mm, "end": v(207.96, 300.04) * mm});
            skLineSegment(sketch, "E2.8.13.0", {"start": v(209.55, 323.85) * mm, "end": v(196.85, 323.85) * mm});
            skLineSegment(sketch, "E2.8.13.1", {"start": v(198.44, 334.96) * mm, "end": v(198.44, 325.44) * mm});
            skPoint(sketch, "E2.8.13.2", {"position": v(203.2, 330.2) * mm});
            skLineSegment(sketch, "E2.8.13.3", {"start": v(207.96, 325.44) * mm, "end": v(198.44, 325.44) * mm});
            skLineSegment(sketch, "E2.8.13.4", {"start": v(209.55, 336.55) * mm, "end": v(209.55, 323.85) * mm});
            skLineSegment(sketch, "E2.8.13.5", {"start": v(209.55, 336.55) * mm, "end": v(196.85, 336.55) * mm});
            skLineSegment(sketch, "E2.8.13.6", {"start": v(196.85, 336.55) * mm, "end": v(196.85, 323.85) * mm});
            skLineSegment(sketch, "E2.8.13.7", {"start": v(207.96, 334.96) * mm, "end": v(198.44, 334.96) * mm});
            skLineSegment(sketch, "E2.8.13.8", {"start": v(207.96, 334.96) * mm, "end": v(207.96, 325.44) * mm});
            skLineSegment(sketch, "E2.8.14.0", {"start": v(209.55, 349.25) * mm, "end": v(196.85, 349.25) * mm});
            skLineSegment(sketch, "E2.8.14.1", {"start": v(198.44, 360.36) * mm, "end": v(198.44, 350.84) * mm});
            skPoint(sketch, "E2.8.14.2", {"position": v(203.2, 355.6) * mm});
            skLineSegment(sketch, "E2.8.14.3", {"start": v(207.96, 350.84) * mm, "end": v(198.44, 350.84) * mm});
            skLineSegment(sketch, "E2.8.14.4", {"start": v(209.55, 361.95) * mm, "end": v(209.55, 349.25) * mm});
            skLineSegment(sketch, "E2.8.14.5", {"start": v(209.55, 361.95) * mm, "end": v(196.85, 361.95) * mm});
            skLineSegment(sketch, "E2.8.14.6", {"start": v(196.85, 361.95) * mm, "end": v(196.85, 349.25) * mm});
            skLineSegment(sketch, "E2.8.14.7", {"start": v(207.96, 360.36) * mm, "end": v(198.44, 360.36) * mm});
            skLineSegment(sketch, "E2.8.14.8", {"start": v(207.96, 360.36) * mm, "end": v(207.96, 350.84) * mm});
            skLineSegment(sketch, "E2.direction1", {"start": v(-6.35, -6.35) * mm, "end": v(19.05, -6.35) * mm, "construction": true});
            skLineSegment(sketch, "E2.direction2", {"start": v(-6.35, -6.35) * mm, "end": v(-6.35, 19.05) * mm, "construction": true});
            skLineSegment(sketch, "E3.0.0.15", {"start": v(6.35, 374.65) * mm, "end": v(-6.35, 374.65) * mm});
            skLineSegment(sketch, "E3.3.0.15", {"start": v(-4.76, 385.76) * mm, "end": v(-4.76, 376.24) * mm});
            skPoint(sketch, "E3.6.0.15", {"position": v(0, 381) * mm});
            skLineSegment(sketch, "E3.7.0.15", {"start": v(4.76, 376.24) * mm, "end": v(-4.76, 376.24) * mm});
            skLineSegment(sketch, "E3.10.0.15", {"start": v(6.35, 387.35) * mm, "end": v(6.35, 374.65) * mm});
            skLineSegment(sketch, "E3.13.0.15", {"start": v(6.35, 387.35) * mm, "end": v(-6.35, 387.35) * mm});
            skLineSegment(sketch, "E3.16.0.15", {"start": v(-6.35, 387.35) * mm, "end": v(-6.35, 374.65) * mm});
            skLineSegment(sketch, "E3.19.0.15", {"start": v(4.76, 385.76) * mm, "end": v(-4.76, 385.76) * mm});
            skLineSegment(sketch, "E3.22.0.15", {"start": v(4.76, 385.76) * mm, "end": v(4.76, 376.24) * mm});
            skLineSegment(sketch, "E3.0.0.16", {"start": v(6.35, 400.05) * mm, "end": v(-6.35, 400.05) * mm});
            skLineSegment(sketch, "E3.3.0.16", {"start": v(-4.76, 411.16) * mm, "end": v(-4.76, 401.64) * mm});
            skPoint(sketch, "E3.6.0.16", {"position": v(0, 406.4) * mm});
            skLineSegment(sketch, "E3.7.0.16", {"start": v(4.76, 401.64) * mm, "end": v(-4.76, 401.64) * mm});
            skLineSegment(sketch, "E3.10.0.16", {"start": v(6.35, 412.75) * mm, "end": v(6.35, 400.05) * mm});
            skLineSegment(sketch, "E3.13.0.16", {"start": v(6.35, 412.75) * mm, "end": v(-6.35, 412.75) * mm});
            skLineSegment(sketch, "E3.16.0.16", {"start": v(-6.35, 412.75) * mm, "end": v(-6.35, 400.05) * mm});
            skLineSegment(sketch, "E3.19.0.16", {"start": v(4.76, 411.16) * mm, "end": v(-4.76, 411.16) * mm});
            skLineSegment(sketch, "E3.22.0.16", {"start": v(4.76, 411.16) * mm, "end": v(4.76, 401.64) * mm});
            skLineSegment(sketch, "E3.0.0.17", {"start": v(6.35, 425.45) * mm, "end": v(-6.35, 425.45) * mm});
            skLineSegment(sketch, "E3.3.0.17", {"start": v(-4.76, 436.56) * mm, "end": v(-4.76, 427.04) * mm});
            skPoint(sketch, "E3.6.0.17", {"position": v(0, 431.8) * mm});
            skLineSegment(sketch, "E3.7.0.17", {"start": v(4.76, 427.04) * mm, "end": v(-4.76, 427.04) * mm});
            skLineSegment(sketch, "E3.10.0.17", {"start": v(6.35, 438.15) * mm, "end": v(6.35, 425.45) * mm});
            skLineSegment(sketch, "E3.13.0.17", {"start": v(6.35, 438.15) * mm, "end": v(-6.35, 438.15) * mm});
            skLineSegment(sketch, "E3.16.0.17", {"start": v(-6.35, 438.15) * mm, "end": v(-6.35, 425.45) * mm});
            skLineSegment(sketch, "E3.19.0.17", {"start": v(4.76, 436.56) * mm, "end": v(-4.76, 436.56) * mm});
            skLineSegment(sketch, "E3.22.0.17", {"start": v(4.76, 436.56) * mm, "end": v(4.76, 427.04) * mm});
            skLineSegment(sketch, "E3.0.0.18", {"start": v(6.35, 450.85) * mm, "end": v(-6.35, 450.85) * mm});
            skLineSegment(sketch, "E3.3.0.18", {"start": v(-4.76, 461.96) * mm, "end": v(-4.76, 452.44) * mm});
            skPoint(sketch, "E3.6.0.18", {"position": v(0, 457.2) * mm});
            skLineSegment(sketch, "E3.7.0.18", {"start": v(4.76, 452.44) * mm, "end": v(-4.76, 452.44) * mm});
            skLineSegment(sketch, "E3.10.0.18", {"start": v(6.35, 463.55) * mm, "end": v(6.35, 450.85) * mm});
            skLineSegment(sketch, "E3.13.0.18", {"start": v(6.35, 463.55) * mm, "end": v(-6.35, 463.55) * mm});
            skLineSegment(sketch, "E3.16.0.18", {"start": v(-6.35, 463.55) * mm, "end": v(-6.35, 450.85) * mm});
            skLineSegment(sketch, "E3.19.0.18", {"start": v(4.76, 461.96) * mm, "end": v(-4.76, 461.96) * mm});
            skLineSegment(sketch, "E3.22.0.18", {"start": v(4.76, 461.96) * mm, "end": v(4.76, 452.44) * mm});
            skLineSegment(sketch, "E3.0.0.19", {"start": v(6.35, 476.25) * mm, "end": v(-6.35, 476.25) * mm});
            skLineSegment(sketch, "E3.3.0.19", {"start": v(-4.76, 487.36) * mm, "end": v(-4.76, 477.84) * mm});
            skPoint(sketch, "E3.6.0.19", {"position": v(0, 482.6) * mm});
            skLineSegment(sketch, "E3.7.0.19", {"start": v(4.76, 477.84) * mm, "end": v(-4.76, 477.84) * mm});
            skLineSegment(sketch, "E3.10.0.19", {"start": v(6.35, 488.95) * mm, "end": v(6.35, 476.25) * mm});
            skLineSegment(sketch, "E3.13.0.19", {"start": v(6.35, 488.95) * mm, "end": v(-6.35, 488.95) * mm});
            skLineSegment(sketch, "E3.16.0.19", {"start": v(-6.35, 488.95) * mm, "end": v(-6.35, 476.25) * mm});
            skLineSegment(sketch, "E3.19.0.19", {"start": v(4.76, 487.36) * mm, "end": v(-4.76, 487.36) * mm});
            skLineSegment(sketch, "E3.22.0.19", {"start": v(4.76, 487.36) * mm, "end": v(4.76, 477.84) * mm});
            skLineSegment(sketch, "E3.0.0.20", {"start": v(6.35, 501.65) * mm, "end": v(-6.35, 501.65) * mm});
            skLineSegment(sketch, "E3.3.0.20", {"start": v(-4.76, 512.76) * mm, "end": v(-4.76, 503.24) * mm});
            skPoint(sketch, "E3.6.0.20", {"position": v(0, 508) * mm});
            skLineSegment(sketch, "E3.7.0.20", {"start": v(4.76, 503.24) * mm, "end": v(-4.76, 503.24) * mm});
            skLineSegment(sketch, "E3.10.0.20", {"start": v(6.35, 514.35) * mm, "end": v(6.35, 501.65) * mm});
            skLineSegment(sketch, "E3.13.0.20", {"start": v(6.35, 514.35) * mm, "end": v(-6.35, 514.35) * mm});
            skLineSegment(sketch, "E3.16.0.20", {"start": v(-6.35, 514.35) * mm, "end": v(-6.35, 501.65) * mm});
            skLineSegment(sketch, "E3.19.0.20", {"start": v(4.76, 512.76) * mm, "end": v(-4.76, 512.76) * mm});
            skLineSegment(sketch, "E3.22.0.20", {"start": v(4.76, 512.76) * mm, "end": v(4.76, 503.24) * mm});
            skLineSegment(sketch, "E3.0.0.21", {"start": v(6.35, 527.05) * mm, "end": v(-6.35, 527.05) * mm});
            skLineSegment(sketch, "E3.3.0.21", {"start": v(-4.76, 538.16) * mm, "end": v(-4.76, 528.64) * mm});
            skPoint(sketch, "E3.6.0.21", {"position": v(0, 533.4) * mm});
            skLineSegment(sketch, "E3.7.0.21", {"start": v(4.76, 528.64) * mm, "end": v(-4.76, 528.64) * mm});
            skLineSegment(sketch, "E3.10.0.21", {"start": v(6.35, 539.75) * mm, "end": v(6.35, 527.05) * mm});
            skLineSegment(sketch, "E3.13.0.21", {"start": v(6.35, 539.75) * mm, "end": v(-6.35, 539.75) * mm});
            skLineSegment(sketch, "E3.16.0.21", {"start": v(-6.35, 539.75) * mm, "end": v(-6.35, 527.05) * mm});
            skLineSegment(sketch, "E3.19.0.21", {"start": v(4.76, 538.16) * mm, "end": v(-4.76, 538.16) * mm});
            skLineSegment(sketch, "E3.22.0.21", {"start": v(4.76, 538.16) * mm, "end": v(4.76, 528.64) * mm});
            skLineSegment(sketch, "E3.0.1.15", {"start": v(31.75, 374.65) * mm, "end": v(19.05, 374.65) * mm});
            skLineSegment(sketch, "E3.3.1.15", {"start": v(20.64, 385.76) * mm, "end": v(20.64, 376.24) * mm});
            skPoint(sketch, "E3.6.1.15", {"position": v(25.4, 381) * mm});
            skLineSegment(sketch, "E3.7.1.15", {"start": v(30.16, 376.24) * mm, "end": v(20.64, 376.24) * mm});
            skLineSegment(sketch, "E3.10.1.15", {"start": v(31.75, 387.35) * mm, "end": v(31.75, 374.65) * mm});
            skLineSegment(sketch, "E3.13.1.15", {"start": v(31.75, 387.35) * mm, "end": v(19.05, 387.35) * mm});
            skLineSegment(sketch, "E3.16.1.15", {"start": v(19.05, 387.35) * mm, "end": v(19.05, 374.65) * mm});
            skLineSegment(sketch, "E3.19.1.15", {"start": v(30.16, 385.76) * mm, "end": v(20.64, 385.76) * mm});
            skLineSegment(sketch, "E3.22.1.15", {"start": v(30.16, 385.76) * mm, "end": v(30.16, 376.24) * mm});
            skLineSegment(sketch, "E3.0.1.16", {"start": v(31.75, 400.05) * mm, "end": v(19.05, 400.05) * mm});
            skLineSegment(sketch, "E3.3.1.16", {"start": v(20.64, 411.16) * mm, "end": v(20.64, 401.64) * mm});
            skPoint(sketch, "E3.6.1.16", {"position": v(25.4, 406.4) * mm});
            skLineSegment(sketch, "E3.7.1.16", {"start": v(30.16, 401.64) * mm, "end": v(20.64, 401.64) * mm});
            skLineSegment(sketch, "E3.10.1.16", {"start": v(31.75, 412.75) * mm, "end": v(31.75, 400.05) * mm});
            skLineSegment(sketch, "E3.13.1.16", {"start": v(31.75, 412.75) * mm, "end": v(19.05, 412.75) * mm});
            skLineSegment(sketch, "E3.16.1.16", {"start": v(19.05, 412.75) * mm, "end": v(19.05, 400.05) * mm});
            skLineSegment(sketch, "E3.19.1.16", {"start": v(30.16, 411.16) * mm, "end": v(20.64, 411.16) * mm});
            skLineSegment(sketch, "E3.22.1.16", {"start": v(30.16, 411.16) * mm, "end": v(30.16, 401.64) * mm});
            skLineSegment(sketch, "E3.0.1.17", {"start": v(31.75, 425.45) * mm, "end": v(19.05, 425.45) * mm});
            skLineSegment(sketch, "E3.3.1.17", {"start": v(20.64, 436.56) * mm, "end": v(20.64, 427.04) * mm});
            skPoint(sketch, "E3.6.1.17", {"position": v(25.4, 431.8) * mm});
            skLineSegment(sketch, "E3.7.1.17", {"start": v(30.16, 427.04) * mm, "end": v(20.64, 427.04) * mm});
            skLineSegment(sketch, "E3.10.1.17", {"start": v(31.75, 438.15) * mm, "end": v(31.75, 425.45) * mm});
            skLineSegment(sketch, "E3.13.1.17", {"start": v(31.75, 438.15) * mm, "end": v(19.05, 438.15) * mm});
            skLineSegment(sketch, "E3.16.1.17", {"start": v(19.05, 438.15) * mm, "end": v(19.05, 425.45) * mm});
            skLineSegment(sketch, "E3.19.1.17", {"start": v(30.16, 436.56) * mm, "end": v(20.64, 436.56) * mm});
            skLineSegment(sketch, "E3.22.1.17", {"start": v(30.16, 436.56) * mm, "end": v(30.16, 427.04) * mm});
            skLineSegment(sketch, "E3.0.1.18", {"start": v(31.75, 450.85) * mm, "end": v(19.05, 450.85) * mm});
            skLineSegment(sketch, "E3.3.1.18", {"start": v(20.64, 461.96) * mm, "end": v(20.64, 452.44) * mm});
            skPoint(sketch, "E3.6.1.18", {"position": v(25.4, 457.2) * mm});
            skLineSegment(sketch, "E3.7.1.18", {"start": v(30.16, 452.44) * mm, "end": v(20.64, 452.44) * mm});
            skLineSegment(sketch, "E3.10.1.18", {"start": v(31.75, 463.55) * mm, "end": v(31.75, 450.85) * mm});
            skLineSegment(sketch, "E3.13.1.18", {"start": v(31.75, 463.55) * mm, "end": v(19.05, 463.55) * mm});
            skLineSegment(sketch, "E3.16.1.18", {"start": v(19.05, 463.55) * mm, "end": v(19.05, 450.85) * mm});
            skLineSegment(sketch, "E3.19.1.18", {"start": v(30.16, 461.96) * mm, "end": v(20.64, 461.96) * mm});
            skLineSegment(sketch, "E3.22.1.18", {"start": v(30.16, 461.96) * mm, "end": v(30.16, 452.44) * mm});
            skLineSegment(sketch, "E3.0.1.19", {"start": v(31.75, 476.25) * mm, "end": v(19.05, 476.25) * mm});
            skLineSegment(sketch, "E3.3.1.19", {"start": v(20.64, 487.36) * mm, "end": v(20.64, 477.84) * mm});
            skPoint(sketch, "E3.6.1.19", {"position": v(25.4, 482.6) * mm});
            skLineSegment(sketch, "E3.7.1.19", {"start": v(30.16, 477.84) * mm, "end": v(20.64, 477.84) * mm});
            skLineSegment(sketch, "E3.10.1.19", {"start": v(31.75, 488.95) * mm, "end": v(31.75, 476.25) * mm});
            skLineSegment(sketch, "E3.13.1.19", {"start": v(31.75, 488.95) * mm, "end": v(19.05, 488.95) * mm});
            skLineSegment(sketch, "E3.16.1.19", {"start": v(19.05, 488.95) * mm, "end": v(19.05, 476.25) * mm});
            skLineSegment(sketch, "E3.19.1.19", {"start": v(30.16, 487.36) * mm, "end": v(20.64, 487.36) * mm});
            skLineSegment(sketch, "E3.22.1.19", {"start": v(30.16, 487.36) * mm, "end": v(30.16, 477.84) * mm});
            skLineSegment(sketch, "E3.0.1.20", {"start": v(31.75, 501.65) * mm, "end": v(19.05, 501.65) * mm});
            skLineSegment(sketch, "E3.3.1.20", {"start": v(20.64, 512.76) * mm, "end": v(20.64, 503.24) * mm});
            skPoint(sketch, "E3.6.1.20", {"position": v(25.4, 508) * mm});
            skLineSegment(sketch, "E3.7.1.20", {"start": v(30.16, 503.24) * mm, "end": v(20.64, 503.24) * mm});
            skLineSegment(sketch, "E3.10.1.20", {"start": v(31.75, 514.35) * mm, "end": v(31.75, 501.65) * mm});
            skLineSegment(sketch, "E3.13.1.20", {"start": v(31.75, 514.35) * mm, "end": v(19.05, 514.35) * mm});
            skLineSegment(sketch, "E3.16.1.20", {"start": v(19.05, 514.35) * mm, "end": v(19.05, 501.65) * mm});
            skLineSegment(sketch, "E3.19.1.20", {"start": v(30.16, 512.76) * mm, "end": v(20.64, 512.76) * mm});
            skLineSegment(sketch, "E3.22.1.20", {"start": v(30.16, 512.76) * mm, "end": v(30.16, 503.24) * mm});
            skLineSegment(sketch, "E3.0.1.21", {"start": v(31.75, 527.05) * mm, "end": v(19.05, 527.05) * mm});
            skLineSegment(sketch, "E3.3.1.21", {"start": v(20.64, 538.16) * mm, "end": v(20.64, 528.64) * mm});
            skPoint(sketch, "E3.6.1.21", {"position": v(25.4, 533.4) * mm});
            skLineSegment(sketch, "E3.7.1.21", {"start": v(30.16, 528.64) * mm, "end": v(20.64, 528.64) * mm});
            skLineSegment(sketch, "E3.10.1.21", {"start": v(31.75, 539.75) * mm, "end": v(31.75, 527.05) * mm});
            skLineSegment(sketch, "E3.13.1.21", {"start": v(31.75, 539.75) * mm, "end": v(19.05, 539.75) * mm});
            skLineSegment(sketch, "E3.16.1.21", {"start": v(19.05, 539.75) * mm, "end": v(19.05, 527.05) * mm});
            skLineSegment(sketch, "E3.19.1.21", {"start": v(30.16, 538.16) * mm, "end": v(20.64, 538.16) * mm});
            skLineSegment(sketch, "E3.22.1.21", {"start": v(30.16, 538.16) * mm, "end": v(30.16, 528.64) * mm});
            skLineSegment(sketch, "E3.0.2.15", {"start": v(57.15, 374.65) * mm, "end": v(44.45, 374.65) * mm});
            skLineSegment(sketch, "E3.3.2.15", {"start": v(46.04, 385.76) * mm, "end": v(46.04, 376.24) * mm});
            skPoint(sketch, "E3.6.2.15", {"position": v(50.8, 381) * mm});
            skLineSegment(sketch, "E3.7.2.15", {"start": v(55.56, 376.24) * mm, "end": v(46.04, 376.24) * mm});
            skLineSegment(sketch, "E3.10.2.15", {"start": v(57.15, 387.35) * mm, "end": v(57.15, 374.65) * mm});
            skLineSegment(sketch, "E3.13.2.15", {"start": v(57.15, 387.35) * mm, "end": v(44.45, 387.35) * mm});
            skLineSegment(sketch, "E3.16.2.15", {"start": v(44.45, 387.35) * mm, "end": v(44.45, 374.65) * mm});
            skLineSegment(sketch, "E3.19.2.15", {"start": v(55.56, 385.76) * mm, "end": v(46.04, 385.76) * mm});
            skLineSegment(sketch, "E3.22.2.15", {"start": v(55.56, 385.76) * mm, "end": v(55.56, 376.24) * mm});
            skLineSegment(sketch, "E3.0.2.16", {"start": v(57.15, 400.05) * mm, "end": v(44.45, 400.05) * mm});
            skLineSegment(sketch, "E3.3.2.16", {"start": v(46.04, 411.16) * mm, "end": v(46.04, 401.64) * mm});
            skPoint(sketch, "E3.6.2.16", {"position": v(50.8, 406.4) * mm});
            skLineSegment(sketch, "E3.7.2.16", {"start": v(55.56, 401.64) * mm, "end": v(46.04, 401.64) * mm});
            skLineSegment(sketch, "E3.10.2.16", {"start": v(57.15, 412.75) * mm, "end": v(57.15, 400.05) * mm});
            skLineSegment(sketch, "E3.13.2.16", {"start": v(57.15, 412.75) * mm, "end": v(44.45, 412.75) * mm});
            skLineSegment(sketch, "E3.16.2.16", {"start": v(44.45, 412.75) * mm, "end": v(44.45, 400.05) * mm});
            skLineSegment(sketch, "E3.19.2.16", {"start": v(55.56, 411.16) * mm, "end": v(46.04, 411.16) * mm});
            skLineSegment(sketch, "E3.22.2.16", {"start": v(55.56, 411.16) * mm, "end": v(55.56, 401.64) * mm});
            skLineSegment(sketch, "E3.0.2.17", {"start": v(57.15, 425.45) * mm, "end": v(44.45, 425.45) * mm});
            skLineSegment(sketch, "E3.3.2.17", {"start": v(46.04, 436.56) * mm, "end": v(46.04, 427.04) * mm});
            skPoint(sketch, "E3.6.2.17", {"position": v(50.8, 431.8) * mm});
            skLineSegment(sketch, "E3.7.2.17", {"start": v(55.56, 427.04) * mm, "end": v(46.04, 427.04) * mm});
            skLineSegment(sketch, "E3.10.2.17", {"start": v(57.15, 438.15) * mm, "end": v(57.15, 425.45) * mm});
            skLineSegment(sketch, "E3.13.2.17", {"start": v(57.15, 438.15) * mm, "end": v(44.45, 438.15) * mm});
            skLineSegment(sketch, "E3.16.2.17", {"start": v(44.45, 438.15) * mm, "end": v(44.45, 425.45) * mm});
            skLineSegment(sketch, "E3.19.2.17", {"start": v(55.56, 436.56) * mm, "end": v(46.04, 436.56) * mm});
            skLineSegment(sketch, "E3.22.2.17", {"start": v(55.56, 436.56) * mm, "end": v(55.56, 427.04) * mm});
            skLineSegment(sketch, "E3.0.2.18", {"start": v(57.15, 450.85) * mm, "end": v(44.45, 450.85) * mm});
            skLineSegment(sketch, "E3.3.2.18", {"start": v(46.04, 461.96) * mm, "end": v(46.04, 452.44) * mm});
            skPoint(sketch, "E3.6.2.18", {"position": v(50.8, 457.2) * mm});
            skLineSegment(sketch, "E3.7.2.18", {"start": v(55.56, 452.44) * mm, "end": v(46.04, 452.44) * mm});
            skLineSegment(sketch, "E3.10.2.18", {"start": v(57.15, 463.55) * mm, "end": v(57.15, 450.85) * mm});
            skLineSegment(sketch, "E3.13.2.18", {"start": v(57.15, 463.55) * mm, "end": v(44.45, 463.55) * mm});
            skLineSegment(sketch, "E3.16.2.18", {"start": v(44.45, 463.55) * mm, "end": v(44.45, 450.85) * mm});
            skLineSegment(sketch, "E3.19.2.18", {"start": v(55.56, 461.96) * mm, "end": v(46.04, 461.96) * mm});
            skLineSegment(sketch, "E3.22.2.18", {"start": v(55.56, 461.96) * mm, "end": v(55.56, 452.44) * mm});
            skLineSegment(sketch, "E3.0.2.19", {"start": v(57.15, 476.25) * mm, "end": v(44.45, 476.25) * mm});
            skLineSegment(sketch, "E3.3.2.19", {"start": v(46.04, 487.36) * mm, "end": v(46.04, 477.84) * mm});
            skPoint(sketch, "E3.6.2.19", {"position": v(50.8, 482.6) * mm});
            skLineSegment(sketch, "E3.7.2.19", {"start": v(55.56, 477.84) * mm, "end": v(46.04, 477.84) * mm});
            skLineSegment(sketch, "E3.10.2.19", {"start": v(57.15, 488.95) * mm, "end": v(57.15, 476.25) * mm});
            skLineSegment(sketch, "E3.13.2.19", {"start": v(57.15, 488.95) * mm, "end": v(44.45, 488.95) * mm});
            skLineSegment(sketch, "E3.16.2.19", {"start": v(44.45, 488.95) * mm, "end": v(44.45, 476.25) * mm});
            skLineSegment(sketch, "E3.19.2.19", {"start": v(55.56, 487.36) * mm, "end": v(46.04, 487.36) * mm});
            skLineSegment(sketch, "E3.22.2.19", {"start": v(55.56, 487.36) * mm, "end": v(55.56, 477.84) * mm});
            skLineSegment(sketch, "E3.0.2.20", {"start": v(57.15, 501.65) * mm, "end": v(44.45, 501.65) * mm});
            skLineSegment(sketch, "E3.3.2.20", {"start": v(46.04, 512.76) * mm, "end": v(46.04, 503.24) * mm});
            skPoint(sketch, "E3.6.2.20", {"position": v(50.8, 508) * mm});
            skLineSegment(sketch, "E3.7.2.20", {"start": v(55.56, 503.24) * mm, "end": v(46.04, 503.24) * mm});
            skLineSegment(sketch, "E3.10.2.20", {"start": v(57.15, 514.35) * mm, "end": v(57.15, 501.65) * mm});
            skLineSegment(sketch, "E3.13.2.20", {"start": v(57.15, 514.35) * mm, "end": v(44.45, 514.35) * mm});
            skLineSegment(sketch, "E3.16.2.20", {"start": v(44.45, 514.35) * mm, "end": v(44.45, 501.65) * mm});
            skLineSegment(sketch, "E3.19.2.20", {"start": v(55.56, 512.76) * mm, "end": v(46.04, 512.76) * mm});
            skLineSegment(sketch, "E3.22.2.20", {"start": v(55.56, 512.76) * mm, "end": v(55.56, 503.24) * mm});
            skLineSegment(sketch, "E3.0.2.21", {"start": v(57.15, 527.05) * mm, "end": v(44.45, 527.05) * mm});
            skLineSegment(sketch, "E3.3.2.21", {"start": v(46.04, 538.16) * mm, "end": v(46.04, 528.64) * mm});
            skPoint(sketch, "E3.6.2.21", {"position": v(50.8, 533.4) * mm});
            skLineSegment(sketch, "E3.7.2.21", {"start": v(55.56, 528.64) * mm, "end": v(46.04, 528.64) * mm});
            skLineSegment(sketch, "E3.10.2.21", {"start": v(57.15, 539.75) * mm, "end": v(57.15, 527.05) * mm});
            skLineSegment(sketch, "E3.13.2.21", {"start": v(57.15, 539.75) * mm, "end": v(44.45, 539.75) * mm});
            skLineSegment(sketch, "E3.16.2.21", {"start": v(44.45, 539.75) * mm, "end": v(44.45, 527.05) * mm});
            skLineSegment(sketch, "E3.19.2.21", {"start": v(55.56, 538.16) * mm, "end": v(46.04, 538.16) * mm});
            skLineSegment(sketch, "E3.22.2.21", {"start": v(55.56, 538.16) * mm, "end": v(55.56, 528.64) * mm});
            skLineSegment(sketch, "E3.0.3.15", {"start": v(82.55, 374.65) * mm, "end": v(69.85, 374.65) * mm});
            skLineSegment(sketch, "E3.3.3.15", {"start": v(71.44, 385.76) * mm, "end": v(71.44, 376.24) * mm});
            skPoint(sketch, "E3.6.3.15", {"position": v(76.2, 381) * mm});
            skLineSegment(sketch, "E3.7.3.15", {"start": v(80.96, 376.24) * mm, "end": v(71.44, 376.24) * mm});
            skLineSegment(sketch, "E3.10.3.15", {"start": v(82.55, 387.35) * mm, "end": v(82.55, 374.65) * mm});
            skLineSegment(sketch, "E3.13.3.15", {"start": v(82.55, 387.35) * mm, "end": v(69.85, 387.35) * mm});
            skLineSegment(sketch, "E3.16.3.15", {"start": v(69.85, 387.35) * mm, "end": v(69.85, 374.65) * mm});
            skLineSegment(sketch, "E3.19.3.15", {"start": v(80.96, 385.76) * mm, "end": v(71.44, 385.76) * mm});
            skLineSegment(sketch, "E3.22.3.15", {"start": v(80.96, 385.76) * mm, "end": v(80.96, 376.24) * mm});
            skLineSegment(sketch, "E3.0.3.16", {"start": v(82.55, 400.05) * mm, "end": v(69.85, 400.05) * mm});
            skLineSegment(sketch, "E3.3.3.16", {"start": v(71.44, 411.16) * mm, "end": v(71.44, 401.64) * mm});
            skPoint(sketch, "E3.6.3.16", {"position": v(76.2, 406.4) * mm});
            skLineSegment(sketch, "E3.7.3.16", {"start": v(80.96, 401.64) * mm, "end": v(71.44, 401.64) * mm});
            skLineSegment(sketch, "E3.10.3.16", {"start": v(82.55, 412.75) * mm, "end": v(82.55, 400.05) * mm});
            skLineSegment(sketch, "E3.13.3.16", {"start": v(82.55, 412.75) * mm, "end": v(69.85, 412.75) * mm});
            skLineSegment(sketch, "E3.16.3.16", {"start": v(69.85, 412.75) * mm, "end": v(69.85, 400.05) * mm});
            skLineSegment(sketch, "E3.19.3.16", {"start": v(80.96, 411.16) * mm, "end": v(71.44, 411.16) * mm});
            skLineSegment(sketch, "E3.22.3.16", {"start": v(80.96, 411.16) * mm, "end": v(80.96, 401.64) * mm});
            skLineSegment(sketch, "E3.0.3.17", {"start": v(82.55, 425.45) * mm, "end": v(69.85, 425.45) * mm});
            skLineSegment(sketch, "E3.3.3.17", {"start": v(71.44, 436.56) * mm, "end": v(71.44, 427.04) * mm});
            skPoint(sketch, "E3.6.3.17", {"position": v(76.2, 431.8) * mm});
            skLineSegment(sketch, "E3.7.3.17", {"start": v(80.96, 427.04) * mm, "end": v(71.44, 427.04) * mm});
            skLineSegment(sketch, "E3.10.3.17", {"start": v(82.55, 438.15) * mm, "end": v(82.55, 425.45) * mm});
            skLineSegment(sketch, "E3.13.3.17", {"start": v(82.55, 438.15) * mm, "end": v(69.85, 438.15) * mm});
            skLineSegment(sketch, "E3.16.3.17", {"start": v(69.85, 438.15) * mm, "end": v(69.85, 425.45) * mm});
            skLineSegment(sketch, "E3.19.3.17", {"start": v(80.96, 436.56) * mm, "end": v(71.44, 436.56) * mm});
            skLineSegment(sketch, "E3.22.3.17", {"start": v(80.96, 436.56) * mm, "end": v(80.96, 427.04) * mm});
            skLineSegment(sketch, "E3.0.3.18", {"start": v(82.55, 450.85) * mm, "end": v(69.85, 450.85) * mm});
            skLineSegment(sketch, "E3.3.3.18", {"start": v(71.44, 461.96) * mm, "end": v(71.44, 452.44) * mm});
            skPoint(sketch, "E3.6.3.18", {"position": v(76.2, 457.2) * mm});
            skLineSegment(sketch, "E3.7.3.18", {"start": v(80.96, 452.44) * mm, "end": v(71.44, 452.44) * mm});
            skLineSegment(sketch, "E3.10.3.18", {"start": v(82.55, 463.55) * mm, "end": v(82.55, 450.85) * mm});
            skLineSegment(sketch, "E3.13.3.18", {"start": v(82.55, 463.55) * mm, "end": v(69.85, 463.55) * mm});
            skLineSegment(sketch, "E3.16.3.18", {"start": v(69.85, 463.55) * mm, "end": v(69.85, 450.85) * mm});
            skLineSegment(sketch, "E3.19.3.18", {"start": v(80.96, 461.96) * mm, "end": v(71.44, 461.96) * mm});
            skLineSegment(sketch, "E3.22.3.18", {"start": v(80.96, 461.96) * mm, "end": v(80.96, 452.44) * mm});
            skLineSegment(sketch, "E3.0.3.19", {"start": v(82.55, 476.25) * mm, "end": v(69.85, 476.25) * mm});
            skLineSegment(sketch, "E3.3.3.19", {"start": v(71.44, 487.36) * mm, "end": v(71.44, 477.84) * mm});
            skPoint(sketch, "E3.6.3.19", {"position": v(76.2, 482.6) * mm});
            skLineSegment(sketch, "E3.7.3.19", {"start": v(80.96, 477.84) * mm, "end": v(71.44, 477.84) * mm});
            skLineSegment(sketch, "E3.10.3.19", {"start": v(82.55, 488.95) * mm, "end": v(82.55, 476.25) * mm});
            skLineSegment(sketch, "E3.13.3.19", {"start": v(82.55, 488.95) * mm, "end": v(69.85, 488.95) * mm});
            skLineSegment(sketch, "E3.16.3.19", {"start": v(69.85, 488.95) * mm, "end": v(69.85, 476.25) * mm});
            skLineSegment(sketch, "E3.19.3.19", {"start": v(80.96, 487.36) * mm, "end": v(71.44, 487.36) * mm});
            skLineSegment(sketch, "E3.22.3.19", {"start": v(80.96, 487.36) * mm, "end": v(80.96, 477.84) * mm});
            skLineSegment(sketch, "E3.0.3.20", {"start": v(82.55, 501.65) * mm, "end": v(69.85, 501.65) * mm});
            skLineSegment(sketch, "E3.3.3.20", {"start": v(71.44, 512.76) * mm, "end": v(71.44, 503.24) * mm});
            skPoint(sketch, "E3.6.3.20", {"position": v(76.2, 508) * mm});
            skLineSegment(sketch, "E3.7.3.20", {"start": v(80.96, 503.24) * mm, "end": v(71.44, 503.24) * mm});
            skLineSegment(sketch, "E3.10.3.20", {"start": v(82.55, 514.35) * mm, "end": v(82.55, 501.65) * mm});
            skLineSegment(sketch, "E3.13.3.20", {"start": v(82.55, 514.35) * mm, "end": v(69.85, 514.35) * mm});
            skLineSegment(sketch, "E3.16.3.20", {"start": v(69.85, 514.35) * mm, "end": v(69.85, 501.65) * mm});
            skLineSegment(sketch, "E3.19.3.20", {"start": v(80.96, 512.76) * mm, "end": v(71.44, 512.76) * mm});
            skLineSegment(sketch, "E3.22.3.20", {"start": v(80.96, 512.76) * mm, "end": v(80.96, 503.24) * mm});
            skLineSegment(sketch, "E3.0.3.21", {"start": v(82.55, 527.05) * mm, "end": v(69.85, 527.05) * mm});
            skLineSegment(sketch, "E3.3.3.21", {"start": v(71.44, 538.16) * mm, "end": v(71.44, 528.64) * mm});
            skPoint(sketch, "E3.6.3.21", {"position": v(76.2, 533.4) * mm});
            skLineSegment(sketch, "E3.7.3.21", {"start": v(80.96, 528.64) * mm, "end": v(71.44, 528.64) * mm});
            skLineSegment(sketch, "E3.10.3.21", {"start": v(82.55, 539.75) * mm, "end": v(82.55, 527.05) * mm});
            skLineSegment(sketch, "E3.13.3.21", {"start": v(82.55, 539.75) * mm, "end": v(69.85, 539.75) * mm});
            skLineSegment(sketch, "E3.16.3.21", {"start": v(69.85, 539.75) * mm, "end": v(69.85, 527.05) * mm});
            skLineSegment(sketch, "E3.19.3.21", {"start": v(80.96, 538.16) * mm, "end": v(71.44, 538.16) * mm});
            skLineSegment(sketch, "E3.22.3.21", {"start": v(80.96, 538.16) * mm, "end": v(80.96, 528.64) * mm});
            skLineSegment(sketch, "E3.0.4.15", {"start": v(107.95, 374.65) * mm, "end": v(95.25, 374.65) * mm});
            skLineSegment(sketch, "E3.3.4.15", {"start": v(96.84, 385.76) * mm, "end": v(96.84, 376.24) * mm});
            skPoint(sketch, "E3.6.4.15", {"position": v(101.6, 381) * mm});
            skLineSegment(sketch, "E3.7.4.15", {"start": v(106.36, 376.24) * mm, "end": v(96.84, 376.24) * mm});
            skLineSegment(sketch, "E3.10.4.15", {"start": v(107.95, 387.35) * mm, "end": v(107.95, 374.65) * mm});
            skLineSegment(sketch, "E3.13.4.15", {"start": v(107.95, 387.35) * mm, "end": v(95.25, 387.35) * mm});
            skLineSegment(sketch, "E3.16.4.15", {"start": v(95.25, 387.35) * mm, "end": v(95.25, 374.65) * mm});
            skLineSegment(sketch, "E3.19.4.15", {"start": v(106.36, 385.76) * mm, "end": v(96.84, 385.76) * mm});
            skLineSegment(sketch, "E3.22.4.15", {"start": v(106.36, 385.76) * mm, "end": v(106.36, 376.24) * mm});
            skLineSegment(sketch, "E3.0.4.16", {"start": v(107.95, 400.05) * mm, "end": v(95.25, 400.05) * mm});
            skLineSegment(sketch, "E3.3.4.16", {"start": v(96.84, 411.16) * mm, "end": v(96.84, 401.64) * mm});
            skPoint(sketch, "E3.6.4.16", {"position": v(101.6, 406.4) * mm});
            skLineSegment(sketch, "E3.7.4.16", {"start": v(106.36, 401.64) * mm, "end": v(96.84, 401.64) * mm});
            skLineSegment(sketch, "E3.10.4.16", {"start": v(107.95, 412.75) * mm, "end": v(107.95, 400.05) * mm});
            skLineSegment(sketch, "E3.13.4.16", {"start": v(107.95, 412.75) * mm, "end": v(95.25, 412.75) * mm});
            skLineSegment(sketch, "E3.16.4.16", {"start": v(95.25, 412.75) * mm, "end": v(95.25, 400.05) * mm});
            skLineSegment(sketch, "E3.19.4.16", {"start": v(106.36, 411.16) * mm, "end": v(96.84, 411.16) * mm});
            skLineSegment(sketch, "E3.22.4.16", {"start": v(106.36, 411.16) * mm, "end": v(106.36, 401.64) * mm});
            skLineSegment(sketch, "E3.0.4.17", {"start": v(107.95, 425.45) * mm, "end": v(95.25, 425.45) * mm});
            skLineSegment(sketch, "E3.3.4.17", {"start": v(96.84, 436.56) * mm, "end": v(96.84, 427.04) * mm});
            skPoint(sketch, "E3.6.4.17", {"position": v(101.6, 431.8) * mm});
            skLineSegment(sketch, "E3.7.4.17", {"start": v(106.36, 427.04) * mm, "end": v(96.84, 427.04) * mm});
            skLineSegment(sketch, "E3.10.4.17", {"start": v(107.95, 438.15) * mm, "end": v(107.95, 425.45) * mm});
            skLineSegment(sketch, "E3.13.4.17", {"start": v(107.95, 438.15) * mm, "end": v(95.25, 438.15) * mm});
            skLineSegment(sketch, "E3.16.4.17", {"start": v(95.25, 438.15) * mm, "end": v(95.25, 425.45) * mm});
            skLineSegment(sketch, "E3.19.4.17", {"start": v(106.36, 436.56) * mm, "end": v(96.84, 436.56) * mm});
            skLineSegment(sketch, "E3.22.4.17", {"start": v(106.36, 436.56) * mm, "end": v(106.36, 427.04) * mm});
            skLineSegment(sketch, "E3.0.4.18", {"start": v(107.95, 450.85) * mm, "end": v(95.25, 450.85) * mm});
            skLineSegment(sketch, "E3.3.4.18", {"start": v(96.84, 461.96) * mm, "end": v(96.84, 452.44) * mm});
            skPoint(sketch, "E3.6.4.18", {"position": v(101.6, 457.2) * mm});
            skLineSegment(sketch, "E3.7.4.18", {"start": v(106.36, 452.44) * mm, "end": v(96.84, 452.44) * mm});
            skLineSegment(sketch, "E3.10.4.18", {"start": v(107.95, 463.55) * mm, "end": v(107.95, 450.85) * mm});
            skLineSegment(sketch, "E3.13.4.18", {"start": v(107.95, 463.55) * mm, "end": v(95.25, 463.55) * mm});
            skLineSegment(sketch, "E3.16.4.18", {"start": v(95.25, 463.55) * mm, "end": v(95.25, 450.85) * mm});
            skLineSegment(sketch, "E3.19.4.18", {"start": v(106.36, 461.96) * mm, "end": v(96.84, 461.96) * mm});
            skLineSegment(sketch, "E3.22.4.18", {"start": v(106.36, 461.96) * mm, "end": v(106.36, 452.44) * mm});
            skLineSegment(sketch, "E3.0.4.19", {"start": v(107.95, 476.25) * mm, "end": v(95.25, 476.25) * mm});
            skLineSegment(sketch, "E3.3.4.19", {"start": v(96.84, 487.36) * mm, "end": v(96.84, 477.84) * mm});
            skPoint(sketch, "E3.6.4.19", {"position": v(101.6, 482.6) * mm});
            skLineSegment(sketch, "E3.7.4.19", {"start": v(106.36, 477.84) * mm, "end": v(96.84, 477.84) * mm});
            skLineSegment(sketch, "E3.10.4.19", {"start": v(107.95, 488.95) * mm, "end": v(107.95, 476.25) * mm});
            skLineSegment(sketch, "E3.13.4.19", {"start": v(107.95, 488.95) * mm, "end": v(95.25, 488.95) * mm});
            skLineSegment(sketch, "E3.16.4.19", {"start": v(95.25, 488.95) * mm, "end": v(95.25, 476.25) * mm});
            skLineSegment(sketch, "E3.19.4.19", {"start": v(106.36, 487.36) * mm, "end": v(96.84, 487.36) * mm});
            skLineSegment(sketch, "E3.22.4.19", {"start": v(106.36, 487.36) * mm, "end": v(106.36, 477.84) * mm});
            skLineSegment(sketch, "E3.0.4.20", {"start": v(107.95, 501.65) * mm, "end": v(95.25, 501.65) * mm});
            skLineSegment(sketch, "E3.3.4.20", {"start": v(96.84, 512.76) * mm, "end": v(96.84, 503.24) * mm});
            skPoint(sketch, "E3.6.4.20", {"position": v(101.6, 508) * mm});
            skLineSegment(sketch, "E3.7.4.20", {"start": v(106.36, 503.24) * mm, "end": v(96.84, 503.24) * mm});
            skLineSegment(sketch, "E3.10.4.20", {"start": v(107.95, 514.35) * mm, "end": v(107.95, 501.65) * mm});
            skLineSegment(sketch, "E3.13.4.20", {"start": v(107.95, 514.35) * mm, "end": v(95.25, 514.35) * mm});
            skLineSegment(sketch, "E3.16.4.20", {"start": v(95.25, 514.35) * mm, "end": v(95.25, 501.65) * mm});
            skLineSegment(sketch, "E3.19.4.20", {"start": v(106.36, 512.76) * mm, "end": v(96.84, 512.76) * mm});
            skLineSegment(sketch, "E3.22.4.20", {"start": v(106.36, 512.76) * mm, "end": v(106.36, 503.24) * mm});
            skLineSegment(sketch, "E3.0.4.21", {"start": v(107.95, 527.05) * mm, "end": v(95.25, 527.05) * mm});
            skLineSegment(sketch, "E3.3.4.21", {"start": v(96.84, 538.16) * mm, "end": v(96.84, 528.64) * mm});
            skPoint(sketch, "E3.6.4.21", {"position": v(101.6, 533.4) * mm});
            skLineSegment(sketch, "E3.7.4.21", {"start": v(106.36, 528.64) * mm, "end": v(96.84, 528.64) * mm});
            skLineSegment(sketch, "E3.10.4.21", {"start": v(107.95, 539.75) * mm, "end": v(107.95, 527.05) * mm});
            skLineSegment(sketch, "E3.13.4.21", {"start": v(107.95, 539.75) * mm, "end": v(95.25, 539.75) * mm});
            skLineSegment(sketch, "E3.16.4.21", {"start": v(95.25, 539.75) * mm, "end": v(95.25, 527.05) * mm});
            skLineSegment(sketch, "E3.19.4.21", {"start": v(106.36, 538.16) * mm, "end": v(96.84, 538.16) * mm});
            skLineSegment(sketch, "E3.22.4.21", {"start": v(106.36, 538.16) * mm, "end": v(106.36, 528.64) * mm});
            skLineSegment(sketch, "E3.0.5.15", {"start": v(133.35, 374.65) * mm, "end": v(120.65, 374.65) * mm});
            skLineSegment(sketch, "E3.3.5.15", {"start": v(122.24, 385.76) * mm, "end": v(122.24, 376.24) * mm});
            skPoint(sketch, "E3.6.5.15", {"position": v(127, 381) * mm});
            skLineSegment(sketch, "E3.7.5.15", {"start": v(131.76, 376.24) * mm, "end": v(122.24, 376.24) * mm});
            skLineSegment(sketch, "E3.10.5.15", {"start": v(133.35, 387.35) * mm, "end": v(133.35, 374.65) * mm});
            skLineSegment(sketch, "E3.13.5.15", {"start": v(133.35, 387.35) * mm, "end": v(120.65, 387.35) * mm});
            skLineSegment(sketch, "E3.16.5.15", {"start": v(120.65, 387.35) * mm, "end": v(120.65, 374.65) * mm});
            skLineSegment(sketch, "E3.19.5.15", {"start": v(131.76, 385.76) * mm, "end": v(122.24, 385.76) * mm});
            skLineSegment(sketch, "E3.22.5.15", {"start": v(131.76, 385.76) * mm, "end": v(131.76, 376.24) * mm});
            skLineSegment(sketch, "E3.0.5.16", {"start": v(133.35, 400.05) * mm, "end": v(120.65, 400.05) * mm});
            skLineSegment(sketch, "E3.3.5.16", {"start": v(122.24, 411.16) * mm, "end": v(122.24, 401.64) * mm});
            skPoint(sketch, "E3.6.5.16", {"position": v(127, 406.4) * mm});
            skLineSegment(sketch, "E3.7.5.16", {"start": v(131.76, 401.64) * mm, "end": v(122.24, 401.64) * mm});
            skLineSegment(sketch, "E3.10.5.16", {"start": v(133.35, 412.75) * mm, "end": v(133.35, 400.05) * mm});
            skLineSegment(sketch, "E3.13.5.16", {"start": v(133.35, 412.75) * mm, "end": v(120.65, 412.75) * mm});
            skLineSegment(sketch, "E3.16.5.16", {"start": v(120.65, 412.75) * mm, "end": v(120.65, 400.05) * mm});
            skLineSegment(sketch, "E3.19.5.16", {"start": v(131.76, 411.16) * mm, "end": v(122.24, 411.16) * mm});
            skLineSegment(sketch, "E3.22.5.16", {"start": v(131.76, 411.16) * mm, "end": v(131.76, 401.64) * mm});
            skLineSegment(sketch, "E3.0.5.17", {"start": v(133.35, 425.45) * mm, "end": v(120.65, 425.45) * mm});
            skLineSegment(sketch, "E3.3.5.17", {"start": v(122.24, 436.56) * mm, "end": v(122.24, 427.04) * mm});
            skPoint(sketch, "E3.6.5.17", {"position": v(127, 431.8) * mm});
            skLineSegment(sketch, "E3.7.5.17", {"start": v(131.76, 427.04) * mm, "end": v(122.24, 427.04) * mm});
            skLineSegment(sketch, "E3.10.5.17", {"start": v(133.35, 438.15) * mm, "end": v(133.35, 425.45) * mm});
            skLineSegment(sketch, "E3.13.5.17", {"start": v(133.35, 438.15) * mm, "end": v(120.65, 438.15) * mm});
            skLineSegment(sketch, "E3.16.5.17", {"start": v(120.65, 438.15) * mm, "end": v(120.65, 425.45) * mm});
            skLineSegment(sketch, "E3.19.5.17", {"start": v(131.76, 436.56) * mm, "end": v(122.24, 436.56) * mm});
            skLineSegment(sketch, "E3.22.5.17", {"start": v(131.76, 436.56) * mm, "end": v(131.76, 427.04) * mm});
            skLineSegment(sketch, "E3.0.5.18", {"start": v(133.35, 450.85) * mm, "end": v(120.65, 450.85) * mm});
            skLineSegment(sketch, "E3.3.5.18", {"start": v(122.24, 461.96) * mm, "end": v(122.24, 452.44) * mm});
            skPoint(sketch, "E3.6.5.18", {"position": v(127, 457.2) * mm});
            skLineSegment(sketch, "E3.7.5.18", {"start": v(131.76, 452.44) * mm, "end": v(122.24, 452.44) * mm});
            skLineSegment(sketch, "E3.10.5.18", {"start": v(133.35, 463.55) * mm, "end": v(133.35, 450.85) * mm});
            skLineSegment(sketch, "E3.13.5.18", {"start": v(133.35, 463.55) * mm, "end": v(120.65, 463.55) * mm});
            skLineSegment(sketch, "E3.16.5.18", {"start": v(120.65, 463.55) * mm, "end": v(120.65, 450.85) * mm});
            skLineSegment(sketch, "E3.19.5.18", {"start": v(131.76, 461.96) * mm, "end": v(122.24, 461.96) * mm});
            skLineSegment(sketch, "E3.22.5.18", {"start": v(131.76, 461.96) * mm, "end": v(131.76, 452.44) * mm});
            skLineSegment(sketch, "E3.0.5.19", {"start": v(133.35, 476.25) * mm, "end": v(120.65, 476.25) * mm});
            skLineSegment(sketch, "E3.3.5.19", {"start": v(122.24, 487.36) * mm, "end": v(122.24, 477.84) * mm});
            skPoint(sketch, "E3.6.5.19", {"position": v(127, 482.6) * mm});
            skLineSegment(sketch, "E3.7.5.19", {"start": v(131.76, 477.84) * mm, "end": v(122.24, 477.84) * mm});
            skLineSegment(sketch, "E3.10.5.19", {"start": v(133.35, 488.95) * mm, "end": v(133.35, 476.25) * mm});
            skLineSegment(sketch, "E3.13.5.19", {"start": v(133.35, 488.95) * mm, "end": v(120.65, 488.95) * mm});
            skLineSegment(sketch, "E3.16.5.19", {"start": v(120.65, 488.95) * mm, "end": v(120.65, 476.25) * mm});
            skLineSegment(sketch, "E3.19.5.19", {"start": v(131.76, 487.36) * mm, "end": v(122.24, 487.36) * mm});
            skLineSegment(sketch, "E3.22.5.19", {"start": v(131.76, 487.36) * mm, "end": v(131.76, 477.84) * mm});
            skLineSegment(sketch, "E3.0.5.20", {"start": v(133.35, 501.65) * mm, "end": v(120.65, 501.65) * mm});
            skLineSegment(sketch, "E3.3.5.20", {"start": v(122.24, 512.76) * mm, "end": v(122.24, 503.24) * mm});
            skPoint(sketch, "E3.6.5.20", {"position": v(127, 508) * mm});
            skLineSegment(sketch, "E3.7.5.20", {"start": v(131.76, 503.24) * mm, "end": v(122.24, 503.24) * mm});
            skLineSegment(sketch, "E3.10.5.20", {"start": v(133.35, 514.35) * mm, "end": v(133.35, 501.65) * mm});
            skLineSegment(sketch, "E3.13.5.20", {"start": v(133.35, 514.35) * mm, "end": v(120.65, 514.35) * mm});
            skLineSegment(sketch, "E3.16.5.20", {"start": v(120.65, 514.35) * mm, "end": v(120.65, 501.65) * mm});
            skLineSegment(sketch, "E3.19.5.20", {"start": v(131.76, 512.76) * mm, "end": v(122.24, 512.76) * mm});
            skLineSegment(sketch, "E3.22.5.20", {"start": v(131.76, 512.76) * mm, "end": v(131.76, 503.24) * mm});
            skLineSegment(sketch, "E3.0.5.21", {"start": v(133.35, 527.05) * mm, "end": v(120.65, 527.05) * mm});
            skLineSegment(sketch, "E3.3.5.21", {"start": v(122.24, 538.16) * mm, "end": v(122.24, 528.64) * mm});
            skPoint(sketch, "E3.6.5.21", {"position": v(127, 533.4) * mm});
            skLineSegment(sketch, "E3.7.5.21", {"start": v(131.76, 528.64) * mm, "end": v(122.24, 528.64) * mm});
            skLineSegment(sketch, "E3.10.5.21", {"start": v(133.35, 539.75) * mm, "end": v(133.35, 527.05) * mm});
            skLineSegment(sketch, "E3.13.5.21", {"start": v(133.35, 539.75) * mm, "end": v(120.65, 539.75) * mm});
            skLineSegment(sketch, "E3.16.5.21", {"start": v(120.65, 539.75) * mm, "end": v(120.65, 527.05) * mm});
            skLineSegment(sketch, "E3.19.5.21", {"start": v(131.76, 538.16) * mm, "end": v(122.24, 538.16) * mm});
            skLineSegment(sketch, "E3.22.5.21", {"start": v(131.76, 538.16) * mm, "end": v(131.76, 528.64) * mm});
            skLineSegment(sketch, "E3.0.6.15", {"start": v(158.75, 374.65) * mm, "end": v(146.05, 374.65) * mm});
            skLineSegment(sketch, "E3.3.6.15", {"start": v(147.64, 385.76) * mm, "end": v(147.64, 376.24) * mm});
            skPoint(sketch, "E3.6.6.15", {"position": v(152.4, 381) * mm});
            skLineSegment(sketch, "E3.7.6.15", {"start": v(157.16, 376.24) * mm, "end": v(147.64, 376.24) * mm});
            skLineSegment(sketch, "E3.10.6.15", {"start": v(158.75, 387.35) * mm, "end": v(158.75, 374.65) * mm});
            skLineSegment(sketch, "E3.13.6.15", {"start": v(158.75, 387.35) * mm, "end": v(146.05, 387.35) * mm});
            skLineSegment(sketch, "E3.16.6.15", {"start": v(146.05, 387.35) * mm, "end": v(146.05, 374.65) * mm});
            skLineSegment(sketch, "E3.19.6.15", {"start": v(157.16, 385.76) * mm, "end": v(147.64, 385.76) * mm});
            skLineSegment(sketch, "E3.22.6.15", {"start": v(157.16, 385.76) * mm, "end": v(157.16, 376.24) * mm});
            skLineSegment(sketch, "E3.0.6.16", {"start": v(158.75, 400.05) * mm, "end": v(146.05, 400.05) * mm});
            skLineSegment(sketch, "E3.3.6.16", {"start": v(147.64, 411.16) * mm, "end": v(147.64, 401.64) * mm});
            skPoint(sketch, "E3.6.6.16", {"position": v(152.4, 406.4) * mm});
            skLineSegment(sketch, "E3.7.6.16", {"start": v(157.16, 401.64) * mm, "end": v(147.64, 401.64) * mm});
            skLineSegment(sketch, "E3.10.6.16", {"start": v(158.75, 412.75) * mm, "end": v(158.75, 400.05) * mm});
            skLineSegment(sketch, "E3.13.6.16", {"start": v(158.75, 412.75) * mm, "end": v(146.05, 412.75) * mm});
            skLineSegment(sketch, "E3.16.6.16", {"start": v(146.05, 412.75) * mm, "end": v(146.05, 400.05) * mm});
            skLineSegment(sketch, "E3.19.6.16", {"start": v(157.16, 411.16) * mm, "end": v(147.64, 411.16) * mm});
            skLineSegment(sketch, "E3.22.6.16", {"start": v(157.16, 411.16) * mm, "end": v(157.16, 401.64) * mm});
            skLineSegment(sketch, "E3.0.6.17", {"start": v(158.75, 425.45) * mm, "end": v(146.05, 425.45) * mm});
            skLineSegment(sketch, "E3.3.6.17", {"start": v(147.64, 436.56) * mm, "end": v(147.64, 427.04) * mm});
            skPoint(sketch, "E3.6.6.17", {"position": v(152.4, 431.8) * mm});
            skLineSegment(sketch, "E3.7.6.17", {"start": v(157.16, 427.04) * mm, "end": v(147.64, 427.04) * mm});
            skLineSegment(sketch, "E3.10.6.17", {"start": v(158.75, 438.15) * mm, "end": v(158.75, 425.45) * mm});
            skLineSegment(sketch, "E3.13.6.17", {"start": v(158.75, 438.15) * mm, "end": v(146.05, 438.15) * mm});
            skLineSegment(sketch, "E3.16.6.17", {"start": v(146.05, 438.15) * mm, "end": v(146.05, 425.45) * mm});
            skLineSegment(sketch, "E3.19.6.17", {"start": v(157.16, 436.56) * mm, "end": v(147.64, 436.56) * mm});
            skLineSegment(sketch, "E3.22.6.17", {"start": v(157.16, 436.56) * mm, "end": v(157.16, 427.04) * mm});
            skLineSegment(sketch, "E3.0.6.18", {"start": v(158.75, 450.85) * mm, "end": v(146.05, 450.85) * mm});
            skLineSegment(sketch, "E3.3.6.18", {"start": v(147.64, 461.96) * mm, "end": v(147.64, 452.44) * mm});
            skPoint(sketch, "E3.6.6.18", {"position": v(152.4, 457.2) * mm});
            skLineSegment(sketch, "E3.7.6.18", {"start": v(157.16, 452.44) * mm, "end": v(147.64, 452.44) * mm});
            skLineSegment(sketch, "E3.10.6.18", {"start": v(158.75, 463.55) * mm, "end": v(158.75, 450.85) * mm});
            skLineSegment(sketch, "E3.13.6.18", {"start": v(158.75, 463.55) * mm, "end": v(146.05, 463.55) * mm});
            skLineSegment(sketch, "E3.16.6.18", {"start": v(146.05, 463.55) * mm, "end": v(146.05, 450.85) * mm});
            skLineSegment(sketch, "E3.19.6.18", {"start": v(157.16, 461.96) * mm, "end": v(147.64, 461.96) * mm});
            skLineSegment(sketch, "E3.22.6.18", {"start": v(157.16, 461.96) * mm, "end": v(157.16, 452.44) * mm});
            skLineSegment(sketch, "E3.0.6.19", {"start": v(158.75, 476.25) * mm, "end": v(146.05, 476.25) * mm});
            skLineSegment(sketch, "E3.3.6.19", {"start": v(147.64, 487.36) * mm, "end": v(147.64, 477.84) * mm});
            skPoint(sketch, "E3.6.6.19", {"position": v(152.4, 482.6) * mm});
            skLineSegment(sketch, "E3.7.6.19", {"start": v(157.16, 477.84) * mm, "end": v(147.64, 477.84) * mm});
            skLineSegment(sketch, "E3.10.6.19", {"start": v(158.75, 488.95) * mm, "end": v(158.75, 476.25) * mm});
            skLineSegment(sketch, "E3.13.6.19", {"start": v(158.75, 488.95) * mm, "end": v(146.05, 488.95) * mm});
            skLineSegment(sketch, "E3.16.6.19", {"start": v(146.05, 488.95) * mm, "end": v(146.05, 476.25) * mm});
            skLineSegment(sketch, "E3.19.6.19", {"start": v(157.16, 487.36) * mm, "end": v(147.64, 487.36) * mm});
            skLineSegment(sketch, "E3.22.6.19", {"start": v(157.16, 487.36) * mm, "end": v(157.16, 477.84) * mm});
            skLineSegment(sketch, "E3.0.6.20", {"start": v(158.75, 501.65) * mm, "end": v(146.05, 501.65) * mm});
            skLineSegment(sketch, "E3.3.6.20", {"start": v(147.64, 512.76) * mm, "end": v(147.64, 503.24) * mm});
            skPoint(sketch, "E3.6.6.20", {"position": v(152.4, 508) * mm});
            skLineSegment(sketch, "E3.7.6.20", {"start": v(157.16, 503.24) * mm, "end": v(147.64, 503.24) * mm});
            skLineSegment(sketch, "E3.10.6.20", {"start": v(158.75, 514.35) * mm, "end": v(158.75, 501.65) * mm});
            skLineSegment(sketch, "E3.13.6.20", {"start": v(158.75, 514.35) * mm, "end": v(146.05, 514.35) * mm});
            skLineSegment(sketch, "E3.16.6.20", {"start": v(146.05, 514.35) * mm, "end": v(146.05, 501.65) * mm});
            skLineSegment(sketch, "E3.19.6.20", {"start": v(157.16, 512.76) * mm, "end": v(147.64, 512.76) * mm});
            skLineSegment(sketch, "E3.22.6.20", {"start": v(157.16, 512.76) * mm, "end": v(157.16, 503.24) * mm});
            skLineSegment(sketch, "E3.0.6.21", {"start": v(158.75, 527.05) * mm, "end": v(146.05, 527.05) * mm});
            skLineSegment(sketch, "E3.3.6.21", {"start": v(147.64, 538.16) * mm, "end": v(147.64, 528.64) * mm});
            skPoint(sketch, "E3.6.6.21", {"position": v(152.4, 533.4) * mm});
            skLineSegment(sketch, "E3.7.6.21", {"start": v(157.16, 528.64) * mm, "end": v(147.64, 528.64) * mm});
            skLineSegment(sketch, "E3.10.6.21", {"start": v(158.75, 539.75) * mm, "end": v(158.75, 527.05) * mm});
            skLineSegment(sketch, "E3.13.6.21", {"start": v(158.75, 539.75) * mm, "end": v(146.05, 539.75) * mm});
            skLineSegment(sketch, "E3.16.6.21", {"start": v(146.05, 539.75) * mm, "end": v(146.05, 527.05) * mm});
            skLineSegment(sketch, "E3.19.6.21", {"start": v(157.16, 538.16) * mm, "end": v(147.64, 538.16) * mm});
            skLineSegment(sketch, "E3.22.6.21", {"start": v(157.16, 538.16) * mm, "end": v(157.16, 528.64) * mm});
            skLineSegment(sketch, "E3.0.7.15", {"start": v(184.15, 374.65) * mm, "end": v(171.45, 374.65) * mm});
            skLineSegment(sketch, "E3.3.7.15", {"start": v(173.04, 385.76) * mm, "end": v(173.04, 376.24) * mm});
            skPoint(sketch, "E3.6.7.15", {"position": v(177.8, 381) * mm});
            skLineSegment(sketch, "E3.7.7.15", {"start": v(182.56, 376.24) * mm, "end": v(173.04, 376.24) * mm});
            skLineSegment(sketch, "E3.10.7.15", {"start": v(184.15, 387.35) * mm, "end": v(184.15, 374.65) * mm});
            skLineSegment(sketch, "E3.13.7.15", {"start": v(184.15, 387.35) * mm, "end": v(171.45, 387.35) * mm});
            skLineSegment(sketch, "E3.16.7.15", {"start": v(171.45, 387.35) * mm, "end": v(171.45, 374.65) * mm});
            skLineSegment(sketch, "E3.19.7.15", {"start": v(182.56, 385.76) * mm, "end": v(173.04, 385.76) * mm});
            skLineSegment(sketch, "E3.22.7.15", {"start": v(182.56, 385.76) * mm, "end": v(182.56, 376.24) * mm});
            skLineSegment(sketch, "E3.0.7.16", {"start": v(184.15, 400.05) * mm, "end": v(171.45, 400.05) * mm});
            skLineSegment(sketch, "E3.3.7.16", {"start": v(173.04, 411.16) * mm, "end": v(173.04, 401.64) * mm});
            skPoint(sketch, "E3.6.7.16", {"position": v(177.8, 406.4) * mm});
            skLineSegment(sketch, "E3.7.7.16", {"start": v(182.56, 401.64) * mm, "end": v(173.04, 401.64) * mm});
            skLineSegment(sketch, "E3.10.7.16", {"start": v(184.15, 412.75) * mm, "end": v(184.15, 400.05) * mm});
            skLineSegment(sketch, "E3.13.7.16", {"start": v(184.15, 412.75) * mm, "end": v(171.45, 412.75) * mm});
            skLineSegment(sketch, "E3.16.7.16", {"start": v(171.45, 412.75) * mm, "end": v(171.45, 400.05) * mm});
            skLineSegment(sketch, "E3.19.7.16", {"start": v(182.56, 411.16) * mm, "end": v(173.04, 411.16) * mm});
            skLineSegment(sketch, "E3.22.7.16", {"start": v(182.56, 411.16) * mm, "end": v(182.56, 401.64) * mm});
            skLineSegment(sketch, "E3.0.7.17", {"start": v(184.15, 425.45) * mm, "end": v(171.45, 425.45) * mm});
            skLineSegment(sketch, "E3.3.7.17", {"start": v(173.04, 436.56) * mm, "end": v(173.04, 427.04) * mm});
            skPoint(sketch, "E3.6.7.17", {"position": v(177.8, 431.8) * mm});
            skLineSegment(sketch, "E3.7.7.17", {"start": v(182.56, 427.04) * mm, "end": v(173.04, 427.04) * mm});
            skLineSegment(sketch, "E3.10.7.17", {"start": v(184.15, 438.15) * mm, "end": v(184.15, 425.45) * mm});
            skLineSegment(sketch, "E3.13.7.17", {"start": v(184.15, 438.15) * mm, "end": v(171.45, 438.15) * mm});
            skLineSegment(sketch, "E3.16.7.17", {"start": v(171.45, 438.15) * mm, "end": v(171.45, 425.45) * mm});
            skLineSegment(sketch, "E3.19.7.17", {"start": v(182.56, 436.56) * mm, "end": v(173.04, 436.56) * mm});
            skLineSegment(sketch, "E3.22.7.17", {"start": v(182.56, 436.56) * mm, "end": v(182.56, 427.04) * mm});
            skLineSegment(sketch, "E3.0.7.18", {"start": v(184.15, 450.85) * mm, "end": v(171.45, 450.85) * mm});
            skLineSegment(sketch, "E3.3.7.18", {"start": v(173.04, 461.96) * mm, "end": v(173.04, 452.44) * mm});
            skPoint(sketch, "E3.6.7.18", {"position": v(177.8, 457.2) * mm});
            skLineSegment(sketch, "E3.7.7.18", {"start": v(182.56, 452.44) * mm, "end": v(173.04, 452.44) * mm});
            skLineSegment(sketch, "E3.10.7.18", {"start": v(184.15, 463.55) * mm, "end": v(184.15, 450.85) * mm});
            skLineSegment(sketch, "E3.13.7.18", {"start": v(184.15, 463.55) * mm, "end": v(171.45, 463.55) * mm});
            skLineSegment(sketch, "E3.16.7.18", {"start": v(171.45, 463.55) * mm, "end": v(171.45, 450.85) * mm});
            skLineSegment(sketch, "E3.19.7.18", {"start": v(182.56, 461.96) * mm, "end": v(173.04, 461.96) * mm});
            skLineSegment(sketch, "E3.22.7.18", {"start": v(182.56, 461.96) * mm, "end": v(182.56, 452.44) * mm});
            skLineSegment(sketch, "E3.0.7.19", {"start": v(184.15, 476.25) * mm, "end": v(171.45, 476.25) * mm});
            skLineSegment(sketch, "E3.3.7.19", {"start": v(173.04, 487.36) * mm, "end": v(173.04, 477.84) * mm});
            skPoint(sketch, "E3.6.7.19", {"position": v(177.8, 482.6) * mm});
            skLineSegment(sketch, "E3.7.7.19", {"start": v(182.56, 477.84) * mm, "end": v(173.04, 477.84) * mm});
            skLineSegment(sketch, "E3.10.7.19", {"start": v(184.15, 488.95) * mm, "end": v(184.15, 476.25) * mm});
            skLineSegment(sketch, "E3.13.7.19", {"start": v(184.15, 488.95) * mm, "end": v(171.45, 488.95) * mm});
            skLineSegment(sketch, "E3.16.7.19", {"start": v(171.45, 488.95) * mm, "end": v(171.45, 476.25) * mm});
            skLineSegment(sketch, "E3.19.7.19", {"start": v(182.56, 487.36) * mm, "end": v(173.04, 487.36) * mm});
            skLineSegment(sketch, "E3.22.7.19", {"start": v(182.56, 487.36) * mm, "end": v(182.56, 477.84) * mm});
            skLineSegment(sketch, "E3.0.7.20", {"start": v(184.15, 501.65) * mm, "end": v(171.45, 501.65) * mm});
            skLineSegment(sketch, "E3.3.7.20", {"start": v(173.04, 512.76) * mm, "end": v(173.04, 503.24) * mm});
            skPoint(sketch, "E3.6.7.20", {"position": v(177.8, 508) * mm});
            skLineSegment(sketch, "E3.7.7.20", {"start": v(182.56, 503.24) * mm, "end": v(173.04, 503.24) * mm});
            skLineSegment(sketch, "E3.10.7.20", {"start": v(184.15, 514.35) * mm, "end": v(184.15, 501.65) * mm});
            skLineSegment(sketch, "E3.13.7.20", {"start": v(184.15, 514.35) * mm, "end": v(171.45, 514.35) * mm});
            skLineSegment(sketch, "E3.16.7.20", {"start": v(171.45, 514.35) * mm, "end": v(171.45, 501.65) * mm});
            skLineSegment(sketch, "E3.19.7.20", {"start": v(182.56, 512.76) * mm, "end": v(173.04, 512.76) * mm});
            skLineSegment(sketch, "E3.22.7.20", {"start": v(182.56, 512.76) * mm, "end": v(182.56, 503.24) * mm});
            skLineSegment(sketch, "E3.0.7.21", {"start": v(184.15, 527.05) * mm, "end": v(171.45, 527.05) * mm});
            skLineSegment(sketch, "E3.3.7.21", {"start": v(173.04, 538.16) * mm, "end": v(173.04, 528.64) * mm});
            skPoint(sketch, "E3.6.7.21", {"position": v(177.8, 533.4) * mm});
            skLineSegment(sketch, "E3.7.7.21", {"start": v(182.56, 528.64) * mm, "end": v(173.04, 528.64) * mm});
            skLineSegment(sketch, "E3.10.7.21", {"start": v(184.15, 539.75) * mm, "end": v(184.15, 527.05) * mm});
            skLineSegment(sketch, "E3.13.7.21", {"start": v(184.15, 539.75) * mm, "end": v(171.45, 539.75) * mm});
            skLineSegment(sketch, "E3.16.7.21", {"start": v(171.45, 539.75) * mm, "end": v(171.45, 527.05) * mm});
            skLineSegment(sketch, "E3.19.7.21", {"start": v(182.56, 538.16) * mm, "end": v(173.04, 538.16) * mm});
            skLineSegment(sketch, "E3.22.7.21", {"start": v(182.56, 538.16) * mm, "end": v(182.56, 528.64) * mm});
            skLineSegment(sketch, "E3.0.8.15", {"start": v(209.55, 374.65) * mm, "end": v(196.85, 374.65) * mm});
            skLineSegment(sketch, "E3.3.8.15", {"start": v(198.44, 385.76) * mm, "end": v(198.44, 376.24) * mm});
            skPoint(sketch, "E3.6.8.15", {"position": v(203.2, 381) * mm});
            skLineSegment(sketch, "E3.7.8.15", {"start": v(207.96, 376.24) * mm, "end": v(198.44, 376.24) * mm});
            skLineSegment(sketch, "E3.10.8.15", {"start": v(209.55, 387.35) * mm, "end": v(209.55, 374.65) * mm});
            skLineSegment(sketch, "E3.13.8.15", {"start": v(209.55, 387.35) * mm, "end": v(196.85, 387.35) * mm});
            skLineSegment(sketch, "E3.16.8.15", {"start": v(196.85, 387.35) * mm, "end": v(196.85, 374.65) * mm});
            skLineSegment(sketch, "E3.19.8.15", {"start": v(207.96, 385.76) * mm, "end": v(198.44, 385.76) * mm});
            skLineSegment(sketch, "E3.22.8.15", {"start": v(207.96, 385.76) * mm, "end": v(207.96, 376.24) * mm});
            skLineSegment(sketch, "E3.0.8.16", {"start": v(209.55, 400.05) * mm, "end": v(196.85, 400.05) * mm});
            skLineSegment(sketch, "E3.3.8.16", {"start": v(198.44, 411.16) * mm, "end": v(198.44, 401.64) * mm});
            skPoint(sketch, "E3.6.8.16", {"position": v(203.2, 406.4) * mm});
            skLineSegment(sketch, "E3.7.8.16", {"start": v(207.96, 401.64) * mm, "end": v(198.44, 401.64) * mm});
            skLineSegment(sketch, "E3.10.8.16", {"start": v(209.55, 412.75) * mm, "end": v(209.55, 400.05) * mm});
            skLineSegment(sketch, "E3.13.8.16", {"start": v(209.55, 412.75) * mm, "end": v(196.85, 412.75) * mm});
            skLineSegment(sketch, "E3.16.8.16", {"start": v(196.85, 412.75) * mm, "end": v(196.85, 400.05) * mm});
            skLineSegment(sketch, "E3.19.8.16", {"start": v(207.96, 411.16) * mm, "end": v(198.44, 411.16) * mm});
            skLineSegment(sketch, "E3.22.8.16", {"start": v(207.96, 411.16) * mm, "end": v(207.96, 401.64) * mm});
            skLineSegment(sketch, "E3.0.8.17", {"start": v(209.55, 425.45) * mm, "end": v(196.85, 425.45) * mm});
            skLineSegment(sketch, "E3.3.8.17", {"start": v(198.44, 436.56) * mm, "end": v(198.44, 427.04) * mm});
            skPoint(sketch, "E3.6.8.17", {"position": v(203.2, 431.8) * mm});
            skLineSegment(sketch, "E3.7.8.17", {"start": v(207.96, 427.04) * mm, "end": v(198.44, 427.04) * mm});
            skLineSegment(sketch, "E3.10.8.17", {"start": v(209.55, 438.15) * mm, "end": v(209.55, 425.45) * mm});
            skLineSegment(sketch, "E3.13.8.17", {"start": v(209.55, 438.15) * mm, "end": v(196.85, 438.15) * mm});
            skLineSegment(sketch, "E3.16.8.17", {"start": v(196.85, 438.15) * mm, "end": v(196.85, 425.45) * mm});
            skLineSegment(sketch, "E3.19.8.17", {"start": v(207.96, 436.56) * mm, "end": v(198.44, 436.56) * mm});
            skLineSegment(sketch, "E3.22.8.17", {"start": v(207.96, 436.56) * mm, "end": v(207.96, 427.04) * mm});
            skLineSegment(sketch, "E3.0.8.18", {"start": v(209.55, 450.85) * mm, "end": v(196.85, 450.85) * mm});
            skLineSegment(sketch, "E3.3.8.18", {"start": v(198.44, 461.96) * mm, "end": v(198.44, 452.44) * mm});
            skPoint(sketch, "E3.6.8.18", {"position": v(203.2, 457.2) * mm});
            skLineSegment(sketch, "E3.7.8.18", {"start": v(207.96, 452.44) * mm, "end": v(198.44, 452.44) * mm});
            skLineSegment(sketch, "E3.10.8.18", {"start": v(209.55, 463.55) * mm, "end": v(209.55, 450.85) * mm});
            skLineSegment(sketch, "E3.13.8.18", {"start": v(209.55, 463.55) * mm, "end": v(196.85, 463.55) * mm});
            skLineSegment(sketch, "E3.16.8.18", {"start": v(196.85, 463.55) * mm, "end": v(196.85, 450.85) * mm});
            skLineSegment(sketch, "E3.19.8.18", {"start": v(207.96, 461.96) * mm, "end": v(198.44, 461.96) * mm});
            skLineSegment(sketch, "E3.22.8.18", {"start": v(207.96, 461.96) * mm, "end": v(207.96, 452.44) * mm});
            skLineSegment(sketch, "E3.0.8.19", {"start": v(209.55, 476.25) * mm, "end": v(196.85, 476.25) * mm});
            skLineSegment(sketch, "E3.3.8.19", {"start": v(198.44, 487.36) * mm, "end": v(198.44, 477.84) * mm});
            skPoint(sketch, "E3.6.8.19", {"position": v(203.2, 482.6) * mm});
            skLineSegment(sketch, "E3.7.8.19", {"start": v(207.96, 477.84) * mm, "end": v(198.44, 477.84) * mm});
            skLineSegment(sketch, "E3.10.8.19", {"start": v(209.55, 488.95) * mm, "end": v(209.55, 476.25) * mm});
            skLineSegment(sketch, "E3.13.8.19", {"start": v(209.55, 488.95) * mm, "end": v(196.85, 488.95) * mm});
            skLineSegment(sketch, "E3.16.8.19", {"start": v(196.85, 488.95) * mm, "end": v(196.85, 476.25) * mm});
            skLineSegment(sketch, "E3.19.8.19", {"start": v(207.96, 487.36) * mm, "end": v(198.44, 487.36) * mm});
            skLineSegment(sketch, "E3.22.8.19", {"start": v(207.96, 487.36) * mm, "end": v(207.96, 477.84) * mm});
            skLineSegment(sketch, "E3.0.8.20", {"start": v(209.55, 501.65) * mm, "end": v(196.85, 501.65) * mm});
            skLineSegment(sketch, "E3.3.8.20", {"start": v(198.44, 512.76) * mm, "end": v(198.44, 503.24) * mm});
            skPoint(sketch, "E3.6.8.20", {"position": v(203.2, 508) * mm});
            skLineSegment(sketch, "E3.7.8.20", {"start": v(207.96, 503.24) * mm, "end": v(198.44, 503.24) * mm});
            skLineSegment(sketch, "E3.10.8.20", {"start": v(209.55, 514.35) * mm, "end": v(209.55, 501.65) * mm});
            skLineSegment(sketch, "E3.13.8.20", {"start": v(209.55, 514.35) * mm, "end": v(196.85, 514.35) * mm});
            skLineSegment(sketch, "E3.16.8.20", {"start": v(196.85, 514.35) * mm, "end": v(196.85, 501.65) * mm});
            skLineSegment(sketch, "E3.19.8.20", {"start": v(207.96, 512.76) * mm, "end": v(198.44, 512.76) * mm});
            skLineSegment(sketch, "E3.22.8.20", {"start": v(207.96, 512.76) * mm, "end": v(207.96, 503.24) * mm});
            skLineSegment(sketch, "E3.0.8.21", {"start": v(209.55, 527.05) * mm, "end": v(196.85, 527.05) * mm});
            skLineSegment(sketch, "E3.3.8.21", {"start": v(198.44, 538.16) * mm, "end": v(198.44, 528.64) * mm});
            skPoint(sketch, "E3.6.8.21", {"position": v(203.2, 533.4) * mm});
            skLineSegment(sketch, "E3.7.8.21", {"start": v(207.96, 528.64) * mm, "end": v(198.44, 528.64) * mm});
            skLineSegment(sketch, "E3.10.8.21", {"start": v(209.55, 539.75) * mm, "end": v(209.55, 527.05) * mm});
            skLineSegment(sketch, "E3.13.8.21", {"start": v(209.55, 539.75) * mm, "end": v(196.85, 539.75) * mm});
            skLineSegment(sketch, "E3.16.8.21", {"start": v(196.85, 539.75) * mm, "end": v(196.85, 527.05) * mm});
            skLineSegment(sketch, "E3.19.8.21", {"start": v(207.96, 538.16) * mm, "end": v(198.44, 538.16) * mm});
            skLineSegment(sketch, "E3.22.8.21", {"start": v(207.96, 538.16) * mm, "end": v(207.96, 528.64) * mm});
            skLineSegment(sketch, "E4", {"start": v(-6.35, -6.35) * mm, "end": v(-6.35, 552.45) * mm});
            skLineSegment(sketch, "E5", {"start": v(-6.35, 552.45) * mm, "end": v(336.55, 552.45) * mm});
            skLineSegment(sketch, "E6.0.9.0", {"start": v(234.95, -6.35) * mm, "end": v(222.25, -6.35) * mm});
            skLineSegment(sketch, "E6.3.9.0", {"start": v(223.84, 4.76) * mm, "end": v(223.84, -4.76) * mm});
            skPoint(sketch, "E6.6.9.0", {"position": v(228.6, 0) * mm});
            skLineSegment(sketch, "E6.7.9.0", {"start": v(233.36, -4.76) * mm, "end": v(223.84, -4.76) * mm});
            skLineSegment(sketch, "E6.10.9.0", {"start": v(234.95, 6.35) * mm, "end": v(234.95, -6.35) * mm});
            skLineSegment(sketch, "E6.13.9.0", {"start": v(234.95, 6.35) * mm, "end": v(222.25, 6.35) * mm});
            skLineSegment(sketch, "E6.16.9.0", {"start": v(222.25, 6.35) * mm, "end": v(222.25, -6.35) * mm});
            skLineSegment(sketch, "E6.19.9.0", {"start": v(233.36, 4.76) * mm, "end": v(223.84, 4.76) * mm});
            skLineSegment(sketch, "E6.22.9.0", {"start": v(233.36, 4.76) * mm, "end": v(233.36, -4.76) * mm});
            skLineSegment(sketch, "E6.0.9.1", {"start": v(234.95, 19.05) * mm, "end": v(222.25, 19.05) * mm});
            skLineSegment(sketch, "E6.3.9.1", {"start": v(223.84, 30.16) * mm, "end": v(223.84, 20.64) * mm});
            skPoint(sketch, "E6.6.9.1", {"position": v(228.6, 25.4) * mm});
            skLineSegment(sketch, "E6.7.9.1", {"start": v(233.36, 20.64) * mm, "end": v(223.84, 20.64) * mm});
            skLineSegment(sketch, "E6.10.9.1", {"start": v(234.95, 31.75) * mm, "end": v(234.95, 19.05) * mm});
            skLineSegment(sketch, "E6.13.9.1", {"start": v(234.95, 31.75) * mm, "end": v(222.25, 31.75) * mm});
            skLineSegment(sketch, "E6.16.9.1", {"start": v(222.25, 31.75) * mm, "end": v(222.25, 19.05) * mm});
            skLineSegment(sketch, "E6.19.9.1", {"start": v(233.36, 30.16) * mm, "end": v(223.84, 30.16) * mm});
            skLineSegment(sketch, "E6.22.9.1", {"start": v(233.36, 30.16) * mm, "end": v(233.36, 20.64) * mm});
            skLineSegment(sketch, "E6.0.9.2", {"start": v(234.95, 44.45) * mm, "end": v(222.25, 44.45) * mm});
            skLineSegment(sketch, "E6.3.9.2", {"start": v(223.84, 55.56) * mm, "end": v(223.84, 46.04) * mm});
            skPoint(sketch, "E6.6.9.2", {"position": v(228.6, 50.8) * mm});
            skLineSegment(sketch, "E6.7.9.2", {"start": v(233.36, 46.04) * mm, "end": v(223.84, 46.04) * mm});
            skLineSegment(sketch, "E6.10.9.2", {"start": v(234.95, 57.15) * mm, "end": v(234.95, 44.45) * mm});
            skLineSegment(sketch, "E6.13.9.2", {"start": v(234.95, 57.15) * mm, "end": v(222.25, 57.15) * mm});
            skLineSegment(sketch, "E6.16.9.2", {"start": v(222.25, 57.15) * mm, "end": v(222.25, 44.45) * mm});
            skLineSegment(sketch, "E6.19.9.2", {"start": v(233.36, 55.56) * mm, "end": v(223.84, 55.56) * mm});
            skLineSegment(sketch, "E6.22.9.2", {"start": v(233.36, 55.56) * mm, "end": v(233.36, 46.04) * mm});
            skLineSegment(sketch, "E6.0.9.3", {"start": v(234.95, 69.85) * mm, "end": v(222.25, 69.85) * mm});
            skLineSegment(sketch, "E6.3.9.3", {"start": v(223.84, 80.96) * mm, "end": v(223.84, 71.44) * mm});
            skPoint(sketch, "E6.6.9.3", {"position": v(228.6, 76.2) * mm});
            skLineSegment(sketch, "E6.7.9.3", {"start": v(233.36, 71.44) * mm, "end": v(223.84, 71.44) * mm});
            skLineSegment(sketch, "E6.10.9.3", {"start": v(234.95, 82.55) * mm, "end": v(234.95, 69.85) * mm});
            skLineSegment(sketch, "E6.13.9.3", {"start": v(234.95, 82.55) * mm, "end": v(222.25, 82.55) * mm});
            skLineSegment(sketch, "E6.16.9.3", {"start": v(222.25, 82.55) * mm, "end": v(222.25, 69.85) * mm});
            skLineSegment(sketch, "E6.19.9.3", {"start": v(233.36, 80.96) * mm, "end": v(223.84, 80.96) * mm});
            skLineSegment(sketch, "E6.22.9.3", {"start": v(233.36, 80.96) * mm, "end": v(233.36, 71.44) * mm});
            skLineSegment(sketch, "E6.0.9.4", {"start": v(234.95, 95.25) * mm, "end": v(222.25, 95.25) * mm});
            skLineSegment(sketch, "E6.3.9.4", {"start": v(223.84, 106.36) * mm, "end": v(223.84, 96.84) * mm});
            skPoint(sketch, "E6.6.9.4", {"position": v(228.6, 101.6) * mm});
            skLineSegment(sketch, "E6.7.9.4", {"start": v(233.36, 96.84) * mm, "end": v(223.84, 96.84) * mm});
            skLineSegment(sketch, "E6.10.9.4", {"start": v(234.95, 107.95) * mm, "end": v(234.95, 95.25) * mm});
            skLineSegment(sketch, "E6.13.9.4", {"start": v(234.95, 107.95) * mm, "end": v(222.25, 107.95) * mm});
            skLineSegment(sketch, "E6.16.9.4", {"start": v(222.25, 107.95) * mm, "end": v(222.25, 95.25) * mm});
            skLineSegment(sketch, "E6.19.9.4", {"start": v(233.36, 106.36) * mm, "end": v(223.84, 106.36) * mm});
            skLineSegment(sketch, "E6.22.9.4", {"start": v(233.36, 106.36) * mm, "end": v(233.36, 96.84) * mm});
            skLineSegment(sketch, "E6.0.9.5", {"start": v(234.95, 120.65) * mm, "end": v(222.25, 120.65) * mm});
            skLineSegment(sketch, "E6.3.9.5", {"start": v(223.84, 131.76) * mm, "end": v(223.84, 122.24) * mm});
            skPoint(sketch, "E6.6.9.5", {"position": v(228.6, 127) * mm});
            skLineSegment(sketch, "E6.7.9.5", {"start": v(233.36, 122.24) * mm, "end": v(223.84, 122.24) * mm});
            skLineSegment(sketch, "E6.10.9.5", {"start": v(234.95, 133.35) * mm, "end": v(234.95, 120.65) * mm});
            skLineSegment(sketch, "E6.13.9.5", {"start": v(234.95, 133.35) * mm, "end": v(222.25, 133.35) * mm});
            skLineSegment(sketch, "E6.16.9.5", {"start": v(222.25, 133.35) * mm, "end": v(222.25, 120.65) * mm});
            skLineSegment(sketch, "E6.19.9.5", {"start": v(233.36, 131.76) * mm, "end": v(223.84, 131.76) * mm});
            skLineSegment(sketch, "E6.22.9.5", {"start": v(233.36, 131.76) * mm, "end": v(233.36, 122.24) * mm});
            skLineSegment(sketch, "E6.0.9.6", {"start": v(234.95, 146.05) * mm, "end": v(222.25, 146.05) * mm});
            skLineSegment(sketch, "E6.3.9.6", {"start": v(223.84, 157.16) * mm, "end": v(223.84, 147.64) * mm});
            skPoint(sketch, "E6.6.9.6", {"position": v(228.6, 152.4) * mm});
            skLineSegment(sketch, "E6.7.9.6", {"start": v(233.36, 147.64) * mm, "end": v(223.84, 147.64) * mm});
            skLineSegment(sketch, "E6.10.9.6", {"start": v(234.95, 158.75) * mm, "end": v(234.95, 146.05) * mm});
            skLineSegment(sketch, "E6.13.9.6", {"start": v(234.95, 158.75) * mm, "end": v(222.25, 158.75) * mm});
            skLineSegment(sketch, "E6.16.9.6", {"start": v(222.25, 158.75) * mm, "end": v(222.25, 146.05) * mm});
            skLineSegment(sketch, "E6.19.9.6", {"start": v(233.36, 157.16) * mm, "end": v(223.84, 157.16) * mm});
            skLineSegment(sketch, "E6.22.9.6", {"start": v(233.36, 157.16) * mm, "end": v(233.36, 147.64) * mm});
            skLineSegment(sketch, "E6.0.9.7", {"start": v(234.95, 171.45) * mm, "end": v(222.25, 171.45) * mm});
            skLineSegment(sketch, "E6.3.9.7", {"start": v(223.84, 182.56) * mm, "end": v(223.84, 173.04) * mm});
            skPoint(sketch, "E6.6.9.7", {"position": v(228.6, 177.8) * mm});
            skLineSegment(sketch, "E6.7.9.7", {"start": v(233.36, 173.04) * mm, "end": v(223.84, 173.04) * mm});
            skLineSegment(sketch, "E6.10.9.7", {"start": v(234.95, 184.15) * mm, "end": v(234.95, 171.45) * mm});
            skLineSegment(sketch, "E6.13.9.7", {"start": v(234.95, 184.15) * mm, "end": v(222.25, 184.15) * mm});
            skLineSegment(sketch, "E6.16.9.7", {"start": v(222.25, 184.15) * mm, "end": v(222.25, 171.45) * mm});
            skLineSegment(sketch, "E6.19.9.7", {"start": v(233.36, 182.56) * mm, "end": v(223.84, 182.56) * mm});
            skLineSegment(sketch, "E6.22.9.7", {"start": v(233.36, 182.56) * mm, "end": v(233.36, 173.04) * mm});
            skLineSegment(sketch, "E6.0.9.8", {"start": v(234.95, 196.85) * mm, "end": v(222.25, 196.85) * mm});
            skLineSegment(sketch, "E6.3.9.8", {"start": v(223.84, 207.96) * mm, "end": v(223.84, 198.44) * mm});
            skPoint(sketch, "E6.6.9.8", {"position": v(228.6, 203.2) * mm});
            skLineSegment(sketch, "E6.7.9.8", {"start": v(233.36, 198.44) * mm, "end": v(223.84, 198.44) * mm});
            skLineSegment(sketch, "E6.10.9.8", {"start": v(234.95, 209.55) * mm, "end": v(234.95, 196.85) * mm});
            skLineSegment(sketch, "E6.13.9.8", {"start": v(234.95, 209.55) * mm, "end": v(222.25, 209.55) * mm});
            skLineSegment(sketch, "E6.16.9.8", {"start": v(222.25, 209.55) * mm, "end": v(222.25, 196.85) * mm});
            skLineSegment(sketch, "E6.19.9.8", {"start": v(233.36, 207.96) * mm, "end": v(223.84, 207.96) * mm});
            skLineSegment(sketch, "E6.22.9.8", {"start": v(233.36, 207.96) * mm, "end": v(233.36, 198.44) * mm});
            skLineSegment(sketch, "E6.0.9.9", {"start": v(234.95, 222.25) * mm, "end": v(222.25, 222.25) * mm});
            skLineSegment(sketch, "E6.3.9.9", {"start": v(223.84, 233.36) * mm, "end": v(223.84, 223.84) * mm});
            skPoint(sketch, "E6.6.9.9", {"position": v(228.6, 228.6) * mm});
            skLineSegment(sketch, "E6.7.9.9", {"start": v(233.36, 223.84) * mm, "end": v(223.84, 223.84) * mm});
            skLineSegment(sketch, "E6.10.9.9", {"start": v(234.95, 234.95) * mm, "end": v(234.95, 222.25) * mm});
            skLineSegment(sketch, "E6.13.9.9", {"start": v(234.95, 234.95) * mm, "end": v(222.25, 234.95) * mm});
            skLineSegment(sketch, "E6.16.9.9", {"start": v(222.25, 234.95) * mm, "end": v(222.25, 222.25) * mm});
            skLineSegment(sketch, "E6.19.9.9", {"start": v(233.36, 233.36) * mm, "end": v(223.84, 233.36) * mm});
            skLineSegment(sketch, "E6.22.9.9", {"start": v(233.36, 233.36) * mm, "end": v(233.36, 223.84) * mm});
            skLineSegment(sketch, "E6.0.9.10", {"start": v(234.95, 247.65) * mm, "end": v(222.25, 247.65) * mm});
            skLineSegment(sketch, "E6.3.9.10", {"start": v(223.84, 258.76) * mm, "end": v(223.84, 249.24) * mm});
            skPoint(sketch, "E6.6.9.10", {"position": v(228.6, 254) * mm});
            skLineSegment(sketch, "E6.7.9.10", {"start": v(233.36, 249.24) * mm, "end": v(223.84, 249.24) * mm});
            skLineSegment(sketch, "E6.10.9.10", {"start": v(234.95, 260.35) * mm, "end": v(234.95, 247.65) * mm});
            skLineSegment(sketch, "E6.13.9.10", {"start": v(234.95, 260.35) * mm, "end": v(222.25, 260.35) * mm});
            skLineSegment(sketch, "E6.16.9.10", {"start": v(222.25, 260.35) * mm, "end": v(222.25, 247.65) * mm});
            skLineSegment(sketch, "E6.19.9.10", {"start": v(233.36, 258.76) * mm, "end": v(223.84, 258.76) * mm});
            skLineSegment(sketch, "E6.22.9.10", {"start": v(233.36, 258.76) * mm, "end": v(233.36, 249.24) * mm});
            skLineSegment(sketch, "E6.0.9.11", {"start": v(234.95, 273.05) * mm, "end": v(222.25, 273.05) * mm});
            skLineSegment(sketch, "E6.3.9.11", {"start": v(223.84, 284.16) * mm, "end": v(223.84, 274.64) * mm});
            skPoint(sketch, "E6.6.9.11", {"position": v(228.6, 279.4) * mm});
            skLineSegment(sketch, "E6.7.9.11", {"start": v(233.36, 274.64) * mm, "end": v(223.84, 274.64) * mm});
            skLineSegment(sketch, "E6.10.9.11", {"start": v(234.95, 285.75) * mm, "end": v(234.95, 273.05) * mm});
            skLineSegment(sketch, "E6.13.9.11", {"start": v(234.95, 285.75) * mm, "end": v(222.25, 285.75) * mm});
            skLineSegment(sketch, "E6.16.9.11", {"start": v(222.25, 285.75) * mm, "end": v(222.25, 273.05) * mm});
            skLineSegment(sketch, "E6.19.9.11", {"start": v(233.36, 284.16) * mm, "end": v(223.84, 284.16) * mm});
            skLineSegment(sketch, "E6.22.9.11", {"start": v(233.36, 284.16) * mm, "end": v(233.36, 274.64) * mm});
            skLineSegment(sketch, "E6.0.9.12", {"start": v(234.95, 298.45) * mm, "end": v(222.25, 298.45) * mm});
            skLineSegment(sketch, "E6.3.9.12", {"start": v(223.84, 309.56) * mm, "end": v(223.84, 300.04) * mm});
            skPoint(sketch, "E6.6.9.12", {"position": v(228.6, 304.8) * mm});
            skLineSegment(sketch, "E6.7.9.12", {"start": v(233.36, 300.04) * mm, "end": v(223.84, 300.04) * mm});
            skLineSegment(sketch, "E6.10.9.12", {"start": v(234.95, 311.15) * mm, "end": v(234.95, 298.45) * mm});
            skLineSegment(sketch, "E6.13.9.12", {"start": v(234.95, 311.15) * mm, "end": v(222.25, 311.15) * mm});
            skLineSegment(sketch, "E6.16.9.12", {"start": v(222.25, 311.15) * mm, "end": v(222.25, 298.45) * mm});
            skLineSegment(sketch, "E6.19.9.12", {"start": v(233.36, 309.56) * mm, "end": v(223.84, 309.56) * mm});
            skLineSegment(sketch, "E6.22.9.12", {"start": v(233.36, 309.56) * mm, "end": v(233.36, 300.04) * mm});
            skLineSegment(sketch, "E6.0.9.13", {"start": v(234.95, 323.85) * mm, "end": v(222.25, 323.85) * mm});
            skLineSegment(sketch, "E6.3.9.13", {"start": v(223.84, 334.96) * mm, "end": v(223.84, 325.44) * mm});
            skPoint(sketch, "E6.6.9.13", {"position": v(228.6, 330.2) * mm});
            skLineSegment(sketch, "E6.7.9.13", {"start": v(233.36, 325.44) * mm, "end": v(223.84, 325.44) * mm});
            skLineSegment(sketch, "E6.10.9.13", {"start": v(234.95, 336.55) * mm, "end": v(234.95, 323.85) * mm});
            skLineSegment(sketch, "E6.13.9.13", {"start": v(234.95, 336.55) * mm, "end": v(222.25, 336.55) * mm});
            skLineSegment(sketch, "E6.16.9.13", {"start": v(222.25, 336.55) * mm, "end": v(222.25, 323.85) * mm});
            skLineSegment(sketch, "E6.19.9.13", {"start": v(233.36, 334.96) * mm, "end": v(223.84, 334.96) * mm});
            skLineSegment(sketch, "E6.22.9.13", {"start": v(233.36, 334.96) * mm, "end": v(233.36, 325.44) * mm});
            skLineSegment(sketch, "E6.0.9.14", {"start": v(234.95, 349.25) * mm, "end": v(222.25, 349.25) * mm});
            skLineSegment(sketch, "E6.3.9.14", {"start": v(223.84, 360.36) * mm, "end": v(223.84, 350.84) * mm});
            skPoint(sketch, "E6.6.9.14", {"position": v(228.6, 355.6) * mm});
            skLineSegment(sketch, "E6.7.9.14", {"start": v(233.36, 350.84) * mm, "end": v(223.84, 350.84) * mm});
            skLineSegment(sketch, "E6.10.9.14", {"start": v(234.95, 361.95) * mm, "end": v(234.95, 349.25) * mm});
            skLineSegment(sketch, "E6.13.9.14", {"start": v(234.95, 361.95) * mm, "end": v(222.25, 361.95) * mm});
            skLineSegment(sketch, "E6.16.9.14", {"start": v(222.25, 361.95) * mm, "end": v(222.25, 349.25) * mm});
            skLineSegment(sketch, "E6.19.9.14", {"start": v(233.36, 360.36) * mm, "end": v(223.84, 360.36) * mm});
            skLineSegment(sketch, "E6.22.9.14", {"start": v(233.36, 360.36) * mm, "end": v(233.36, 350.84) * mm});
            skLineSegment(sketch, "E6.0.9.15", {"start": v(234.95, 374.65) * mm, "end": v(222.25, 374.65) * mm});
            skLineSegment(sketch, "E6.3.9.15", {"start": v(223.84, 385.76) * mm, "end": v(223.84, 376.24) * mm});
            skPoint(sketch, "E6.6.9.15", {"position": v(228.6, 381) * mm});
            skLineSegment(sketch, "E6.7.9.15", {"start": v(233.36, 376.24) * mm, "end": v(223.84, 376.24) * mm});
            skLineSegment(sketch, "E6.10.9.15", {"start": v(234.95, 387.35) * mm, "end": v(234.95, 374.65) * mm});
            skLineSegment(sketch, "E6.13.9.15", {"start": v(234.95, 387.35) * mm, "end": v(222.25, 387.35) * mm});
            skLineSegment(sketch, "E6.16.9.15", {"start": v(222.25, 387.35) * mm, "end": v(222.25, 374.65) * mm});
            skLineSegment(sketch, "E6.19.9.15", {"start": v(233.36, 385.76) * mm, "end": v(223.84, 385.76) * mm});
            skLineSegment(sketch, "E6.22.9.15", {"start": v(233.36, 385.76) * mm, "end": v(233.36, 376.24) * mm});
            skLineSegment(sketch, "E6.0.9.16", {"start": v(234.95, 400.05) * mm, "end": v(222.25, 400.05) * mm});
            skLineSegment(sketch, "E6.3.9.16", {"start": v(223.84, 411.16) * mm, "end": v(223.84, 401.64) * mm});
            skPoint(sketch, "E6.6.9.16", {"position": v(228.6, 406.4) * mm});
            skLineSegment(sketch, "E6.7.9.16", {"start": v(233.36, 401.64) * mm, "end": v(223.84, 401.64) * mm});
            skLineSegment(sketch, "E6.10.9.16", {"start": v(234.95, 412.75) * mm, "end": v(234.95, 400.05) * mm});
            skLineSegment(sketch, "E6.13.9.16", {"start": v(234.95, 412.75) * mm, "end": v(222.25, 412.75) * mm});
            skLineSegment(sketch, "E6.16.9.16", {"start": v(222.25, 412.75) * mm, "end": v(222.25, 400.05) * mm});
            skLineSegment(sketch, "E6.19.9.16", {"start": v(233.36, 411.16) * mm, "end": v(223.84, 411.16) * mm});
            skLineSegment(sketch, "E6.22.9.16", {"start": v(233.36, 411.16) * mm, "end": v(233.36, 401.64) * mm});
            skLineSegment(sketch, "E6.0.9.17", {"start": v(234.95, 425.45) * mm, "end": v(222.25, 425.45) * mm});
            skLineSegment(sketch, "E6.3.9.17", {"start": v(223.84, 436.56) * mm, "end": v(223.84, 427.04) * mm});
            skPoint(sketch, "E6.6.9.17", {"position": v(228.6, 431.8) * mm});
            skLineSegment(sketch, "E6.7.9.17", {"start": v(233.36, 427.04) * mm, "end": v(223.84, 427.04) * mm});
            skLineSegment(sketch, "E6.10.9.17", {"start": v(234.95, 438.15) * mm, "end": v(234.95, 425.45) * mm});
            skLineSegment(sketch, "E6.13.9.17", {"start": v(234.95, 438.15) * mm, "end": v(222.25, 438.15) * mm});
            skLineSegment(sketch, "E6.16.9.17", {"start": v(222.25, 438.15) * mm, "end": v(222.25, 425.45) * mm});
            skLineSegment(sketch, "E6.19.9.17", {"start": v(233.36, 436.56) * mm, "end": v(223.84, 436.56) * mm});
            skLineSegment(sketch, "E6.22.9.17", {"start": v(233.36, 436.56) * mm, "end": v(233.36, 427.04) * mm});
            skLineSegment(sketch, "E6.0.9.18", {"start": v(234.95, 450.85) * mm, "end": v(222.25, 450.85) * mm});
            skLineSegment(sketch, "E6.3.9.18", {"start": v(223.84, 461.96) * mm, "end": v(223.84, 452.44) * mm});
            skPoint(sketch, "E6.6.9.18", {"position": v(228.6, 457.2) * mm});
            skLineSegment(sketch, "E6.7.9.18", {"start": v(233.36, 452.44) * mm, "end": v(223.84, 452.44) * mm});
            skLineSegment(sketch, "E6.10.9.18", {"start": v(234.95, 463.55) * mm, "end": v(234.95, 450.85) * mm});
            skLineSegment(sketch, "E6.13.9.18", {"start": v(234.95, 463.55) * mm, "end": v(222.25, 463.55) * mm});
            skLineSegment(sketch, "E6.16.9.18", {"start": v(222.25, 463.55) * mm, "end": v(222.25, 450.85) * mm});
            skLineSegment(sketch, "E6.19.9.18", {"start": v(233.36, 461.96) * mm, "end": v(223.84, 461.96) * mm});
            skLineSegment(sketch, "E6.22.9.18", {"start": v(233.36, 461.96) * mm, "end": v(233.36, 452.44) * mm});
            skLineSegment(sketch, "E6.0.9.19", {"start": v(234.95, 476.25) * mm, "end": v(222.25, 476.25) * mm});
            skLineSegment(sketch, "E6.3.9.19", {"start": v(223.84, 487.36) * mm, "end": v(223.84, 477.84) * mm});
            skPoint(sketch, "E6.6.9.19", {"position": v(228.6, 482.6) * mm});
            skLineSegment(sketch, "E6.7.9.19", {"start": v(233.36, 477.84) * mm, "end": v(223.84, 477.84) * mm});
            skLineSegment(sketch, "E6.10.9.19", {"start": v(234.95, 488.95) * mm, "end": v(234.95, 476.25) * mm});
            skLineSegment(sketch, "E6.13.9.19", {"start": v(234.95, 488.95) * mm, "end": v(222.25, 488.95) * mm});
            skLineSegment(sketch, "E6.16.9.19", {"start": v(222.25, 488.95) * mm, "end": v(222.25, 476.25) * mm});
            skLineSegment(sketch, "E6.19.9.19", {"start": v(233.36, 487.36) * mm, "end": v(223.84, 487.36) * mm});
            skLineSegment(sketch, "E6.22.9.19", {"start": v(233.36, 487.36) * mm, "end": v(233.36, 477.84) * mm});
            skLineSegment(sketch, "E6.0.9.20", {"start": v(234.95, 501.65) * mm, "end": v(222.25, 501.65) * mm});
            skLineSegment(sketch, "E6.3.9.20", {"start": v(223.84, 512.76) * mm, "end": v(223.84, 503.24) * mm});
            skPoint(sketch, "E6.6.9.20", {"position": v(228.6, 508) * mm});
            skLineSegment(sketch, "E6.7.9.20", {"start": v(233.36, 503.24) * mm, "end": v(223.84, 503.24) * mm});
            skLineSegment(sketch, "E6.10.9.20", {"start": v(234.95, 514.35) * mm, "end": v(234.95, 501.65) * mm});
            skLineSegment(sketch, "E6.13.9.20", {"start": v(234.95, 514.35) * mm, "end": v(222.25, 514.35) * mm});
            skLineSegment(sketch, "E6.16.9.20", {"start": v(222.25, 514.35) * mm, "end": v(222.25, 501.65) * mm});
            skLineSegment(sketch, "E6.19.9.20", {"start": v(233.36, 512.76) * mm, "end": v(223.84, 512.76) * mm});
            skLineSegment(sketch, "E6.22.9.20", {"start": v(233.36, 512.76) * mm, "end": v(233.36, 503.24) * mm});
            skLineSegment(sketch, "E6.0.9.21", {"start": v(234.95, 527.05) * mm, "end": v(222.25, 527.05) * mm});
            skLineSegment(sketch, "E6.3.9.21", {"start": v(223.84, 538.16) * mm, "end": v(223.84, 528.64) * mm});
            skPoint(sketch, "E6.6.9.21", {"position": v(228.6, 533.4) * mm});
            skLineSegment(sketch, "E6.7.9.21", {"start": v(233.36, 528.64) * mm, "end": v(223.84, 528.64) * mm});
            skLineSegment(sketch, "E6.10.9.21", {"start": v(234.95, 539.75) * mm, "end": v(234.95, 527.05) * mm});
            skLineSegment(sketch, "E6.13.9.21", {"start": v(234.95, 539.75) * mm, "end": v(222.25, 539.75) * mm});
            skLineSegment(sketch, "E6.16.9.21", {"start": v(222.25, 539.75) * mm, "end": v(222.25, 527.05) * mm});
            skLineSegment(sketch, "E6.19.9.21", {"start": v(233.36, 538.16) * mm, "end": v(223.84, 538.16) * mm});
            skLineSegment(sketch, "E6.22.9.21", {"start": v(233.36, 538.16) * mm, "end": v(233.36, 528.64) * mm});
            skLineSegment(sketch, "E6.0.10.0", {"start": v(260.35, -6.35) * mm, "end": v(247.65, -6.35) * mm});
            skLineSegment(sketch, "E6.3.10.0", {"start": v(249.24, 4.76) * mm, "end": v(249.24, -4.76) * mm});
            skPoint(sketch, "E6.6.10.0", {"position": v(254, 0) * mm});
            skLineSegment(sketch, "E6.7.10.0", {"start": v(258.76, -4.76) * mm, "end": v(249.24, -4.76) * mm});
            skLineSegment(sketch, "E6.10.10.0", {"start": v(260.35, 6.35) * mm, "end": v(260.35, -6.35) * mm});
            skLineSegment(sketch, "E6.13.10.0", {"start": v(260.35, 6.35) * mm, "end": v(247.65, 6.35) * mm});
            skLineSegment(sketch, "E6.16.10.0", {"start": v(247.65, 6.35) * mm, "end": v(247.65, -6.35) * mm});
            skLineSegment(sketch, "E6.19.10.0", {"start": v(258.76, 4.76) * mm, "end": v(249.24, 4.76) * mm});
            skLineSegment(sketch, "E6.22.10.0", {"start": v(258.76, 4.76) * mm, "end": v(258.76, -4.76) * mm});
            skLineSegment(sketch, "E6.0.10.1", {"start": v(260.35, 19.05) * mm, "end": v(247.65, 19.05) * mm});
            skLineSegment(sketch, "E6.3.10.1", {"start": v(249.24, 30.16) * mm, "end": v(249.24, 20.64) * mm});
            skPoint(sketch, "E6.6.10.1", {"position": v(254, 25.4) * mm});
            skLineSegment(sketch, "E6.7.10.1", {"start": v(258.76, 20.64) * mm, "end": v(249.24, 20.64) * mm});
            skLineSegment(sketch, "E6.10.10.1", {"start": v(260.35, 31.75) * mm, "end": v(260.35, 19.05) * mm});
            skLineSegment(sketch, "E6.13.10.1", {"start": v(260.35, 31.75) * mm, "end": v(247.65, 31.75) * mm});
            skLineSegment(sketch, "E6.16.10.1", {"start": v(247.65, 31.75) * mm, "end": v(247.65, 19.05) * mm});
            skLineSegment(sketch, "E6.19.10.1", {"start": v(258.76, 30.16) * mm, "end": v(249.24, 30.16) * mm});
            skLineSegment(sketch, "E6.22.10.1", {"start": v(258.76, 30.16) * mm, "end": v(258.76, 20.64) * mm});
            skLineSegment(sketch, "E6.0.10.2", {"start": v(260.35, 44.45) * mm, "end": v(247.65, 44.45) * mm});
            skLineSegment(sketch, "E6.3.10.2", {"start": v(249.24, 55.56) * mm, "end": v(249.24, 46.04) * mm});
            skPoint(sketch, "E6.6.10.2", {"position": v(254, 50.8) * mm});
            skLineSegment(sketch, "E6.7.10.2", {"start": v(258.76, 46.04) * mm, "end": v(249.24, 46.04) * mm});
            skLineSegment(sketch, "E6.10.10.2", {"start": v(260.35, 57.15) * mm, "end": v(260.35, 44.45) * mm});
            skLineSegment(sketch, "E6.13.10.2", {"start": v(260.35, 57.15) * mm, "end": v(247.65, 57.15) * mm});
            skLineSegment(sketch, "E6.16.10.2", {"start": v(247.65, 57.15) * mm, "end": v(247.65, 44.45) * mm});
            skLineSegment(sketch, "E6.19.10.2", {"start": v(258.76, 55.56) * mm, "end": v(249.24, 55.56) * mm});
            skLineSegment(sketch, "E6.22.10.2", {"start": v(258.76, 55.56) * mm, "end": v(258.76, 46.04) * mm});
            skLineSegment(sketch, "E6.0.10.3", {"start": v(260.35, 69.85) * mm, "end": v(247.65, 69.85) * mm});
            skLineSegment(sketch, "E6.3.10.3", {"start": v(249.24, 80.96) * mm, "end": v(249.24, 71.44) * mm});
            skPoint(sketch, "E6.6.10.3", {"position": v(254, 76.2) * mm});
            skLineSegment(sketch, "E6.7.10.3", {"start": v(258.76, 71.44) * mm, "end": v(249.24, 71.44) * mm});
            skLineSegment(sketch, "E6.10.10.3", {"start": v(260.35, 82.55) * mm, "end": v(260.35, 69.85) * mm});
            skLineSegment(sketch, "E6.13.10.3", {"start": v(260.35, 82.55) * mm, "end": v(247.65, 82.55) * mm});
            skLineSegment(sketch, "E6.16.10.3", {"start": v(247.65, 82.55) * mm, "end": v(247.65, 69.85) * mm});
            skLineSegment(sketch, "E6.19.10.3", {"start": v(258.76, 80.96) * mm, "end": v(249.24, 80.96) * mm});
            skLineSegment(sketch, "E6.22.10.3", {"start": v(258.76, 80.96) * mm, "end": v(258.76, 71.44) * mm});
            skLineSegment(sketch, "E6.0.10.4", {"start": v(260.35, 95.25) * mm, "end": v(247.65, 95.25) * mm});
            skLineSegment(sketch, "E6.3.10.4", {"start": v(249.24, 106.36) * mm, "end": v(249.24, 96.84) * mm});
            skPoint(sketch, "E6.6.10.4", {"position": v(254, 101.6) * mm});
            skLineSegment(sketch, "E6.7.10.4", {"start": v(258.76, 96.84) * mm, "end": v(249.24, 96.84) * mm});
            skLineSegment(sketch, "E6.10.10.4", {"start": v(260.35, 107.95) * mm, "end": v(260.35, 95.25) * mm});
            skLineSegment(sketch, "E6.13.10.4", {"start": v(260.35, 107.95) * mm, "end": v(247.65, 107.95) * mm});
            skLineSegment(sketch, "E6.16.10.4", {"start": v(247.65, 107.95) * mm, "end": v(247.65, 95.25) * mm});
            skLineSegment(sketch, "E6.19.10.4", {"start": v(258.76, 106.36) * mm, "end": v(249.24, 106.36) * mm});
            skLineSegment(sketch, "E6.22.10.4", {"start": v(258.76, 106.36) * mm, "end": v(258.76, 96.84) * mm});
            skLineSegment(sketch, "E6.0.10.5", {"start": v(260.35, 120.65) * mm, "end": v(247.65, 120.65) * mm});
            skLineSegment(sketch, "E6.3.10.5", {"start": v(249.24, 131.76) * mm, "end": v(249.24, 122.24) * mm});
            skPoint(sketch, "E6.6.10.5", {"position": v(254, 127) * mm});
            skLineSegment(sketch, "E6.7.10.5", {"start": v(258.76, 122.24) * mm, "end": v(249.24, 122.24) * mm});
            skLineSegment(sketch, "E6.10.10.5", {"start": v(260.35, 133.35) * mm, "end": v(260.35, 120.65) * mm});
            skLineSegment(sketch, "E6.13.10.5", {"start": v(260.35, 133.35) * mm, "end": v(247.65, 133.35) * mm});
            skLineSegment(sketch, "E6.16.10.5", {"start": v(247.65, 133.35) * mm, "end": v(247.65, 120.65) * mm});
            skLineSegment(sketch, "E6.19.10.5", {"start": v(258.76, 131.76) * mm, "end": v(249.24, 131.76) * mm});
            skLineSegment(sketch, "E6.22.10.5", {"start": v(258.76, 131.76) * mm, "end": v(258.76, 122.24) * mm});
            skLineSegment(sketch, "E6.0.10.6", {"start": v(260.35, 146.05) * mm, "end": v(247.65, 146.05) * mm});
            skLineSegment(sketch, "E6.3.10.6", {"start": v(249.24, 157.16) * mm, "end": v(249.24, 147.64) * mm});
            skPoint(sketch, "E6.6.10.6", {"position": v(254, 152.4) * mm});
            skLineSegment(sketch, "E6.7.10.6", {"start": v(258.76, 147.64) * mm, "end": v(249.24, 147.64) * mm});
            skLineSegment(sketch, "E6.10.10.6", {"start": v(260.35, 158.75) * mm, "end": v(260.35, 146.05) * mm});
            skLineSegment(sketch, "E6.13.10.6", {"start": v(260.35, 158.75) * mm, "end": v(247.65, 158.75) * mm});
            skLineSegment(sketch, "E6.16.10.6", {"start": v(247.65, 158.75) * mm, "end": v(247.65, 146.05) * mm});
            skLineSegment(sketch, "E6.19.10.6", {"start": v(258.76, 157.16) * mm, "end": v(249.24, 157.16) * mm});
            skLineSegment(sketch, "E6.22.10.6", {"start": v(258.76, 157.16) * mm, "end": v(258.76, 147.64) * mm});
            skLineSegment(sketch, "E6.0.10.7", {"start": v(260.35, 171.45) * mm, "end": v(247.65, 171.45) * mm});
            skLineSegment(sketch, "E6.3.10.7", {"start": v(249.24, 182.56) * mm, "end": v(249.24, 173.04) * mm});
            skPoint(sketch, "E6.6.10.7", {"position": v(254, 177.8) * mm});
            skLineSegment(sketch, "E6.7.10.7", {"start": v(258.76, 173.04) * mm, "end": v(249.24, 173.04) * mm});
            skLineSegment(sketch, "E6.10.10.7", {"start": v(260.35, 184.15) * mm, "end": v(260.35, 171.45) * mm});
            skLineSegment(sketch, "E6.13.10.7", {"start": v(260.35, 184.15) * mm, "end": v(247.65, 184.15) * mm});
            skLineSegment(sketch, "E6.16.10.7", {"start": v(247.65, 184.15) * mm, "end": v(247.65, 171.45) * mm});
            skLineSegment(sketch, "E6.19.10.7", {"start": v(258.76, 182.56) * mm, "end": v(249.24, 182.56) * mm});
            skLineSegment(sketch, "E6.22.10.7", {"start": v(258.76, 182.56) * mm, "end": v(258.76, 173.04) * mm});
            skLineSegment(sketch, "E6.0.10.8", {"start": v(260.35, 196.85) * mm, "end": v(247.65, 196.85) * mm});
            skLineSegment(sketch, "E6.3.10.8", {"start": v(249.24, 207.96) * mm, "end": v(249.24, 198.44) * mm});
            skPoint(sketch, "E6.6.10.8", {"position": v(254, 203.2) * mm});
            skLineSegment(sketch, "E6.7.10.8", {"start": v(258.76, 198.44) * mm, "end": v(249.24, 198.44) * mm});
            skLineSegment(sketch, "E6.10.10.8", {"start": v(260.35, 209.55) * mm, "end": v(260.35, 196.85) * mm});
            skLineSegment(sketch, "E6.13.10.8", {"start": v(260.35, 209.55) * mm, "end": v(247.65, 209.55) * mm});
            skLineSegment(sketch, "E6.16.10.8", {"start": v(247.65, 209.55) * mm, "end": v(247.65, 196.85) * mm});
            skLineSegment(sketch, "E6.19.10.8", {"start": v(258.76, 207.96) * mm, "end": v(249.24, 207.96) * mm});
            skLineSegment(sketch, "E6.22.10.8", {"start": v(258.76, 207.96) * mm, "end": v(258.76, 198.44) * mm});
            skLineSegment(sketch, "E6.0.10.9", {"start": v(260.35, 222.25) * mm, "end": v(247.65, 222.25) * mm});
            skLineSegment(sketch, "E6.3.10.9", {"start": v(249.24, 233.36) * mm, "end": v(249.24, 223.84) * mm});
            skPoint(sketch, "E6.6.10.9", {"position": v(254, 228.6) * mm});
            skLineSegment(sketch, "E6.7.10.9", {"start": v(258.76, 223.84) * mm, "end": v(249.24, 223.84) * mm});
            skLineSegment(sketch, "E6.10.10.9", {"start": v(260.35, 234.95) * mm, "end": v(260.35, 222.25) * mm});
            skLineSegment(sketch, "E6.13.10.9", {"start": v(260.35, 234.95) * mm, "end": v(247.65, 234.95) * mm});
            skLineSegment(sketch, "E6.16.10.9", {"start": v(247.65, 234.95) * mm, "end": v(247.65, 222.25) * mm});
            skLineSegment(sketch, "E6.19.10.9", {"start": v(258.76, 233.36) * mm, "end": v(249.24, 233.36) * mm});
            skLineSegment(sketch, "E6.22.10.9", {"start": v(258.76, 233.36) * mm, "end": v(258.76, 223.84) * mm});
            skLineSegment(sketch, "E6.0.10.10", {"start": v(260.35, 247.65) * mm, "end": v(247.65, 247.65) * mm});
            skLineSegment(sketch, "E6.3.10.10", {"start": v(249.24, 258.76) * mm, "end": v(249.24, 249.24) * mm});
            skPoint(sketch, "E6.6.10.10", {"position": v(254, 254) * mm});
            skLineSegment(sketch, "E6.7.10.10", {"start": v(258.76, 249.24) * mm, "end": v(249.24, 249.24) * mm});
            skLineSegment(sketch, "E6.10.10.10", {"start": v(260.35, 260.35) * mm, "end": v(260.35, 247.65) * mm});
            skLineSegment(sketch, "E6.13.10.10", {"start": v(260.35, 260.35) * mm, "end": v(247.65, 260.35) * mm});
            skLineSegment(sketch, "E6.16.10.10", {"start": v(247.65, 260.35) * mm, "end": v(247.65, 247.65) * mm});
            skLineSegment(sketch, "E6.19.10.10", {"start": v(258.76, 258.76) * mm, "end": v(249.24, 258.76) * mm});
            skLineSegment(sketch, "E6.22.10.10", {"start": v(258.76, 258.76) * mm, "end": v(258.76, 249.24) * mm});
            skLineSegment(sketch, "E6.0.10.11", {"start": v(260.35, 273.05) * mm, "end": v(247.65, 273.05) * mm});
            skLineSegment(sketch, "E6.3.10.11", {"start": v(249.24, 284.16) * mm, "end": v(249.24, 274.64) * mm});
            skPoint(sketch, "E6.6.10.11", {"position": v(254, 279.4) * mm});
            skLineSegment(sketch, "E6.7.10.11", {"start": v(258.76, 274.64) * mm, "end": v(249.24, 274.64) * mm});
            skLineSegment(sketch, "E6.10.10.11", {"start": v(260.35, 285.75) * mm, "end": v(260.35, 273.05) * mm});
            skLineSegment(sketch, "E6.13.10.11", {"start": v(260.35, 285.75) * mm, "end": v(247.65, 285.75) * mm});
            skLineSegment(sketch, "E6.16.10.11", {"start": v(247.65, 285.75) * mm, "end": v(247.65, 273.05) * mm});
            skLineSegment(sketch, "E6.19.10.11", {"start": v(258.76, 284.16) * mm, "end": v(249.24, 284.16) * mm});
            skLineSegment(sketch, "E6.22.10.11", {"start": v(258.76, 284.16) * mm, "end": v(258.76, 274.64) * mm});
            skLineSegment(sketch, "E6.0.10.12", {"start": v(260.35, 298.45) * mm, "end": v(247.65, 298.45) * mm});
            skLineSegment(sketch, "E6.3.10.12", {"start": v(249.24, 309.56) * mm, "end": v(249.24, 300.04) * mm});
            skPoint(sketch, "E6.6.10.12", {"position": v(254, 304.8) * mm});
            skLineSegment(sketch, "E6.7.10.12", {"start": v(258.76, 300.04) * mm, "end": v(249.24, 300.04) * mm});
            skLineSegment(sketch, "E6.10.10.12", {"start": v(260.35, 311.15) * mm, "end": v(260.35, 298.45) * mm});
            skLineSegment(sketch, "E6.13.10.12", {"start": v(260.35, 311.15) * mm, "end": v(247.65, 311.15) * mm});
            skLineSegment(sketch, "E6.16.10.12", {"start": v(247.65, 311.15) * mm, "end": v(247.65, 298.45) * mm});
            skLineSegment(sketch, "E6.19.10.12", {"start": v(258.76, 309.56) * mm, "end": v(249.24, 309.56) * mm});
            skLineSegment(sketch, "E6.22.10.12", {"start": v(258.76, 309.56) * mm, "end": v(258.76, 300.04) * mm});
            skLineSegment(sketch, "E6.0.10.13", {"start": v(260.35, 323.85) * mm, "end": v(247.65, 323.85) * mm});
            skLineSegment(sketch, "E6.3.10.13", {"start": v(249.24, 334.96) * mm, "end": v(249.24, 325.44) * mm});
            skPoint(sketch, "E6.6.10.13", {"position": v(254, 330.2) * mm});
            skLineSegment(sketch, "E6.7.10.13", {"start": v(258.76, 325.44) * mm, "end": v(249.24, 325.44) * mm});
            skLineSegment(sketch, "E6.10.10.13", {"start": v(260.35, 336.55) * mm, "end": v(260.35, 323.85) * mm});
            skLineSegment(sketch, "E6.13.10.13", {"start": v(260.35, 336.55) * mm, "end": v(247.65, 336.55) * mm});
            skLineSegment(sketch, "E6.16.10.13", {"start": v(247.65, 336.55) * mm, "end": v(247.65, 323.85) * mm});
            skLineSegment(sketch, "E6.19.10.13", {"start": v(258.76, 334.96) * mm, "end": v(249.24, 334.96) * mm});
            skLineSegment(sketch, "E6.22.10.13", {"start": v(258.76, 334.96) * mm, "end": v(258.76, 325.44) * mm});
            skLineSegment(sketch, "E6.0.10.14", {"start": v(260.35, 349.25) * mm, "end": v(247.65, 349.25) * mm});
            skLineSegment(sketch, "E6.3.10.14", {"start": v(249.24, 360.36) * mm, "end": v(249.24, 350.84) * mm});
            skPoint(sketch, "E6.6.10.14", {"position": v(254, 355.6) * mm});
            skLineSegment(sketch, "E6.7.10.14", {"start": v(258.76, 350.84) * mm, "end": v(249.24, 350.84) * mm});
            skLineSegment(sketch, "E6.10.10.14", {"start": v(260.35, 361.95) * mm, "end": v(260.35, 349.25) * mm});
            skLineSegment(sketch, "E6.13.10.14", {"start": v(260.35, 361.95) * mm, "end": v(247.65, 361.95) * mm});
            skLineSegment(sketch, "E6.16.10.14", {"start": v(247.65, 361.95) * mm, "end": v(247.65, 349.25) * mm});
            skLineSegment(sketch, "E6.19.10.14", {"start": v(258.76, 360.36) * mm, "end": v(249.24, 360.36) * mm});
            skLineSegment(sketch, "E6.22.10.14", {"start": v(258.76, 360.36) * mm, "end": v(258.76, 350.84) * mm});
            skLineSegment(sketch, "E6.0.10.15", {"start": v(260.35, 374.65) * mm, "end": v(247.65, 374.65) * mm});
            skLineSegment(sketch, "E6.3.10.15", {"start": v(249.24, 385.76) * mm, "end": v(249.24, 376.24) * mm});
            skPoint(sketch, "E6.6.10.15", {"position": v(254, 381) * mm});
            skLineSegment(sketch, "E6.7.10.15", {"start": v(258.76, 376.24) * mm, "end": v(249.24, 376.24) * mm});
            skLineSegment(sketch, "E6.10.10.15", {"start": v(260.35, 387.35) * mm, "end": v(260.35, 374.65) * mm});
            skLineSegment(sketch, "E6.13.10.15", {"start": v(260.35, 387.35) * mm, "end": v(247.65, 387.35) * mm});
            skLineSegment(sketch, "E6.16.10.15", {"start": v(247.65, 387.35) * mm, "end": v(247.65, 374.65) * mm});
            skLineSegment(sketch, "E6.19.10.15", {"start": v(258.76, 385.76) * mm, "end": v(249.24, 385.76) * mm});
            skLineSegment(sketch, "E6.22.10.15", {"start": v(258.76, 385.76) * mm, "end": v(258.76, 376.24) * mm});
            skLineSegment(sketch, "E6.0.10.16", {"start": v(260.35, 400.05) * mm, "end": v(247.65, 400.05) * mm});
            skLineSegment(sketch, "E6.3.10.16", {"start": v(249.24, 411.16) * mm, "end": v(249.24, 401.64) * mm});
            skPoint(sketch, "E6.6.10.16", {"position": v(254, 406.4) * mm});
            skLineSegment(sketch, "E6.7.10.16", {"start": v(258.76, 401.64) * mm, "end": v(249.24, 401.64) * mm});
            skLineSegment(sketch, "E6.10.10.16", {"start": v(260.35, 412.75) * mm, "end": v(260.35, 400.05) * mm});
            skLineSegment(sketch, "E6.13.10.16", {"start": v(260.35, 412.75) * mm, "end": v(247.65, 412.75) * mm});
            skLineSegment(sketch, "E6.16.10.16", {"start": v(247.65, 412.75) * mm, "end": v(247.65, 400.05) * mm});
            skLineSegment(sketch, "E6.19.10.16", {"start": v(258.76, 411.16) * mm, "end": v(249.24, 411.16) * mm});
            skLineSegment(sketch, "E6.22.10.16", {"start": v(258.76, 411.16) * mm, "end": v(258.76, 401.64) * mm});
            skLineSegment(sketch, "E6.0.10.17", {"start": v(260.35, 425.45) * mm, "end": v(247.65, 425.45) * mm});
            skLineSegment(sketch, "E6.3.10.17", {"start": v(249.24, 436.56) * mm, "end": v(249.24, 427.04) * mm});
            skPoint(sketch, "E6.6.10.17", {"position": v(254, 431.8) * mm});
            skLineSegment(sketch, "E6.7.10.17", {"start": v(258.76, 427.04) * mm, "end": v(249.24, 427.04) * mm});
            skLineSegment(sketch, "E6.10.10.17", {"start": v(260.35, 438.15) * mm, "end": v(260.35, 425.45) * mm});
            skLineSegment(sketch, "E6.13.10.17", {"start": v(260.35, 438.15) * mm, "end": v(247.65, 438.15) * mm});
            skLineSegment(sketch, "E6.16.10.17", {"start": v(247.65, 438.15) * mm, "end": v(247.65, 425.45) * mm});
            skLineSegment(sketch, "E6.19.10.17", {"start": v(258.76, 436.56) * mm, "end": v(249.24, 436.56) * mm});
            skLineSegment(sketch, "E6.22.10.17", {"start": v(258.76, 436.56) * mm, "end": v(258.76, 427.04) * mm});
            skLineSegment(sketch, "E6.0.10.18", {"start": v(260.35, 450.85) * mm, "end": v(247.65, 450.85) * mm});
            skLineSegment(sketch, "E6.3.10.18", {"start": v(249.24, 461.96) * mm, "end": v(249.24, 452.44) * mm});
            skPoint(sketch, "E6.6.10.18", {"position": v(254, 457.2) * mm});
            skLineSegment(sketch, "E6.7.10.18", {"start": v(258.76, 452.44) * mm, "end": v(249.24, 452.44) * mm});
            skLineSegment(sketch, "E6.10.10.18", {"start": v(260.35, 463.55) * mm, "end": v(260.35, 450.85) * mm});
            skLineSegment(sketch, "E6.13.10.18", {"start": v(260.35, 463.55) * mm, "end": v(247.65, 463.55) * mm});
            skLineSegment(sketch, "E6.16.10.18", {"start": v(247.65, 463.55) * mm, "end": v(247.65, 450.85) * mm});
            skLineSegment(sketch, "E6.19.10.18", {"start": v(258.76, 461.96) * mm, "end": v(249.24, 461.96) * mm});
            skLineSegment(sketch, "E6.22.10.18", {"start": v(258.76, 461.96) * mm, "end": v(258.76, 452.44) * mm});
            skLineSegment(sketch, "E6.0.10.19", {"start": v(260.35, 476.25) * mm, "end": v(247.65, 476.25) * mm});
            skLineSegment(sketch, "E6.3.10.19", {"start": v(249.24, 487.36) * mm, "end": v(249.24, 477.84) * mm});
            skPoint(sketch, "E6.6.10.19", {"position": v(254, 482.6) * mm});
            skLineSegment(sketch, "E6.7.10.19", {"start": v(258.76, 477.84) * mm, "end": v(249.24, 477.84) * mm});
            skLineSegment(sketch, "E6.10.10.19", {"start": v(260.35, 488.95) * mm, "end": v(260.35, 476.25) * mm});
            skLineSegment(sketch, "E6.13.10.19", {"start": v(260.35, 488.95) * mm, "end": v(247.65, 488.95) * mm});
            skLineSegment(sketch, "E6.16.10.19", {"start": v(247.65, 488.95) * mm, "end": v(247.65, 476.25) * mm});
            skLineSegment(sketch, "E6.19.10.19", {"start": v(258.76, 487.36) * mm, "end": v(249.24, 487.36) * mm});
            skLineSegment(sketch, "E6.22.10.19", {"start": v(258.76, 487.36) * mm, "end": v(258.76, 477.84) * mm});
            skLineSegment(sketch, "E6.0.10.20", {"start": v(260.35, 501.65) * mm, "end": v(247.65, 501.65) * mm});
            skLineSegment(sketch, "E6.3.10.20", {"start": v(249.24, 512.76) * mm, "end": v(249.24, 503.24) * mm});
            skPoint(sketch, "E6.6.10.20", {"position": v(254, 508) * mm});
            skLineSegment(sketch, "E6.7.10.20", {"start": v(258.76, 503.24) * mm, "end": v(249.24, 503.24) * mm});
            skLineSegment(sketch, "E6.10.10.20", {"start": v(260.35, 514.35) * mm, "end": v(260.35, 501.65) * mm});
            skLineSegment(sketch, "E6.13.10.20", {"start": v(260.35, 514.35) * mm, "end": v(247.65, 514.35) * mm});
            skLineSegment(sketch, "E6.16.10.20", {"start": v(247.65, 514.35) * mm, "end": v(247.65, 501.65) * mm});
            skLineSegment(sketch, "E6.19.10.20", {"start": v(258.76, 512.76) * mm, "end": v(249.24, 512.76) * mm});
            skLineSegment(sketch, "E6.22.10.20", {"start": v(258.76, 512.76) * mm, "end": v(258.76, 503.24) * mm});
            skLineSegment(sketch, "E6.0.10.21", {"start": v(260.35, 527.05) * mm, "end": v(247.65, 527.05) * mm});
            skLineSegment(sketch, "E6.3.10.21", {"start": v(249.24, 538.16) * mm, "end": v(249.24, 528.64) * mm});
            skPoint(sketch, "E6.6.10.21", {"position": v(254, 533.4) * mm});
            skLineSegment(sketch, "E6.7.10.21", {"start": v(258.76, 528.64) * mm, "end": v(249.24, 528.64) * mm});
            skLineSegment(sketch, "E6.10.10.21", {"start": v(260.35, 539.75) * mm, "end": v(260.35, 527.05) * mm});
            skLineSegment(sketch, "E6.13.10.21", {"start": v(260.35, 539.75) * mm, "end": v(247.65, 539.75) * mm});
            skLineSegment(sketch, "E6.16.10.21", {"start": v(247.65, 539.75) * mm, "end": v(247.65, 527.05) * mm});
            skLineSegment(sketch, "E6.19.10.21", {"start": v(258.76, 538.16) * mm, "end": v(249.24, 538.16) * mm});
            skLineSegment(sketch, "E6.22.10.21", {"start": v(258.76, 538.16) * mm, "end": v(258.76, 528.64) * mm});
            skLineSegment(sketch, "E6.0.11.0", {"start": v(285.75, -6.35) * mm, "end": v(273.05, -6.35) * mm});
            skLineSegment(sketch, "E6.3.11.0", {"start": v(274.64, 4.76) * mm, "end": v(274.64, -4.76) * mm});
            skPoint(sketch, "E6.6.11.0", {"position": v(279.4, 0) * mm});
            skLineSegment(sketch, "E6.7.11.0", {"start": v(284.16, -4.76) * mm, "end": v(274.64, -4.76) * mm});
            skLineSegment(sketch, "E6.10.11.0", {"start": v(285.75, 6.35) * mm, "end": v(285.75, -6.35) * mm});
            skLineSegment(sketch, "E6.13.11.0", {"start": v(285.75, 6.35) * mm, "end": v(273.05, 6.35) * mm});
            skLineSegment(sketch, "E6.16.11.0", {"start": v(273.05, 6.35) * mm, "end": v(273.05, -6.35) * mm});
            skLineSegment(sketch, "E6.19.11.0", {"start": v(284.16, 4.76) * mm, "end": v(274.64, 4.76) * mm});
            skLineSegment(sketch, "E6.22.11.0", {"start": v(284.16, 4.76) * mm, "end": v(284.16, -4.76) * mm});
            skLineSegment(sketch, "E6.0.11.1", {"start": v(285.75, 19.05) * mm, "end": v(273.05, 19.05) * mm});
            skLineSegment(sketch, "E6.3.11.1", {"start": v(274.64, 30.16) * mm, "end": v(274.64, 20.64) * mm});
            skPoint(sketch, "E6.6.11.1", {"position": v(279.4, 25.4) * mm});
            skLineSegment(sketch, "E6.7.11.1", {"start": v(284.16, 20.64) * mm, "end": v(274.64, 20.64) * mm});
            skLineSegment(sketch, "E6.10.11.1", {"start": v(285.75, 31.75) * mm, "end": v(285.75, 19.05) * mm});
            skLineSegment(sketch, "E6.13.11.1", {"start": v(285.75, 31.75) * mm, "end": v(273.05, 31.75) * mm});
            skLineSegment(sketch, "E6.16.11.1", {"start": v(273.05, 31.75) * mm, "end": v(273.05, 19.05) * mm});
            skLineSegment(sketch, "E6.19.11.1", {"start": v(284.16, 30.16) * mm, "end": v(274.64, 30.16) * mm});
            skLineSegment(sketch, "E6.22.11.1", {"start": v(284.16, 30.16) * mm, "end": v(284.16, 20.64) * mm});
            skLineSegment(sketch, "E6.0.11.2", {"start": v(285.75, 44.45) * mm, "end": v(273.05, 44.45) * mm});
            skLineSegment(sketch, "E6.3.11.2", {"start": v(274.64, 55.56) * mm, "end": v(274.64, 46.04) * mm});
            skPoint(sketch, "E6.6.11.2", {"position": v(279.4, 50.8) * mm});
            skLineSegment(sketch, "E6.7.11.2", {"start": v(284.16, 46.04) * mm, "end": v(274.64, 46.04) * mm});
            skLineSegment(sketch, "E6.10.11.2", {"start": v(285.75, 57.15) * mm, "end": v(285.75, 44.45) * mm});
            skLineSegment(sketch, "E6.13.11.2", {"start": v(285.75, 57.15) * mm, "end": v(273.05, 57.15) * mm});
            skLineSegment(sketch, "E6.16.11.2", {"start": v(273.05, 57.15) * mm, "end": v(273.05, 44.45) * mm});
            skLineSegment(sketch, "E6.19.11.2", {"start": v(284.16, 55.56) * mm, "end": v(274.64, 55.56) * mm});
            skLineSegment(sketch, "E6.22.11.2", {"start": v(284.16, 55.56) * mm, "end": v(284.16, 46.04) * mm});
            skLineSegment(sketch, "E6.0.11.3", {"start": v(285.75, 69.85) * mm, "end": v(273.05, 69.85) * mm});
            skLineSegment(sketch, "E6.3.11.3", {"start": v(274.64, 80.96) * mm, "end": v(274.64, 71.44) * mm});
            skPoint(sketch, "E6.6.11.3", {"position": v(279.4, 76.2) * mm});
            skLineSegment(sketch, "E6.7.11.3", {"start": v(284.16, 71.44) * mm, "end": v(274.64, 71.44) * mm});
            skLineSegment(sketch, "E6.10.11.3", {"start": v(285.75, 82.55) * mm, "end": v(285.75, 69.85) * mm});
            skLineSegment(sketch, "E6.13.11.3", {"start": v(285.75, 82.55) * mm, "end": v(273.05, 82.55) * mm});
            skLineSegment(sketch, "E6.16.11.3", {"start": v(273.05, 82.55) * mm, "end": v(273.05, 69.85) * mm});
            skLineSegment(sketch, "E6.19.11.3", {"start": v(284.16, 80.96) * mm, "end": v(274.64, 80.96) * mm});
            skLineSegment(sketch, "E6.22.11.3", {"start": v(284.16, 80.96) * mm, "end": v(284.16, 71.44) * mm});
            skLineSegment(sketch, "E6.0.11.4", {"start": v(285.75, 95.25) * mm, "end": v(273.05, 95.25) * mm});
            skLineSegment(sketch, "E6.3.11.4", {"start": v(274.64, 106.36) * mm, "end": v(274.64, 96.84) * mm});
            skPoint(sketch, "E6.6.11.4", {"position": v(279.4, 101.6) * mm});
            skLineSegment(sketch, "E6.7.11.4", {"start": v(284.16, 96.84) * mm, "end": v(274.64, 96.84) * mm});
            skLineSegment(sketch, "E6.10.11.4", {"start": v(285.75, 107.95) * mm, "end": v(285.75, 95.25) * mm});
            skLineSegment(sketch, "E6.13.11.4", {"start": v(285.75, 107.95) * mm, "end": v(273.05, 107.95) * mm});
            skLineSegment(sketch, "E6.16.11.4", {"start": v(273.05, 107.95) * mm, "end": v(273.05, 95.25) * mm});
            skLineSegment(sketch, "E6.19.11.4", {"start": v(284.16, 106.36) * mm, "end": v(274.64, 106.36) * mm});
            skLineSegment(sketch, "E6.22.11.4", {"start": v(284.16, 106.36) * mm, "end": v(284.16, 96.84) * mm});
            skLineSegment(sketch, "E6.0.11.5", {"start": v(285.75, 120.65) * mm, "end": v(273.05, 120.65) * mm});
            skLineSegment(sketch, "E6.3.11.5", {"start": v(274.64, 131.76) * mm, "end": v(274.64, 122.24) * mm});
            skPoint(sketch, "E6.6.11.5", {"position": v(279.4, 127) * mm});
            skLineSegment(sketch, "E6.7.11.5", {"start": v(284.16, 122.24) * mm, "end": v(274.64, 122.24) * mm});
            skLineSegment(sketch, "E6.10.11.5", {"start": v(285.75, 133.35) * mm, "end": v(285.75, 120.65) * mm});
            skLineSegment(sketch, "E6.13.11.5", {"start": v(285.75, 133.35) * mm, "end": v(273.05, 133.35) * mm});
            skLineSegment(sketch, "E6.16.11.5", {"start": v(273.05, 133.35) * mm, "end": v(273.05, 120.65) * mm});
            skLineSegment(sketch, "E6.19.11.5", {"start": v(284.16, 131.76) * mm, "end": v(274.64, 131.76) * mm});
            skLineSegment(sketch, "E6.22.11.5", {"start": v(284.16, 131.76) * mm, "end": v(284.16, 122.24) * mm});
            skLineSegment(sketch, "E6.0.11.6", {"start": v(285.75, 146.05) * mm, "end": v(273.05, 146.05) * mm});
            skLineSegment(sketch, "E6.3.11.6", {"start": v(274.64, 157.16) * mm, "end": v(274.64, 147.64) * mm});
            skPoint(sketch, "E6.6.11.6", {"position": v(279.4, 152.4) * mm});
            skLineSegment(sketch, "E6.7.11.6", {"start": v(284.16, 147.64) * mm, "end": v(274.64, 147.64) * mm});
            skLineSegment(sketch, "E6.10.11.6", {"start": v(285.75, 158.75) * mm, "end": v(285.75, 146.05) * mm});
            skLineSegment(sketch, "E6.13.11.6", {"start": v(285.75, 158.75) * mm, "end": v(273.05, 158.75) * mm});
            skLineSegment(sketch, "E6.16.11.6", {"start": v(273.05, 158.75) * mm, "end": v(273.05, 146.05) * mm});
            skLineSegment(sketch, "E6.19.11.6", {"start": v(284.16, 157.16) * mm, "end": v(274.64, 157.16) * mm});
            skLineSegment(sketch, "E6.22.11.6", {"start": v(284.16, 157.16) * mm, "end": v(284.16, 147.64) * mm});
            skLineSegment(sketch, "E6.0.11.7", {"start": v(285.75, 171.45) * mm, "end": v(273.05, 171.45) * mm});
            skLineSegment(sketch, "E6.3.11.7", {"start": v(274.64, 182.56) * mm, "end": v(274.64, 173.04) * mm});
            skPoint(sketch, "E6.6.11.7", {"position": v(279.4, 177.8) * mm});
            skLineSegment(sketch, "E6.7.11.7", {"start": v(284.16, 173.04) * mm, "end": v(274.64, 173.04) * mm});
            skLineSegment(sketch, "E6.10.11.7", {"start": v(285.75, 184.15) * mm, "end": v(285.75, 171.45) * mm});
            skLineSegment(sketch, "E6.13.11.7", {"start": v(285.75, 184.15) * mm, "end": v(273.05, 184.15) * mm});
            skLineSegment(sketch, "E6.16.11.7", {"start": v(273.05, 184.15) * mm, "end": v(273.05, 171.45) * mm});
            skLineSegment(sketch, "E6.19.11.7", {"start": v(284.16, 182.56) * mm, "end": v(274.64, 182.56) * mm});
            skLineSegment(sketch, "E6.22.11.7", {"start": v(284.16, 182.56) * mm, "end": v(284.16, 173.04) * mm});
            skLineSegment(sketch, "E6.0.11.8", {"start": v(285.75, 196.85) * mm, "end": v(273.05, 196.85) * mm});
            skLineSegment(sketch, "E6.3.11.8", {"start": v(274.64, 207.96) * mm, "end": v(274.64, 198.44) * mm});
            skPoint(sketch, "E6.6.11.8", {"position": v(279.4, 203.2) * mm});
            skLineSegment(sketch, "E6.7.11.8", {"start": v(284.16, 198.44) * mm, "end": v(274.64, 198.44) * mm});
            skLineSegment(sketch, "E6.10.11.8", {"start": v(285.75, 209.55) * mm, "end": v(285.75, 196.85) * mm});
            skLineSegment(sketch, "E6.13.11.8", {"start": v(285.75, 209.55) * mm, "end": v(273.05, 209.55) * mm});
            skLineSegment(sketch, "E6.16.11.8", {"start": v(273.05, 209.55) * mm, "end": v(273.05, 196.85) * mm});
            skLineSegment(sketch, "E6.19.11.8", {"start": v(284.16, 207.96) * mm, "end": v(274.64, 207.96) * mm});
            skLineSegment(sketch, "E6.22.11.8", {"start": v(284.16, 207.96) * mm, "end": v(284.16, 198.44) * mm});
            skLineSegment(sketch, "E6.0.11.9", {"start": v(285.75, 222.25) * mm, "end": v(273.05, 222.25) * mm});
            skLineSegment(sketch, "E6.3.11.9", {"start": v(274.64, 233.36) * mm, "end": v(274.64, 223.84) * mm});
            skPoint(sketch, "E6.6.11.9", {"position": v(279.4, 228.6) * mm});
            skLineSegment(sketch, "E6.7.11.9", {"start": v(284.16, 223.84) * mm, "end": v(274.64, 223.84) * mm});
            skLineSegment(sketch, "E6.10.11.9", {"start": v(285.75, 234.95) * mm, "end": v(285.75, 222.25) * mm});
            skLineSegment(sketch, "E6.13.11.9", {"start": v(285.75, 234.95) * mm, "end": v(273.05, 234.95) * mm});
            skLineSegment(sketch, "E6.16.11.9", {"start": v(273.05, 234.95) * mm, "end": v(273.05, 222.25) * mm});
            skLineSegment(sketch, "E6.19.11.9", {"start": v(284.16, 233.36) * mm, "end": v(274.64, 233.36) * mm});
            skLineSegment(sketch, "E6.22.11.9", {"start": v(284.16, 233.36) * mm, "end": v(284.16, 223.84) * mm});
            skLineSegment(sketch, "E6.0.11.10", {"start": v(285.75, 247.65) * mm, "end": v(273.05, 247.65) * mm});
            skLineSegment(sketch, "E6.3.11.10", {"start": v(274.64, 258.76) * mm, "end": v(274.64, 249.24) * mm});
            skPoint(sketch, "E6.6.11.10", {"position": v(279.4, 254) * mm});
            skLineSegment(sketch, "E6.7.11.10", {"start": v(284.16, 249.24) * mm, "end": v(274.64, 249.24) * mm});
            skLineSegment(sketch, "E6.10.11.10", {"start": v(285.75, 260.35) * mm, "end": v(285.75, 247.65) * mm});
            skLineSegment(sketch, "E6.13.11.10", {"start": v(285.75, 260.35) * mm, "end": v(273.05, 260.35) * mm});
            skLineSegment(sketch, "E6.16.11.10", {"start": v(273.05, 260.35) * mm, "end": v(273.05, 247.65) * mm});
            skLineSegment(sketch, "E6.19.11.10", {"start": v(284.16, 258.76) * mm, "end": v(274.64, 258.76) * mm});
            skLineSegment(sketch, "E6.22.11.10", {"start": v(284.16, 258.76) * mm, "end": v(284.16, 249.24) * mm});
            skLineSegment(sketch, "E6.0.11.11", {"start": v(285.75, 273.05) * mm, "end": v(273.05, 273.05) * mm});
            skLineSegment(sketch, "E6.3.11.11", {"start": v(274.64, 284.16) * mm, "end": v(274.64, 274.64) * mm});
            skPoint(sketch, "E6.6.11.11", {"position": v(279.4, 279.4) * mm});
            skLineSegment(sketch, "E6.7.11.11", {"start": v(284.16, 274.64) * mm, "end": v(274.64, 274.64) * mm});
            skLineSegment(sketch, "E6.10.11.11", {"start": v(285.75, 285.75) * mm, "end": v(285.75, 273.05) * mm});
            skLineSegment(sketch, "E6.13.11.11", {"start": v(285.75, 285.75) * mm, "end": v(273.05, 285.75) * mm});
            skLineSegment(sketch, "E6.16.11.11", {"start": v(273.05, 285.75) * mm, "end": v(273.05, 273.05) * mm});
            skLineSegment(sketch, "E6.19.11.11", {"start": v(284.16, 284.16) * mm, "end": v(274.64, 284.16) * mm});
            skLineSegment(sketch, "E6.22.11.11", {"start": v(284.16, 284.16) * mm, "end": v(284.16, 274.64) * mm});
            skLineSegment(sketch, "E6.0.11.12", {"start": v(285.75, 298.45) * mm, "end": v(273.05, 298.45) * mm});
            skLineSegment(sketch, "E6.3.11.12", {"start": v(274.64, 309.56) * mm, "end": v(274.64, 300.04) * mm});
            skPoint(sketch, "E6.6.11.12", {"position": v(279.4, 304.8) * mm});
            skLineSegment(sketch, "E6.7.11.12", {"start": v(284.16, 300.04) * mm, "end": v(274.64, 300.04) * mm});
            skLineSegment(sketch, "E6.10.11.12", {"start": v(285.75, 311.15) * mm, "end": v(285.75, 298.45) * mm});
            skLineSegment(sketch, "E6.13.11.12", {"start": v(285.75, 311.15) * mm, "end": v(273.05, 311.15) * mm});
            skLineSegment(sketch, "E6.16.11.12", {"start": v(273.05, 311.15) * mm, "end": v(273.05, 298.45) * mm});
            skLineSegment(sketch, "E6.19.11.12", {"start": v(284.16, 309.56) * mm, "end": v(274.64, 309.56) * mm});
            skLineSegment(sketch, "E6.22.11.12", {"start": v(284.16, 309.56) * mm, "end": v(284.16, 300.04) * mm});
            skLineSegment(sketch, "E6.0.11.13", {"start": v(285.75, 323.85) * mm, "end": v(273.05, 323.85) * mm});
            skLineSegment(sketch, "E6.3.11.13", {"start": v(274.64, 334.96) * mm, "end": v(274.64, 325.44) * mm});
            skPoint(sketch, "E6.6.11.13", {"position": v(279.4, 330.2) * mm});
            skLineSegment(sketch, "E6.7.11.13", {"start": v(284.16, 325.44) * mm, "end": v(274.64, 325.44) * mm});
            skLineSegment(sketch, "E6.10.11.13", {"start": v(285.75, 336.55) * mm, "end": v(285.75, 323.85) * mm});
            skLineSegment(sketch, "E6.13.11.13", {"start": v(285.75, 336.55) * mm, "end": v(273.05, 336.55) * mm});
            skLineSegment(sketch, "E6.16.11.13", {"start": v(273.05, 336.55) * mm, "end": v(273.05, 323.85) * mm});
            skLineSegment(sketch, "E6.19.11.13", {"start": v(284.16, 334.96) * mm, "end": v(274.64, 334.96) * mm});
            skLineSegment(sketch, "E6.22.11.13", {"start": v(284.16, 334.96) * mm, "end": v(284.16, 325.44) * mm});
            skLineSegment(sketch, "E6.0.11.14", {"start": v(285.75, 349.25) * mm, "end": v(273.05, 349.25) * mm});
            skLineSegment(sketch, "E6.3.11.14", {"start": v(274.64, 360.36) * mm, "end": v(274.64, 350.84) * mm});
            skPoint(sketch, "E6.6.11.14", {"position": v(279.4, 355.6) * mm});
            skLineSegment(sketch, "E6.7.11.14", {"start": v(284.16, 350.84) * mm, "end": v(274.64, 350.84) * mm});
            skLineSegment(sketch, "E6.10.11.14", {"start": v(285.75, 361.95) * mm, "end": v(285.75, 349.25) * mm});
            skLineSegment(sketch, "E6.13.11.14", {"start": v(285.75, 361.95) * mm, "end": v(273.05, 361.95) * mm});
            skLineSegment(sketch, "E6.16.11.14", {"start": v(273.05, 361.95) * mm, "end": v(273.05, 349.25) * mm});
            skLineSegment(sketch, "E6.19.11.14", {"start": v(284.16, 360.36) * mm, "end": v(274.64, 360.36) * mm});
            skLineSegment(sketch, "E6.22.11.14", {"start": v(284.16, 360.36) * mm, "end": v(284.16, 350.84) * mm});
            skLineSegment(sketch, "E6.0.11.15", {"start": v(285.75, 374.65) * mm, "end": v(273.05, 374.65) * mm});
            skLineSegment(sketch, "E6.3.11.15", {"start": v(274.64, 385.76) * mm, "end": v(274.64, 376.24) * mm});
            skPoint(sketch, "E6.6.11.15", {"position": v(279.4, 381) * mm});
            skLineSegment(sketch, "E6.7.11.15", {"start": v(284.16, 376.24) * mm, "end": v(274.64, 376.24) * mm});
            skLineSegment(sketch, "E6.10.11.15", {"start": v(285.75, 387.35) * mm, "end": v(285.75, 374.65) * mm});
            skLineSegment(sketch, "E6.13.11.15", {"start": v(285.75, 387.35) * mm, "end": v(273.05, 387.35) * mm});
            skLineSegment(sketch, "E6.16.11.15", {"start": v(273.05, 387.35) * mm, "end": v(273.05, 374.65) * mm});
            skLineSegment(sketch, "E6.19.11.15", {"start": v(284.16, 385.76) * mm, "end": v(274.64, 385.76) * mm});
            skLineSegment(sketch, "E6.22.11.15", {"start": v(284.16, 385.76) * mm, "end": v(284.16, 376.24) * mm});
            skLineSegment(sketch, "E6.0.11.16", {"start": v(285.75, 400.05) * mm, "end": v(273.05, 400.05) * mm});
            skLineSegment(sketch, "E6.3.11.16", {"start": v(274.64, 411.16) * mm, "end": v(274.64, 401.64) * mm});
            skPoint(sketch, "E6.6.11.16", {"position": v(279.4, 406.4) * mm});
            skLineSegment(sketch, "E6.7.11.16", {"start": v(284.16, 401.64) * mm, "end": v(274.64, 401.64) * mm});
            skLineSegment(sketch, "E6.10.11.16", {"start": v(285.75, 412.75) * mm, "end": v(285.75, 400.05) * mm});
            skLineSegment(sketch, "E6.13.11.16", {"start": v(285.75, 412.75) * mm, "end": v(273.05, 412.75) * mm});
            skLineSegment(sketch, "E6.16.11.16", {"start": v(273.05, 412.75) * mm, "end": v(273.05, 400.05) * mm});
            skLineSegment(sketch, "E6.19.11.16", {"start": v(284.16, 411.16) * mm, "end": v(274.64, 411.16) * mm});
            skLineSegment(sketch, "E6.22.11.16", {"start": v(284.16, 411.16) * mm, "end": v(284.16, 401.64) * mm});
            skLineSegment(sketch, "E6.0.11.17", {"start": v(285.75, 425.45) * mm, "end": v(273.05, 425.45) * mm});
            skLineSegment(sketch, "E6.3.11.17", {"start": v(274.64, 436.56) * mm, "end": v(274.64, 427.04) * mm});
            skPoint(sketch, "E6.6.11.17", {"position": v(279.4, 431.8) * mm});
            skLineSegment(sketch, "E6.7.11.17", {"start": v(284.16, 427.04) * mm, "end": v(274.64, 427.04) * mm});
            skLineSegment(sketch, "E6.10.11.17", {"start": v(285.75, 438.15) * mm, "end": v(285.75, 425.45) * mm});
            skLineSegment(sketch, "E6.13.11.17", {"start": v(285.75, 438.15) * mm, "end": v(273.05, 438.15) * mm});
            skLineSegment(sketch, "E6.16.11.17", {"start": v(273.05, 438.15) * mm, "end": v(273.05, 425.45) * mm});
            skLineSegment(sketch, "E6.19.11.17", {"start": v(284.16, 436.56) * mm, "end": v(274.64, 436.56) * mm});
            skLineSegment(sketch, "E6.22.11.17", {"start": v(284.16, 436.56) * mm, "end": v(284.16, 427.04) * mm});
            skLineSegment(sketch, "E6.0.11.18", {"start": v(285.75, 450.85) * mm, "end": v(273.05, 450.85) * mm});
            skLineSegment(sketch, "E6.3.11.18", {"start": v(274.64, 461.96) * mm, "end": v(274.64, 452.44) * mm});
            skPoint(sketch, "E6.6.11.18", {"position": v(279.4, 457.2) * mm});
            skLineSegment(sketch, "E6.7.11.18", {"start": v(284.16, 452.44) * mm, "end": v(274.64, 452.44) * mm});
            skLineSegment(sketch, "E6.10.11.18", {"start": v(285.75, 463.55) * mm, "end": v(285.75, 450.85) * mm});
            skLineSegment(sketch, "E6.13.11.18", {"start": v(285.75, 463.55) * mm, "end": v(273.05, 463.55) * mm});
            skLineSegment(sketch, "E6.16.11.18", {"start": v(273.05, 463.55) * mm, "end": v(273.05, 450.85) * mm});
            skLineSegment(sketch, "E6.19.11.18", {"start": v(284.16, 461.96) * mm, "end": v(274.64, 461.96) * mm});
            skLineSegment(sketch, "E6.22.11.18", {"start": v(284.16, 461.96) * mm, "end": v(284.16, 452.44) * mm});
            skLineSegment(sketch, "E6.0.11.19", {"start": v(285.75, 476.25) * mm, "end": v(273.05, 476.25) * mm});
            skLineSegment(sketch, "E6.3.11.19", {"start": v(274.64, 487.36) * mm, "end": v(274.64, 477.84) * mm});
            skPoint(sketch, "E6.6.11.19", {"position": v(279.4, 482.6) * mm});
            skLineSegment(sketch, "E6.7.11.19", {"start": v(284.16, 477.84) * mm, "end": v(274.64, 477.84) * mm});
            skLineSegment(sketch, "E6.10.11.19", {"start": v(285.75, 488.95) * mm, "end": v(285.75, 476.25) * mm});
            skLineSegment(sketch, "E6.13.11.19", {"start": v(285.75, 488.95) * mm, "end": v(273.05, 488.95) * mm});
            skLineSegment(sketch, "E6.16.11.19", {"start": v(273.05, 488.95) * mm, "end": v(273.05, 476.25) * mm});
            skLineSegment(sketch, "E6.19.11.19", {"start": v(284.16, 487.36) * mm, "end": v(274.64, 487.36) * mm});
            skLineSegment(sketch, "E6.22.11.19", {"start": v(284.16, 487.36) * mm, "end": v(284.16, 477.84) * mm});
            skLineSegment(sketch, "E6.0.11.20", {"start": v(285.75, 501.65) * mm, "end": v(273.05, 501.65) * mm});
            skLineSegment(sketch, "E6.3.11.20", {"start": v(274.64, 512.76) * mm, "end": v(274.64, 503.24) * mm});
            skPoint(sketch, "E6.6.11.20", {"position": v(279.4, 508) * mm});
            skLineSegment(sketch, "E6.7.11.20", {"start": v(284.16, 503.24) * mm, "end": v(274.64, 503.24) * mm});
            skLineSegment(sketch, "E6.10.11.20", {"start": v(285.75, 514.35) * mm, "end": v(285.75, 501.65) * mm});
            skLineSegment(sketch, "E6.13.11.20", {"start": v(285.75, 514.35) * mm, "end": v(273.05, 514.35) * mm});
            skLineSegment(sketch, "E6.16.11.20", {"start": v(273.05, 514.35) * mm, "end": v(273.05, 501.65) * mm});
            skLineSegment(sketch, "E6.19.11.20", {"start": v(284.16, 512.76) * mm, "end": v(274.64, 512.76) * mm});
            skLineSegment(sketch, "E6.22.11.20", {"start": v(284.16, 512.76) * mm, "end": v(284.16, 503.24) * mm});
            skLineSegment(sketch, "E6.0.11.21", {"start": v(285.75, 527.05) * mm, "end": v(273.05, 527.05) * mm});
            skLineSegment(sketch, "E6.3.11.21", {"start": v(274.64, 538.16) * mm, "end": v(274.64, 528.64) * mm});
            skPoint(sketch, "E6.6.11.21", {"position": v(279.4, 533.4) * mm});
            skLineSegment(sketch, "E6.7.11.21", {"start": v(284.16, 528.64) * mm, "end": v(274.64, 528.64) * mm});
            skLineSegment(sketch, "E6.10.11.21", {"start": v(285.75, 539.75) * mm, "end": v(285.75, 527.05) * mm});
            skLineSegment(sketch, "E6.13.11.21", {"start": v(285.75, 539.75) * mm, "end": v(273.05, 539.75) * mm});
            skLineSegment(sketch, "E6.16.11.21", {"start": v(273.05, 539.75) * mm, "end": v(273.05, 527.05) * mm});
            skLineSegment(sketch, "E6.19.11.21", {"start": v(284.16, 538.16) * mm, "end": v(274.64, 538.16) * mm});
            skLineSegment(sketch, "E6.22.11.21", {"start": v(284.16, 538.16) * mm, "end": v(284.16, 528.64) * mm});
            skLineSegment(sketch, "E6.0.12.0", {"start": v(311.15, -6.35) * mm, "end": v(298.45, -6.35) * mm});
            skLineSegment(sketch, "E6.3.12.0", {"start": v(300.04, 4.76) * mm, "end": v(300.04, -4.76) * mm});
            skPoint(sketch, "E6.6.12.0", {"position": v(304.8, 0) * mm});
            skLineSegment(sketch, "E6.7.12.0", {"start": v(309.56, -4.76) * mm, "end": v(300.04, -4.76) * mm});
            skLineSegment(sketch, "E6.10.12.0", {"start": v(311.15, 6.35) * mm, "end": v(311.15, -6.35) * mm});
            skLineSegment(sketch, "E6.13.12.0", {"start": v(311.15, 6.35) * mm, "end": v(298.45, 6.35) * mm});
            skLineSegment(sketch, "E6.16.12.0", {"start": v(298.45, 6.35) * mm, "end": v(298.45, -6.35) * mm});
            skLineSegment(sketch, "E6.19.12.0", {"start": v(309.56, 4.76) * mm, "end": v(300.04, 4.76) * mm});
            skLineSegment(sketch, "E6.22.12.0", {"start": v(309.56, 4.76) * mm, "end": v(309.56, -4.76) * mm});
            skLineSegment(sketch, "E6.0.12.1", {"start": v(311.15, 19.05) * mm, "end": v(298.45, 19.05) * mm});
            skLineSegment(sketch, "E6.3.12.1", {"start": v(300.04, 30.16) * mm, "end": v(300.04, 20.64) * mm});
            skPoint(sketch, "E6.6.12.1", {"position": v(304.8, 25.4) * mm});
            skLineSegment(sketch, "E6.7.12.1", {"start": v(309.56, 20.64) * mm, "end": v(300.04, 20.64) * mm});
            skLineSegment(sketch, "E6.10.12.1", {"start": v(311.15, 31.75) * mm, "end": v(311.15, 19.05) * mm});
            skLineSegment(sketch, "E6.13.12.1", {"start": v(311.15, 31.75) * mm, "end": v(298.45, 31.75) * mm});
            skLineSegment(sketch, "E6.16.12.1", {"start": v(298.45, 31.75) * mm, "end": v(298.45, 19.05) * mm});
            skLineSegment(sketch, "E6.19.12.1", {"start": v(309.56, 30.16) * mm, "end": v(300.04, 30.16) * mm});
            skLineSegment(sketch, "E6.22.12.1", {"start": v(309.56, 30.16) * mm, "end": v(309.56, 20.64) * mm});
            skLineSegment(sketch, "E6.0.12.2", {"start": v(311.15, 44.45) * mm, "end": v(298.45, 44.45) * mm});
            skLineSegment(sketch, "E6.3.12.2", {"start": v(300.04, 55.56) * mm, "end": v(300.04, 46.04) * mm});
            skPoint(sketch, "E6.6.12.2", {"position": v(304.8, 50.8) * mm});
            skLineSegment(sketch, "E6.7.12.2", {"start": v(309.56, 46.04) * mm, "end": v(300.04, 46.04) * mm});
            skLineSegment(sketch, "E6.10.12.2", {"start": v(311.15, 57.15) * mm, "end": v(311.15, 44.45) * mm});
            skLineSegment(sketch, "E6.13.12.2", {"start": v(311.15, 57.15) * mm, "end": v(298.45, 57.15) * mm});
            skLineSegment(sketch, "E6.16.12.2", {"start": v(298.45, 57.15) * mm, "end": v(298.45, 44.45) * mm});
            skLineSegment(sketch, "E6.19.12.2", {"start": v(309.56, 55.56) * mm, "end": v(300.04, 55.56) * mm});
            skLineSegment(sketch, "E6.22.12.2", {"start": v(309.56, 55.56) * mm, "end": v(309.56, 46.04) * mm});
            skLineSegment(sketch, "E6.0.12.3", {"start": v(311.15, 69.85) * mm, "end": v(298.45, 69.85) * mm});
            skLineSegment(sketch, "E6.3.12.3", {"start": v(300.04, 80.96) * mm, "end": v(300.04, 71.44) * mm});
            skPoint(sketch, "E6.6.12.3", {"position": v(304.8, 76.2) * mm});
            skLineSegment(sketch, "E6.7.12.3", {"start": v(309.56, 71.44) * mm, "end": v(300.04, 71.44) * mm});
            skLineSegment(sketch, "E6.10.12.3", {"start": v(311.15, 82.55) * mm, "end": v(311.15, 69.85) * mm});
            skLineSegment(sketch, "E6.13.12.3", {"start": v(311.15, 82.55) * mm, "end": v(298.45, 82.55) * mm});
            skLineSegment(sketch, "E6.16.12.3", {"start": v(298.45, 82.55) * mm, "end": v(298.45, 69.85) * mm});
            skLineSegment(sketch, "E6.19.12.3", {"start": v(309.56, 80.96) * mm, "end": v(300.04, 80.96) * mm});
            skLineSegment(sketch, "E6.22.12.3", {"start": v(309.56, 80.96) * mm, "end": v(309.56, 71.44) * mm});
            skLineSegment(sketch, "E6.0.12.4", {"start": v(311.15, 95.25) * mm, "end": v(298.45, 95.25) * mm});
            skLineSegment(sketch, "E6.3.12.4", {"start": v(300.04, 106.36) * mm, "end": v(300.04, 96.84) * mm});
            skPoint(sketch, "E6.6.12.4", {"position": v(304.8, 101.6) * mm});
            skLineSegment(sketch, "E6.7.12.4", {"start": v(309.56, 96.84) * mm, "end": v(300.04, 96.84) * mm});
            skLineSegment(sketch, "E6.10.12.4", {"start": v(311.15, 107.95) * mm, "end": v(311.15, 95.25) * mm});
            skLineSegment(sketch, "E6.13.12.4", {"start": v(311.15, 107.95) * mm, "end": v(298.45, 107.95) * mm});
            skLineSegment(sketch, "E6.16.12.4", {"start": v(298.45, 107.95) * mm, "end": v(298.45, 95.25) * mm});
            skLineSegment(sketch, "E6.19.12.4", {"start": v(309.56, 106.36) * mm, "end": v(300.04, 106.36) * mm});
            skLineSegment(sketch, "E6.22.12.4", {"start": v(309.56, 106.36) * mm, "end": v(309.56, 96.84) * mm});
            skLineSegment(sketch, "E6.0.12.5", {"start": v(311.15, 120.65) * mm, "end": v(298.45, 120.65) * mm});
            skLineSegment(sketch, "E6.3.12.5", {"start": v(300.04, 131.76) * mm, "end": v(300.04, 122.24) * mm});
            skPoint(sketch, "E6.6.12.5", {"position": v(304.8, 127) * mm});
            skLineSegment(sketch, "E6.7.12.5", {"start": v(309.56, 122.24) * mm, "end": v(300.04, 122.24) * mm});
            skLineSegment(sketch, "E6.10.12.5", {"start": v(311.15, 133.35) * mm, "end": v(311.15, 120.65) * mm});
            skLineSegment(sketch, "E6.13.12.5", {"start": v(311.15, 133.35) * mm, "end": v(298.45, 133.35) * mm});
            skLineSegment(sketch, "E6.16.12.5", {"start": v(298.45, 133.35) * mm, "end": v(298.45, 120.65) * mm});
            skLineSegment(sketch, "E6.19.12.5", {"start": v(309.56, 131.76) * mm, "end": v(300.04, 131.76) * mm});
            skLineSegment(sketch, "E6.22.12.5", {"start": v(309.56, 131.76) * mm, "end": v(309.56, 122.24) * mm});
            skLineSegment(sketch, "E6.0.12.6", {"start": v(311.15, 146.05) * mm, "end": v(298.45, 146.05) * mm});
            skLineSegment(sketch, "E6.3.12.6", {"start": v(300.04, 157.16) * mm, "end": v(300.04, 147.64) * mm});
            skPoint(sketch, "E6.6.12.6", {"position": v(304.8, 152.4) * mm});
            skLineSegment(sketch, "E6.7.12.6", {"start": v(309.56, 147.64) * mm, "end": v(300.04, 147.64) * mm});
            skLineSegment(sketch, "E6.10.12.6", {"start": v(311.15, 158.75) * mm, "end": v(311.15, 146.05) * mm});
            skLineSegment(sketch, "E6.13.12.6", {"start": v(311.15, 158.75) * mm, "end": v(298.45, 158.75) * mm});
            skLineSegment(sketch, "E6.16.12.6", {"start": v(298.45, 158.75) * mm, "end": v(298.45, 146.05) * mm});
            skLineSegment(sketch, "E6.19.12.6", {"start": v(309.56, 157.16) * mm, "end": v(300.04, 157.16) * mm});
            skLineSegment(sketch, "E6.22.12.6", {"start": v(309.56, 157.16) * mm, "end": v(309.56, 147.64) * mm});
            skLineSegment(sketch, "E6.0.12.7", {"start": v(311.15, 171.45) * mm, "end": v(298.45, 171.45) * mm});
            skLineSegment(sketch, "E6.3.12.7", {"start": v(300.04, 182.56) * mm, "end": v(300.04, 173.04) * mm});
            skPoint(sketch, "E6.6.12.7", {"position": v(304.8, 177.8) * mm});
            skLineSegment(sketch, "E6.7.12.7", {"start": v(309.56, 173.04) * mm, "end": v(300.04, 173.04) * mm});
            skLineSegment(sketch, "E6.10.12.7", {"start": v(311.15, 184.15) * mm, "end": v(311.15, 171.45) * mm});
            skLineSegment(sketch, "E6.13.12.7", {"start": v(311.15, 184.15) * mm, "end": v(298.45, 184.15) * mm});
            skLineSegment(sketch, "E6.16.12.7", {"start": v(298.45, 184.15) * mm, "end": v(298.45, 171.45) * mm});
            skLineSegment(sketch, "E6.19.12.7", {"start": v(309.56, 182.56) * mm, "end": v(300.04, 182.56) * mm});
            skLineSegment(sketch, "E6.22.12.7", {"start": v(309.56, 182.56) * mm, "end": v(309.56, 173.04) * mm});
            skLineSegment(sketch, "E6.0.12.8", {"start": v(311.15, 196.85) * mm, "end": v(298.45, 196.85) * mm});
            skLineSegment(sketch, "E6.3.12.8", {"start": v(300.04, 207.96) * mm, "end": v(300.04, 198.44) * mm});
            skPoint(sketch, "E6.6.12.8", {"position": v(304.8, 203.2) * mm});
            skLineSegment(sketch, "E6.7.12.8", {"start": v(309.56, 198.44) * mm, "end": v(300.04, 198.44) * mm});
            skLineSegment(sketch, "E6.10.12.8", {"start": v(311.15, 209.55) * mm, "end": v(311.15, 196.85) * mm});
            skLineSegment(sketch, "E6.13.12.8", {"start": v(311.15, 209.55) * mm, "end": v(298.45, 209.55) * mm});
            skLineSegment(sketch, "E6.16.12.8", {"start": v(298.45, 209.55) * mm, "end": v(298.45, 196.85) * mm});
            skLineSegment(sketch, "E6.19.12.8", {"start": v(309.56, 207.96) * mm, "end": v(300.04, 207.96) * mm});
            skLineSegment(sketch, "E6.22.12.8", {"start": v(309.56, 207.96) * mm, "end": v(309.56, 198.44) * mm});
            skLineSegment(sketch, "E6.0.12.9", {"start": v(311.15, 222.25) * mm, "end": v(298.45, 222.25) * mm});
            skLineSegment(sketch, "E6.3.12.9", {"start": v(300.04, 233.36) * mm, "end": v(300.04, 223.84) * mm});
            skPoint(sketch, "E6.6.12.9", {"position": v(304.8, 228.6) * mm});
            skLineSegment(sketch, "E6.7.12.9", {"start": v(309.56, 223.84) * mm, "end": v(300.04, 223.84) * mm});
            skLineSegment(sketch, "E6.10.12.9", {"start": v(311.15, 234.95) * mm, "end": v(311.15, 222.25) * mm});
            skLineSegment(sketch, "E6.13.12.9", {"start": v(311.15, 234.95) * mm, "end": v(298.45, 234.95) * mm});
            skLineSegment(sketch, "E6.16.12.9", {"start": v(298.45, 234.95) * mm, "end": v(298.45, 222.25) * mm});
            skLineSegment(sketch, "E6.19.12.9", {"start": v(309.56, 233.36) * mm, "end": v(300.04, 233.36) * mm});
            skLineSegment(sketch, "E6.22.12.9", {"start": v(309.56, 233.36) * mm, "end": v(309.56, 223.84) * mm});
            skLineSegment(sketch, "E6.0.12.10", {"start": v(311.15, 247.65) * mm, "end": v(298.45, 247.65) * mm});
            skLineSegment(sketch, "E6.3.12.10", {"start": v(300.04, 258.76) * mm, "end": v(300.04, 249.24) * mm});
            skPoint(sketch, "E6.6.12.10", {"position": v(304.8, 254) * mm});
            skLineSegment(sketch, "E6.7.12.10", {"start": v(309.56, 249.24) * mm, "end": v(300.04, 249.24) * mm});
            skLineSegment(sketch, "E6.10.12.10", {"start": v(311.15, 260.35) * mm, "end": v(311.15, 247.65) * mm});
            skLineSegment(sketch, "E6.13.12.10", {"start": v(311.15, 260.35) * mm, "end": v(298.45, 260.35) * mm});
            skLineSegment(sketch, "E6.16.12.10", {"start": v(298.45, 260.35) * mm, "end": v(298.45, 247.65) * mm});
            skLineSegment(sketch, "E6.19.12.10", {"start": v(309.56, 258.76) * mm, "end": v(300.04, 258.76) * mm});
            skLineSegment(sketch, "E6.22.12.10", {"start": v(309.56, 258.76) * mm, "end": v(309.56, 249.24) * mm});
            skLineSegment(sketch, "E6.0.12.11", {"start": v(311.15, 273.05) * mm, "end": v(298.45, 273.05) * mm});
            skLineSegment(sketch, "E6.3.12.11", {"start": v(300.04, 284.16) * mm, "end": v(300.04, 274.64) * mm});
            skPoint(sketch, "E6.6.12.11", {"position": v(304.8, 279.4) * mm});
            skLineSegment(sketch, "E6.7.12.11", {"start": v(309.56, 274.64) * mm, "end": v(300.04, 274.64) * mm});
            skLineSegment(sketch, "E6.10.12.11", {"start": v(311.15, 285.75) * mm, "end": v(311.15, 273.05) * mm});
            skLineSegment(sketch, "E6.13.12.11", {"start": v(311.15, 285.75) * mm, "end": v(298.45, 285.75) * mm});
            skLineSegment(sketch, "E6.16.12.11", {"start": v(298.45, 285.75) * mm, "end": v(298.45, 273.05) * mm});
            skLineSegment(sketch, "E6.19.12.11", {"start": v(309.56, 284.16) * mm, "end": v(300.04, 284.16) * mm});
            skLineSegment(sketch, "E6.22.12.11", {"start": v(309.56, 284.16) * mm, "end": v(309.56, 274.64) * mm});
            skLineSegment(sketch, "E6.0.12.12", {"start": v(311.15, 298.45) * mm, "end": v(298.45, 298.45) * mm});
            skLineSegment(sketch, "E6.3.12.12", {"start": v(300.04, 309.56) * mm, "end": v(300.04, 300.04) * mm});
            skPoint(sketch, "E6.6.12.12", {"position": v(304.8, 304.8) * mm});
            skLineSegment(sketch, "E6.7.12.12", {"start": v(309.56, 300.04) * mm, "end": v(300.04, 300.04) * mm});
            skLineSegment(sketch, "E6.10.12.12", {"start": v(311.15, 311.15) * mm, "end": v(311.15, 298.45) * mm});
            skLineSegment(sketch, "E6.13.12.12", {"start": v(311.15, 311.15) * mm, "end": v(298.45, 311.15) * mm});
            skLineSegment(sketch, "E6.16.12.12", {"start": v(298.45, 311.15) * mm, "end": v(298.45, 298.45) * mm});
            skLineSegment(sketch, "E6.19.12.12", {"start": v(309.56, 309.56) * mm, "end": v(300.04, 309.56) * mm});
            skLineSegment(sketch, "E6.22.12.12", {"start": v(309.56, 309.56) * mm, "end": v(309.56, 300.04) * mm});
            skLineSegment(sketch, "E6.0.12.13", {"start": v(311.15, 323.85) * mm, "end": v(298.45, 323.85) * mm});
            skLineSegment(sketch, "E6.3.12.13", {"start": v(300.04, 334.96) * mm, "end": v(300.04, 325.44) * mm});
            skPoint(sketch, "E6.6.12.13", {"position": v(304.8, 330.2) * mm});
            skLineSegment(sketch, "E6.7.12.13", {"start": v(309.56, 325.44) * mm, "end": v(300.04, 325.44) * mm});
            skLineSegment(sketch, "E6.10.12.13", {"start": v(311.15, 336.55) * mm, "end": v(311.15, 323.85) * mm});
            skLineSegment(sketch, "E6.13.12.13", {"start": v(311.15, 336.55) * mm, "end": v(298.45, 336.55) * mm});
            skLineSegment(sketch, "E6.16.12.13", {"start": v(298.45, 336.55) * mm, "end": v(298.45, 323.85) * mm});
            skLineSegment(sketch, "E6.19.12.13", {"start": v(309.56, 334.96) * mm, "end": v(300.04, 334.96) * mm});
            skLineSegment(sketch, "E6.22.12.13", {"start": v(309.56, 334.96) * mm, "end": v(309.56, 325.44) * mm});
            skLineSegment(sketch, "E6.0.12.14", {"start": v(311.15, 349.25) * mm, "end": v(298.45, 349.25) * mm});
            skLineSegment(sketch, "E6.3.12.14", {"start": v(300.04, 360.36) * mm, "end": v(300.04, 350.84) * mm});
            skPoint(sketch, "E6.6.12.14", {"position": v(304.8, 355.6) * mm});
            skLineSegment(sketch, "E6.7.12.14", {"start": v(309.56, 350.84) * mm, "end": v(300.04, 350.84) * mm});
            skLineSegment(sketch, "E6.10.12.14", {"start": v(311.15, 361.95) * mm, "end": v(311.15, 349.25) * mm});
            skLineSegment(sketch, "E6.13.12.14", {"start": v(311.15, 361.95) * mm, "end": v(298.45, 361.95) * mm});
            skLineSegment(sketch, "E6.16.12.14", {"start": v(298.45, 361.95) * mm, "end": v(298.45, 349.25) * mm});
            skLineSegment(sketch, "E6.19.12.14", {"start": v(309.56, 360.36) * mm, "end": v(300.04, 360.36) * mm});
            skLineSegment(sketch, "E6.22.12.14", {"start": v(309.56, 360.36) * mm, "end": v(309.56, 350.84) * mm});
            skLineSegment(sketch, "E6.0.12.15", {"start": v(311.15, 374.65) * mm, "end": v(298.45, 374.65) * mm});
            skLineSegment(sketch, "E6.3.12.15", {"start": v(300.04, 385.76) * mm, "end": v(300.04, 376.24) * mm});
            skPoint(sketch, "E6.6.12.15", {"position": v(304.8, 381) * mm});
            skLineSegment(sketch, "E6.7.12.15", {"start": v(309.56, 376.24) * mm, "end": v(300.04, 376.24) * mm});
            skLineSegment(sketch, "E6.10.12.15", {"start": v(311.15, 387.35) * mm, "end": v(311.15, 374.65) * mm});
            skLineSegment(sketch, "E6.13.12.15", {"start": v(311.15, 387.35) * mm, "end": v(298.45, 387.35) * mm});
            skLineSegment(sketch, "E6.16.12.15", {"start": v(298.45, 387.35) * mm, "end": v(298.45, 374.65) * mm});
            skLineSegment(sketch, "E6.19.12.15", {"start": v(309.56, 385.76) * mm, "end": v(300.04, 385.76) * mm});
            skLineSegment(sketch, "E6.22.12.15", {"start": v(309.56, 385.76) * mm, "end": v(309.56, 376.24) * mm});
            skLineSegment(sketch, "E6.0.12.16", {"start": v(311.15, 400.05) * mm, "end": v(298.45, 400.05) * mm});
            skLineSegment(sketch, "E6.3.12.16", {"start": v(300.04, 411.16) * mm, "end": v(300.04, 401.64) * mm});
            skPoint(sketch, "E6.6.12.16", {"position": v(304.8, 406.4) * mm});
            skLineSegment(sketch, "E6.7.12.16", {"start": v(309.56, 401.64) * mm, "end": v(300.04, 401.64) * mm});
            skLineSegment(sketch, "E6.10.12.16", {"start": v(311.15, 412.75) * mm, "end": v(311.15, 400.05) * mm});
            skLineSegment(sketch, "E6.13.12.16", {"start": v(311.15, 412.75) * mm, "end": v(298.45, 412.75) * mm});
            skLineSegment(sketch, "E6.16.12.16", {"start": v(298.45, 412.75) * mm, "end": v(298.45, 400.05) * mm});
            skLineSegment(sketch, "E6.19.12.16", {"start": v(309.56, 411.16) * mm, "end": v(300.04, 411.16) * mm});
            skLineSegment(sketch, "E6.22.12.16", {"start": v(309.56, 411.16) * mm, "end": v(309.56, 401.64) * mm});
            skLineSegment(sketch, "E6.0.12.17", {"start": v(311.15, 425.45) * mm, "end": v(298.45, 425.45) * mm});
            skLineSegment(sketch, "E6.3.12.17", {"start": v(300.04, 436.56) * mm, "end": v(300.04, 427.04) * mm});
            skPoint(sketch, "E6.6.12.17", {"position": v(304.8, 431.8) * mm});
            skLineSegment(sketch, "E6.7.12.17", {"start": v(309.56, 427.04) * mm, "end": v(300.04, 427.04) * mm});
            skLineSegment(sketch, "E6.10.12.17", {"start": v(311.15, 438.15) * mm, "end": v(311.15, 425.45) * mm});
            skLineSegment(sketch, "E6.13.12.17", {"start": v(311.15, 438.15) * mm, "end": v(298.45, 438.15) * mm});
            skLineSegment(sketch, "E6.16.12.17", {"start": v(298.45, 438.15) * mm, "end": v(298.45, 425.45) * mm});
            skLineSegment(sketch, "E6.19.12.17", {"start": v(309.56, 436.56) * mm, "end": v(300.04, 436.56) * mm});
            skLineSegment(sketch, "E6.22.12.17", {"start": v(309.56, 436.56) * mm, "end": v(309.56, 427.04) * mm});
            skLineSegment(sketch, "E6.0.12.18", {"start": v(311.15, 450.85) * mm, "end": v(298.45, 450.85) * mm});
            skLineSegment(sketch, "E6.3.12.18", {"start": v(300.04, 461.96) * mm, "end": v(300.04, 452.44) * mm});
            skPoint(sketch, "E6.6.12.18", {"position": v(304.8, 457.2) * mm});
            skLineSegment(sketch, "E6.7.12.18", {"start": v(309.56, 452.44) * mm, "end": v(300.04, 452.44) * mm});
            skLineSegment(sketch, "E6.10.12.18", {"start": v(311.15, 463.55) * mm, "end": v(311.15, 450.85) * mm});
            skLineSegment(sketch, "E6.13.12.18", {"start": v(311.15, 463.55) * mm, "end": v(298.45, 463.55) * mm});
            skLineSegment(sketch, "E6.16.12.18", {"start": v(298.45, 463.55) * mm, "end": v(298.45, 450.85) * mm});
            skLineSegment(sketch, "E6.19.12.18", {"start": v(309.56, 461.96) * mm, "end": v(300.04, 461.96) * mm});
            skLineSegment(sketch, "E6.22.12.18", {"start": v(309.56, 461.96) * mm, "end": v(309.56, 452.44) * mm});
            skLineSegment(sketch, "E6.0.12.19", {"start": v(311.15, 476.25) * mm, "end": v(298.45, 476.25) * mm});
            skLineSegment(sketch, "E6.3.12.19", {"start": v(300.04, 487.36) * mm, "end": v(300.04, 477.84) * mm});
            skPoint(sketch, "E6.6.12.19", {"position": v(304.8, 482.6) * mm});
            skLineSegment(sketch, "E6.7.12.19", {"start": v(309.56, 477.84) * mm, "end": v(300.04, 477.84) * mm});
            skLineSegment(sketch, "E6.10.12.19", {"start": v(311.15, 488.95) * mm, "end": v(311.15, 476.25) * mm});
            skLineSegment(sketch, "E6.13.12.19", {"start": v(311.15, 488.95) * mm, "end": v(298.45, 488.95) * mm});
            skLineSegment(sketch, "E6.16.12.19", {"start": v(298.45, 488.95) * mm, "end": v(298.45, 476.25) * mm});
            skLineSegment(sketch, "E6.19.12.19", {"start": v(309.56, 487.36) * mm, "end": v(300.04, 487.36) * mm});
            skLineSegment(sketch, "E6.22.12.19", {"start": v(309.56, 487.36) * mm, "end": v(309.56, 477.84) * mm});
            skLineSegment(sketch, "E6.0.12.20", {"start": v(311.15, 501.65) * mm, "end": v(298.45, 501.65) * mm});
            skLineSegment(sketch, "E6.3.12.20", {"start": v(300.04, 512.76) * mm, "end": v(300.04, 503.24) * mm});
            skPoint(sketch, "E6.6.12.20", {"position": v(304.8, 508) * mm});
            skLineSegment(sketch, "E6.7.12.20", {"start": v(309.56, 503.24) * mm, "end": v(300.04, 503.24) * mm});
            skLineSegment(sketch, "E6.10.12.20", {"start": v(311.15, 514.35) * mm, "end": v(311.15, 501.65) * mm});
            skLineSegment(sketch, "E6.13.12.20", {"start": v(311.15, 514.35) * mm, "end": v(298.45, 514.35) * mm});
            skLineSegment(sketch, "E6.16.12.20", {"start": v(298.45, 514.35) * mm, "end": v(298.45, 501.65) * mm});
            skLineSegment(sketch, "E6.19.12.20", {"start": v(309.56, 512.76) * mm, "end": v(300.04, 512.76) * mm});
            skLineSegment(sketch, "E6.22.12.20", {"start": v(309.56, 512.76) * mm, "end": v(309.56, 503.24) * mm});
            skLineSegment(sketch, "E6.0.12.21", {"start": v(311.15, 527.05) * mm, "end": v(298.45, 527.05) * mm});
            skLineSegment(sketch, "E6.3.12.21", {"start": v(300.04, 538.16) * mm, "end": v(300.04, 528.64) * mm});
            skPoint(sketch, "E6.6.12.21", {"position": v(304.8, 533.4) * mm});
            skLineSegment(sketch, "E6.7.12.21", {"start": v(309.56, 528.64) * mm, "end": v(300.04, 528.64) * mm});
            skLineSegment(sketch, "E6.10.12.21", {"start": v(311.15, 539.75) * mm, "end": v(311.15, 527.05) * mm});
            skLineSegment(sketch, "E6.13.12.21", {"start": v(311.15, 539.75) * mm, "end": v(298.45, 539.75) * mm});
            skLineSegment(sketch, "E6.16.12.21", {"start": v(298.45, 539.75) * mm, "end": v(298.45, 527.05) * mm});
            skLineSegment(sketch, "E6.19.12.21", {"start": v(309.56, 538.16) * mm, "end": v(300.04, 538.16) * mm});
            skLineSegment(sketch, "E6.22.12.21", {"start": v(309.56, 538.16) * mm, "end": v(309.56, 528.64) * mm});
            skLineSegment(sketch, "E7.0", {"start": v(336.55, -6.35) * mm, "end": v(336.55, 552.45) * mm});
            skLineSegment(sketch, "E8", {"start": v(336.55, -6.35) * mm, "end": v(-6.35, -6.35) * mm});
            skLineSegment(sketch, "E9.0.13.0", {"start": v(336.55, -6.35) * mm, "end": v(323.85, -6.35) * mm});
            skLineSegment(sketch, "E9.3.13.0", {"start": v(325.44, 4.76) * mm, "end": v(325.44, -4.76) * mm});
            skPoint(sketch, "E9.6.13.0", {"position": v(330.2, 0) * mm});
            skLineSegment(sketch, "E9.7.13.0", {"start": v(334.96, -4.76) * mm, "end": v(325.44, -4.76) * mm});
            skLineSegment(sketch, "E9.10.13.0", {"start": v(336.55, 6.35) * mm, "end": v(336.55, -6.35) * mm});
            skLineSegment(sketch, "E9.13.13.0", {"start": v(336.55, 6.35) * mm, "end": v(323.85, 6.35) * mm});
            skLineSegment(sketch, "E9.16.13.0", {"start": v(323.85, 6.35) * mm, "end": v(323.85, -6.35) * mm});
            skLineSegment(sketch, "E9.19.13.0", {"start": v(334.96, 4.76) * mm, "end": v(325.44, 4.76) * mm});
            skLineSegment(sketch, "E9.22.13.0", {"start": v(334.96, 4.76) * mm, "end": v(334.96, -4.76) * mm});
            skLineSegment(sketch, "E9.0.13.1", {"start": v(336.55, 19.05) * mm, "end": v(323.85, 19.05) * mm});
            skLineSegment(sketch, "E9.3.13.1", {"start": v(325.44, 30.16) * mm, "end": v(325.44, 20.64) * mm});
            skPoint(sketch, "E9.6.13.1", {"position": v(330.2, 25.4) * mm});
            skLineSegment(sketch, "E9.7.13.1", {"start": v(334.96, 20.64) * mm, "end": v(325.44, 20.64) * mm});
            skLineSegment(sketch, "E9.10.13.1", {"start": v(336.55, 31.75) * mm, "end": v(336.55, 19.05) * mm});
            skLineSegment(sketch, "E9.13.13.1", {"start": v(336.55, 31.75) * mm, "end": v(323.85, 31.75) * mm});
            skLineSegment(sketch, "E9.16.13.1", {"start": v(323.85, 31.75) * mm, "end": v(323.85, 19.05) * mm});
            skLineSegment(sketch, "E9.19.13.1", {"start": v(334.96, 30.16) * mm, "end": v(325.44, 30.16) * mm});
            skLineSegment(sketch, "E9.22.13.1", {"start": v(334.96, 30.16) * mm, "end": v(334.96, 20.64) * mm});
            skLineSegment(sketch, "E9.0.13.2", {"start": v(336.55, 44.45) * mm, "end": v(323.85, 44.45) * mm});
            skLineSegment(sketch, "E9.3.13.2", {"start": v(325.44, 55.56) * mm, "end": v(325.44, 46.04) * mm});
            skPoint(sketch, "E9.6.13.2", {"position": v(330.2, 50.8) * mm});
            skLineSegment(sketch, "E9.7.13.2", {"start": v(334.96, 46.04) * mm, "end": v(325.44, 46.04) * mm});
            skLineSegment(sketch, "E9.10.13.2", {"start": v(336.55, 57.15) * mm, "end": v(336.55, 44.45) * mm});
            skLineSegment(sketch, "E9.13.13.2", {"start": v(336.55, 57.15) * mm, "end": v(323.85, 57.15) * mm});
            skLineSegment(sketch, "E9.16.13.2", {"start": v(323.85, 57.15) * mm, "end": v(323.85, 44.45) * mm});
            skLineSegment(sketch, "E9.19.13.2", {"start": v(334.96, 55.56) * mm, "end": v(325.44, 55.56) * mm});
            skLineSegment(sketch, "E9.22.13.2", {"start": v(334.96, 55.56) * mm, "end": v(334.96, 46.04) * mm});
            skLineSegment(sketch, "E9.0.13.3", {"start": v(336.55, 69.85) * mm, "end": v(323.85, 69.85) * mm});
            skLineSegment(sketch, "E9.3.13.3", {"start": v(325.44, 80.96) * mm, "end": v(325.44, 71.44) * mm});
            skPoint(sketch, "E9.6.13.3", {"position": v(330.2, 76.2) * mm});
            skLineSegment(sketch, "E9.7.13.3", {"start": v(334.96, 71.44) * mm, "end": v(325.44, 71.44) * mm});
            skLineSegment(sketch, "E9.10.13.3", {"start": v(336.55, 82.55) * mm, "end": v(336.55, 69.85) * mm});
            skLineSegment(sketch, "E9.13.13.3", {"start": v(336.55, 82.55) * mm, "end": v(323.85, 82.55) * mm});
            skLineSegment(sketch, "E9.16.13.3", {"start": v(323.85, 82.55) * mm, "end": v(323.85, 69.85) * mm});
            skLineSegment(sketch, "E9.19.13.3", {"start": v(334.96, 80.96) * mm, "end": v(325.44, 80.96) * mm});
            skLineSegment(sketch, "E9.22.13.3", {"start": v(334.96, 80.96) * mm, "end": v(334.96, 71.44) * mm});
            skLineSegment(sketch, "E9.0.13.4", {"start": v(336.55, 95.25) * mm, "end": v(323.85, 95.25) * mm});
            skLineSegment(sketch, "E9.3.13.4", {"start": v(325.44, 106.36) * mm, "end": v(325.44, 96.84) * mm});
            skPoint(sketch, "E9.6.13.4", {"position": v(330.2, 101.6) * mm});
            skLineSegment(sketch, "E9.7.13.4", {"start": v(334.96, 96.84) * mm, "end": v(325.44, 96.84) * mm});
            skLineSegment(sketch, "E9.10.13.4", {"start": v(336.55, 107.95) * mm, "end": v(336.55, 95.25) * mm});
            skLineSegment(sketch, "E9.13.13.4", {"start": v(336.55, 107.95) * mm, "end": v(323.85, 107.95) * mm});
            skLineSegment(sketch, "E9.16.13.4", {"start": v(323.85, 107.95) * mm, "end": v(323.85, 95.25) * mm});
            skLineSegment(sketch, "E9.19.13.4", {"start": v(334.96, 106.36) * mm, "end": v(325.44, 106.36) * mm});
            skLineSegment(sketch, "E9.22.13.4", {"start": v(334.96, 106.36) * mm, "end": v(334.96, 96.84) * mm});
            skLineSegment(sketch, "E9.0.13.5", {"start": v(336.55, 120.65) * mm, "end": v(323.85, 120.65) * mm});
            skLineSegment(sketch, "E9.3.13.5", {"start": v(325.44, 131.76) * mm, "end": v(325.44, 122.24) * mm});
            skPoint(sketch, "E9.6.13.5", {"position": v(330.2, 127) * mm});
            skLineSegment(sketch, "E9.7.13.5", {"start": v(334.96, 122.24) * mm, "end": v(325.44, 122.24) * mm});
            skLineSegment(sketch, "E9.10.13.5", {"start": v(336.55, 133.35) * mm, "end": v(336.55, 120.65) * mm});
            skLineSegment(sketch, "E9.13.13.5", {"start": v(336.55, 133.35) * mm, "end": v(323.85, 133.35) * mm});
            skLineSegment(sketch, "E9.16.13.5", {"start": v(323.85, 133.35) * mm, "end": v(323.85, 120.65) * mm});
            skLineSegment(sketch, "E9.19.13.5", {"start": v(334.96, 131.76) * mm, "end": v(325.44, 131.76) * mm});
            skLineSegment(sketch, "E9.22.13.5", {"start": v(334.96, 131.76) * mm, "end": v(334.96, 122.24) * mm});
            skLineSegment(sketch, "E9.0.13.6", {"start": v(336.55, 146.05) * mm, "end": v(323.85, 146.05) * mm});
            skLineSegment(sketch, "E9.3.13.6", {"start": v(325.44, 157.16) * mm, "end": v(325.44, 147.64) * mm});
            skPoint(sketch, "E9.6.13.6", {"position": v(330.2, 152.4) * mm});
            skLineSegment(sketch, "E9.7.13.6", {"start": v(334.96, 147.64) * mm, "end": v(325.44, 147.64) * mm});
            skLineSegment(sketch, "E9.10.13.6", {"start": v(336.55, 158.75) * mm, "end": v(336.55, 146.05) * mm});
            skLineSegment(sketch, "E9.13.13.6", {"start": v(336.55, 158.75) * mm, "end": v(323.85, 158.75) * mm});
            skLineSegment(sketch, "E9.16.13.6", {"start": v(323.85, 158.75) * mm, "end": v(323.85, 146.05) * mm});
            skLineSegment(sketch, "E9.19.13.6", {"start": v(334.96, 157.16) * mm, "end": v(325.44, 157.16) * mm});
            skLineSegment(sketch, "E9.22.13.6", {"start": v(334.96, 157.16) * mm, "end": v(334.96, 147.64) * mm});
            skLineSegment(sketch, "E9.0.13.7", {"start": v(336.55, 171.45) * mm, "end": v(323.85, 171.45) * mm});
            skLineSegment(sketch, "E9.3.13.7", {"start": v(325.44, 182.56) * mm, "end": v(325.44, 173.04) * mm});
            skPoint(sketch, "E9.6.13.7", {"position": v(330.2, 177.8) * mm});
            skLineSegment(sketch, "E9.7.13.7", {"start": v(334.96, 173.04) * mm, "end": v(325.44, 173.04) * mm});
            skLineSegment(sketch, "E9.10.13.7", {"start": v(336.55, 184.15) * mm, "end": v(336.55, 171.45) * mm});
            skLineSegment(sketch, "E9.13.13.7", {"start": v(336.55, 184.15) * mm, "end": v(323.85, 184.15) * mm});
            skLineSegment(sketch, "E9.16.13.7", {"start": v(323.85, 184.15) * mm, "end": v(323.85, 171.45) * mm});
            skLineSegment(sketch, "E9.19.13.7", {"start": v(334.96, 182.56) * mm, "end": v(325.44, 182.56) * mm});
            skLineSegment(sketch, "E9.22.13.7", {"start": v(334.96, 182.56) * mm, "end": v(334.96, 173.04) * mm});
            skLineSegment(sketch, "E9.0.13.8", {"start": v(336.55, 196.85) * mm, "end": v(323.85, 196.85) * mm});
            skLineSegment(sketch, "E9.3.13.8", {"start": v(325.44, 207.96) * mm, "end": v(325.44, 198.44) * mm});
            skPoint(sketch, "E9.6.13.8", {"position": v(330.2, 203.2) * mm});
            skLineSegment(sketch, "E9.7.13.8", {"start": v(334.96, 198.44) * mm, "end": v(325.44, 198.44) * mm});
            skLineSegment(sketch, "E9.10.13.8", {"start": v(336.55, 209.55) * mm, "end": v(336.55, 196.85) * mm});
            skLineSegment(sketch, "E9.13.13.8", {"start": v(336.55, 209.55) * mm, "end": v(323.85, 209.55) * mm});
            skLineSegment(sketch, "E9.16.13.8", {"start": v(323.85, 209.55) * mm, "end": v(323.85, 196.85) * mm});
            skLineSegment(sketch, "E9.19.13.8", {"start": v(334.96, 207.96) * mm, "end": v(325.44, 207.96) * mm});
            skLineSegment(sketch, "E9.22.13.8", {"start": v(334.96, 207.96) * mm, "end": v(334.96, 198.44) * mm});
            skLineSegment(sketch, "E9.0.13.9", {"start": v(336.55, 222.25) * mm, "end": v(323.85, 222.25) * mm});
            skLineSegment(sketch, "E9.3.13.9", {"start": v(325.44, 233.36) * mm, "end": v(325.44, 223.84) * mm});
            skPoint(sketch, "E9.6.13.9", {"position": v(330.2, 228.6) * mm});
            skLineSegment(sketch, "E9.7.13.9", {"start": v(334.96, 223.84) * mm, "end": v(325.44, 223.84) * mm});
            skLineSegment(sketch, "E9.10.13.9", {"start": v(336.55, 234.95) * mm, "end": v(336.55, 222.25) * mm});
            skLineSegment(sketch, "E9.13.13.9", {"start": v(336.55, 234.95) * mm, "end": v(323.85, 234.95) * mm});
            skLineSegment(sketch, "E9.16.13.9", {"start": v(323.85, 234.95) * mm, "end": v(323.85, 222.25) * mm});
            skLineSegment(sketch, "E9.19.13.9", {"start": v(334.96, 233.36) * mm, "end": v(325.44, 233.36) * mm});
            skLineSegment(sketch, "E9.22.13.9", {"start": v(334.96, 233.36) * mm, "end": v(334.96, 223.84) * mm});
            skLineSegment(sketch, "E9.0.13.10", {"start": v(336.55, 247.65) * mm, "end": v(323.85, 247.65) * mm});
            skLineSegment(sketch, "E9.3.13.10", {"start": v(325.44, 258.76) * mm, "end": v(325.44, 249.24) * mm});
            skPoint(sketch, "E9.6.13.10", {"position": v(330.2, 254) * mm});
            skLineSegment(sketch, "E9.7.13.10", {"start": v(334.96, 249.24) * mm, "end": v(325.44, 249.24) * mm});
            skLineSegment(sketch, "E9.10.13.10", {"start": v(336.55, 260.35) * mm, "end": v(336.55, 247.65) * mm});
            skLineSegment(sketch, "E9.13.13.10", {"start": v(336.55, 260.35) * mm, "end": v(323.85, 260.35) * mm});
            skLineSegment(sketch, "E9.16.13.10", {"start": v(323.85, 260.35) * mm, "end": v(323.85, 247.65) * mm});
            skLineSegment(sketch, "E9.19.13.10", {"start": v(334.96, 258.76) * mm, "end": v(325.44, 258.76) * mm});
            skLineSegment(sketch, "E9.22.13.10", {"start": v(334.96, 258.76) * mm, "end": v(334.96, 249.24) * mm});
            skLineSegment(sketch, "E9.0.13.11", {"start": v(336.55, 273.05) * mm, "end": v(323.85, 273.05) * mm});
            skLineSegment(sketch, "E9.3.13.11", {"start": v(325.44, 284.16) * mm, "end": v(325.44, 274.64) * mm});
            skPoint(sketch, "E9.6.13.11", {"position": v(330.2, 279.4) * mm});
            skLineSegment(sketch, "E9.7.13.11", {"start": v(334.96, 274.64) * mm, "end": v(325.44, 274.64) * mm});
            skLineSegment(sketch, "E9.10.13.11", {"start": v(336.55, 285.75) * mm, "end": v(336.55, 273.05) * mm});
            skLineSegment(sketch, "E9.13.13.11", {"start": v(336.55, 285.75) * mm, "end": v(323.85, 285.75) * mm});
            skLineSegment(sketch, "E9.16.13.11", {"start": v(323.85, 285.75) * mm, "end": v(323.85, 273.05) * mm});
            skLineSegment(sketch, "E9.19.13.11", {"start": v(334.96, 284.16) * mm, "end": v(325.44, 284.16) * mm});
            skLineSegment(sketch, "E9.22.13.11", {"start": v(334.96, 284.16) * mm, "end": v(334.96, 274.64) * mm});
            skLineSegment(sketch, "E9.0.13.12", {"start": v(336.55, 298.45) * mm, "end": v(323.85, 298.45) * mm});
            skLineSegment(sketch, "E9.3.13.12", {"start": v(325.44, 309.56) * mm, "end": v(325.44, 300.04) * mm});
            skPoint(sketch, "E9.6.13.12", {"position": v(330.2, 304.8) * mm});
            skLineSegment(sketch, "E9.7.13.12", {"start": v(334.96, 300.04) * mm, "end": v(325.44, 300.04) * mm});
            skLineSegment(sketch, "E9.10.13.12", {"start": v(336.55, 311.15) * mm, "end": v(336.55, 298.45) * mm});
            skLineSegment(sketch, "E9.13.13.12", {"start": v(336.55, 311.15) * mm, "end": v(323.85, 311.15) * mm});
            skLineSegment(sketch, "E9.16.13.12", {"start": v(323.85, 311.15) * mm, "end": v(323.85, 298.45) * mm});
            skLineSegment(sketch, "E9.19.13.12", {"start": v(334.96, 309.56) * mm, "end": v(325.44, 309.56) * mm});
            skLineSegment(sketch, "E9.22.13.12", {"start": v(334.96, 309.56) * mm, "end": v(334.96, 300.04) * mm});
            skLineSegment(sketch, "E9.0.13.13", {"start": v(336.55, 323.85) * mm, "end": v(323.85, 323.85) * mm});
            skLineSegment(sketch, "E9.3.13.13", {"start": v(325.44, 334.96) * mm, "end": v(325.44, 325.44) * mm});
            skPoint(sketch, "E9.6.13.13", {"position": v(330.2, 330.2) * mm});
            skLineSegment(sketch, "E9.7.13.13", {"start": v(334.96, 325.44) * mm, "end": v(325.44, 325.44) * mm});
            skLineSegment(sketch, "E9.10.13.13", {"start": v(336.55, 336.55) * mm, "end": v(336.55, 323.85) * mm});
            skLineSegment(sketch, "E9.13.13.13", {"start": v(336.55, 336.55) * mm, "end": v(323.85, 336.55) * mm});
            skLineSegment(sketch, "E9.16.13.13", {"start": v(323.85, 336.55) * mm, "end": v(323.85, 323.85) * mm});
            skLineSegment(sketch, "E9.19.13.13", {"start": v(334.96, 334.96) * mm, "end": v(325.44, 334.96) * mm});
            skLineSegment(sketch, "E9.22.13.13", {"start": v(334.96, 334.96) * mm, "end": v(334.96, 325.44) * mm});
            skLineSegment(sketch, "E9.0.13.14", {"start": v(336.55, 349.25) * mm, "end": v(323.85, 349.25) * mm});
            skLineSegment(sketch, "E9.3.13.14", {"start": v(325.44, 360.36) * mm, "end": v(325.44, 350.84) * mm});
            skPoint(sketch, "E9.6.13.14", {"position": v(330.2, 355.6) * mm});
            skLineSegment(sketch, "E9.7.13.14", {"start": v(334.96, 350.84) * mm, "end": v(325.44, 350.84) * mm});
            skLineSegment(sketch, "E9.10.13.14", {"start": v(336.55, 361.95) * mm, "end": v(336.55, 349.25) * mm});
            skLineSegment(sketch, "E9.13.13.14", {"start": v(336.55, 361.95) * mm, "end": v(323.85, 361.95) * mm});
            skLineSegment(sketch, "E9.16.13.14", {"start": v(323.85, 361.95) * mm, "end": v(323.85, 349.25) * mm});
            skLineSegment(sketch, "E9.19.13.14", {"start": v(334.96, 360.36) * mm, "end": v(325.44, 360.36) * mm});
            skLineSegment(sketch, "E9.22.13.14", {"start": v(334.96, 360.36) * mm, "end": v(334.96, 350.84) * mm});
            skLineSegment(sketch, "E9.0.13.15", {"start": v(336.55, 374.65) * mm, "end": v(323.85, 374.65) * mm});
            skLineSegment(sketch, "E9.3.13.15", {"start": v(325.44, 385.76) * mm, "end": v(325.44, 376.24) * mm});
            skPoint(sketch, "E9.6.13.15", {"position": v(330.2, 381) * mm});
            skLineSegment(sketch, "E9.7.13.15", {"start": v(334.96, 376.24) * mm, "end": v(325.44, 376.24) * mm});
            skLineSegment(sketch, "E9.10.13.15", {"start": v(336.55, 387.35) * mm, "end": v(336.55, 374.65) * mm});
            skLineSegment(sketch, "E9.13.13.15", {"start": v(336.55, 387.35) * mm, "end": v(323.85, 387.35) * mm});
            skLineSegment(sketch, "E9.16.13.15", {"start": v(323.85, 387.35) * mm, "end": v(323.85, 374.65) * mm});
            skLineSegment(sketch, "E9.19.13.15", {"start": v(334.96, 385.76) * mm, "end": v(325.44, 385.76) * mm});
            skLineSegment(sketch, "E9.22.13.15", {"start": v(334.96, 385.76) * mm, "end": v(334.96, 376.24) * mm});
            skLineSegment(sketch, "E9.0.13.16", {"start": v(336.55, 400.05) * mm, "end": v(323.85, 400.05) * mm});
            skLineSegment(sketch, "E9.3.13.16", {"start": v(325.44, 411.16) * mm, "end": v(325.44, 401.64) * mm});
            skPoint(sketch, "E9.6.13.16", {"position": v(330.2, 406.4) * mm});
            skLineSegment(sketch, "E9.7.13.16", {"start": v(334.96, 401.64) * mm, "end": v(325.44, 401.64) * mm});
            skLineSegment(sketch, "E9.10.13.16", {"start": v(336.55, 412.75) * mm, "end": v(336.55, 400.05) * mm});
            skLineSegment(sketch, "E9.13.13.16", {"start": v(336.55, 412.75) * mm, "end": v(323.85, 412.75) * mm});
            skLineSegment(sketch, "E9.16.13.16", {"start": v(323.85, 412.75) * mm, "end": v(323.85, 400.05) * mm});
            skLineSegment(sketch, "E9.19.13.16", {"start": v(334.96, 411.16) * mm, "end": v(325.44, 411.16) * mm});
            skLineSegment(sketch, "E9.22.13.16", {"start": v(334.96, 411.16) * mm, "end": v(334.96, 401.64) * mm});
            skLineSegment(sketch, "E9.0.13.17", {"start": v(336.55, 425.45) * mm, "end": v(323.85, 425.45) * mm});
            skLineSegment(sketch, "E9.3.13.17", {"start": v(325.44, 436.56) * mm, "end": v(325.44, 427.04) * mm});
            skPoint(sketch, "E9.6.13.17", {"position": v(330.2, 431.8) * mm});
            skLineSegment(sketch, "E9.7.13.17", {"start": v(334.96, 427.04) * mm, "end": v(325.44, 427.04) * mm});
            skLineSegment(sketch, "E9.10.13.17", {"start": v(336.55, 438.15) * mm, "end": v(336.55, 425.45) * mm});
            skLineSegment(sketch, "E9.13.13.17", {"start": v(336.55, 438.15) * mm, "end": v(323.85, 438.15) * mm});
            skLineSegment(sketch, "E9.16.13.17", {"start": v(323.85, 438.15) * mm, "end": v(323.85, 425.45) * mm});
            skLineSegment(sketch, "E9.19.13.17", {"start": v(334.96, 436.56) * mm, "end": v(325.44, 436.56) * mm});
            skLineSegment(sketch, "E9.22.13.17", {"start": v(334.96, 436.56) * mm, "end": v(334.96, 427.04) * mm});
            skLineSegment(sketch, "E9.0.13.18", {"start": v(336.55, 450.85) * mm, "end": v(323.85, 450.85) * mm});
            skLineSegment(sketch, "E9.3.13.18", {"start": v(325.44, 461.96) * mm, "end": v(325.44, 452.44) * mm});
            skPoint(sketch, "E9.6.13.18", {"position": v(330.2, 457.2) * mm});
            skLineSegment(sketch, "E9.7.13.18", {"start": v(334.96, 452.44) * mm, "end": v(325.44, 452.44) * mm});
            skLineSegment(sketch, "E9.10.13.18", {"start": v(336.55, 463.55) * mm, "end": v(336.55, 450.85) * mm});
            skLineSegment(sketch, "E9.13.13.18", {"start": v(336.55, 463.55) * mm, "end": v(323.85, 463.55) * mm});
            skLineSegment(sketch, "E9.16.13.18", {"start": v(323.85, 463.55) * mm, "end": v(323.85, 450.85) * mm});
            skLineSegment(sketch, "E9.19.13.18", {"start": v(334.96, 461.96) * mm, "end": v(325.44, 461.96) * mm});
            skLineSegment(sketch, "E9.22.13.18", {"start": v(334.96, 461.96) * mm, "end": v(334.96, 452.44) * mm});
            skLineSegment(sketch, "E9.0.13.19", {"start": v(336.55, 476.25) * mm, "end": v(323.85, 476.25) * mm});
            skLineSegment(sketch, "E9.3.13.19", {"start": v(325.44, 487.36) * mm, "end": v(325.44, 477.84) * mm});
            skPoint(sketch, "E9.6.13.19", {"position": v(330.2, 482.6) * mm});
            skLineSegment(sketch, "E9.7.13.19", {"start": v(334.96, 477.84) * mm, "end": v(325.44, 477.84) * mm});
            skLineSegment(sketch, "E9.10.13.19", {"start": v(336.55, 488.95) * mm, "end": v(336.55, 476.25) * mm});
            skLineSegment(sketch, "E9.13.13.19", {"start": v(336.55, 488.95) * mm, "end": v(323.85, 488.95) * mm});
            skLineSegment(sketch, "E9.16.13.19", {"start": v(323.85, 488.95) * mm, "end": v(323.85, 476.25) * mm});
            skLineSegment(sketch, "E9.19.13.19", {"start": v(334.96, 487.36) * mm, "end": v(325.44, 487.36) * mm});
            skLineSegment(sketch, "E9.22.13.19", {"start": v(334.96, 487.36) * mm, "end": v(334.96, 477.84) * mm});
            skLineSegment(sketch, "E9.0.13.20", {"start": v(336.55, 501.65) * mm, "end": v(323.85, 501.65) * mm});
            skLineSegment(sketch, "E9.3.13.20", {"start": v(325.44, 512.76) * mm, "end": v(325.44, 503.24) * mm});
            skPoint(sketch, "E9.6.13.20", {"position": v(330.2, 508) * mm});
            skLineSegment(sketch, "E9.7.13.20", {"start": v(334.96, 503.24) * mm, "end": v(325.44, 503.24) * mm});
            skLineSegment(sketch, "E9.10.13.20", {"start": v(336.55, 514.35) * mm, "end": v(336.55, 501.65) * mm});
            skLineSegment(sketch, "E9.13.13.20", {"start": v(336.55, 514.35) * mm, "end": v(323.85, 514.35) * mm});
            skLineSegment(sketch, "E9.16.13.20", {"start": v(323.85, 514.35) * mm, "end": v(323.85, 501.65) * mm});
            skLineSegment(sketch, "E9.19.13.20", {"start": v(334.96, 512.76) * mm, "end": v(325.44, 512.76) * mm});
            skLineSegment(sketch, "E9.22.13.20", {"start": v(334.96, 512.76) * mm, "end": v(334.96, 503.24) * mm});
            skLineSegment(sketch, "E9.0.13.21", {"start": v(336.55, 527.05) * mm, "end": v(323.85, 527.05) * mm});
            skLineSegment(sketch, "E9.3.13.21", {"start": v(325.44, 538.16) * mm, "end": v(325.44, 528.64) * mm});
            skPoint(sketch, "E9.6.13.21", {"position": v(330.2, 533.4) * mm});
            skLineSegment(sketch, "E9.7.13.21", {"start": v(334.96, 528.64) * mm, "end": v(325.44, 528.64) * mm});
            skLineSegment(sketch, "E9.10.13.21", {"start": v(336.55, 539.75) * mm, "end": v(336.55, 527.05) * mm});
            skLineSegment(sketch, "E9.13.13.21", {"start": v(336.55, 539.75) * mm, "end": v(323.85, 539.75) * mm});
            skLineSegment(sketch, "E9.16.13.21", {"start": v(323.85, 539.75) * mm, "end": v(323.85, 527.05) * mm});
            skLineSegment(sketch, "E9.19.13.21", {"start": v(334.96, 538.16) * mm, "end": v(325.44, 538.16) * mm});
            skLineSegment(sketch, "E9.22.13.21", {"start": v(334.96, 538.16) * mm, "end": v(334.96, 528.64) * mm});
            skLineSegment(sketch, "E10.0", {"start": v(-7.94, -7.94) * mm, "end": v(-7.94, 554.04) * mm});
            skLineSegment(sketch, "E10.1", {"start": v(338.14, -7.94) * mm, "end": v(-7.94, -7.94) * mm});
            skLineSegment(sketch, "E10.2", {"start": v(338.14, -7.94) * mm, "end": v(338.14, 554.04) * mm});
            skLineSegment(sketch, "E10.3", {"start": v(-7.94, 554.04) * mm, "end": v(338.14, 554.04) * mm});
            skSolve(sketch);
        }
        {
            var Q0;
            Q0 = qSketchRegion(id + "F0", true);
            var Q1;
            {var subQ23=sQuery(id+"F0.wireOp",EDGE,"E0.bottom");Q1=makeQuery(id+"F0.imprint","IMPRINT",FACE,{"disambiguationData":[TD([[makeQuery(id+"F0.imprint","IMPRINT",EDGE,{"derivedFrom":subQ23}),-1.0]])]});}
            extrude(context, id + "F1", {"entities" : qUnion([Q0, Q1]), "depth" : 1.59 * mm});
        }
    });
